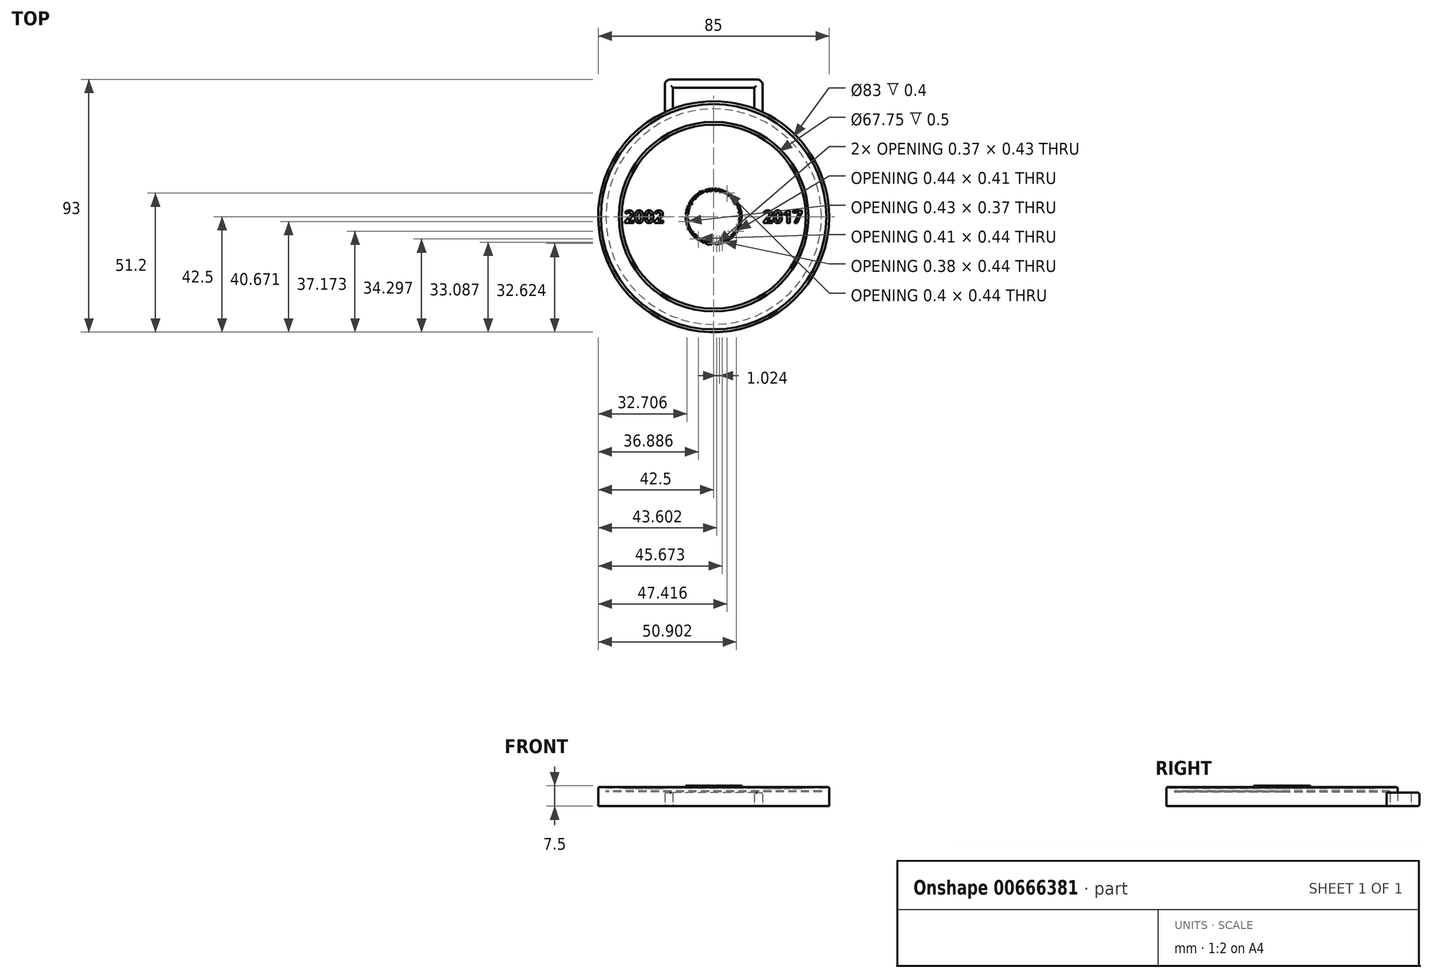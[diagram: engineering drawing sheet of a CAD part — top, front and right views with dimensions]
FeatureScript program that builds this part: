
annotation { "Feature Type Name" : "Feature", "Feature Type Description" : "" }
export const myFeature = defineFeature(function(context is Context, id is Id, definition is map)
    precondition{}
    {
        {
            var Q0;
            Q0=qCreatedBy(makeId("Top.planeOp"),FACE);
            var sketch = newSketch(context, id + "F0", { "sketchPlane" : qUnion([Q0])});
            skCircle(sketch, "E0", {"center": v(0, 0) * mm, "radius": 42.5 * mm});
            skSolve(sketch);
        }
        {
            var Q0;
            Q0 = qSketchRegion(id + "F0", true);
            extrude(context, id + "F1", {"entities" : qUnion([Q0]), "depth" : 7 * mm, "offsetDistance" : 25 * mm});
        }
        {
            var Q0;
            Q0=makeQuery(id+"F1.opExtrude","CAP_FACE",FACE,{"disambiguationData":[OSD([sQuery(id+"F0.wireOp",EDGE,"E0")])],"isStart":true});
            var sketch = newSketch(context, id + "F2", { "sketchPlane" : qUnion([Q0])});
            skLineSegment(sketch, "E1.bottom", {"start": v(-18, -50.5) * mm, "end": v(18, -50.5) * mm, "construction": true});
            skLineSegment(sketch, "E1.top", {"start": v(-18, -22.56) * mm, "end": v(18, -22.56) * mm, "construction": true});
            skLineSegment(sketch, "E1.left", {"start": v(-18, -50.5) * mm, "end": v(-18, -22.56) * mm, "construction": true});
            skLineSegment(sketch, "E1.right", {"start": v(18, -50.5) * mm, "end": v(18, -22.56) * mm, "construction": true});
            skLineSegment(sketch, "E2.bottom", {"start": v(-15, -47.5) * mm, "end": v(15, -47.5) * mm, "construction": true});
            skLineSegment(sketch, "E2.top", {"start": v(-15, -26.02) * mm, "end": v(15, -26.02) * mm, "construction": true});
            skLineSegment(sketch, "E2.left", {"start": v(-15, -47.5) * mm, "end": v(-15, -26.02) * mm, "construction": true});
            skLineSegment(sketch, "E2.right", {"start": v(15, -47.5) * mm, "end": v(15, -26.02) * mm, "construction": true});
            skLineSegment(sketch, "E3", {"start": v(-18, -22.56) * mm, "end": v(-18, -50.5) * mm});
            skLineSegment(sketch, "E4", {"start": v(18, -50.5) * mm, "end": v(-18, -50.5) * mm});
            skLineSegment(sketch, "E5", {"start": v(18, -50.5) * mm, "end": v(18, -22.56) * mm});
            skLineSegment(sketch, "E6", {"start": v(18, -22.56) * mm, "end": v(15, -26.02) * mm});
            skLineSegment(sketch, "E7", {"start": v(15, -47.5) * mm, "end": v(15, -26.02) * mm});
            skLineSegment(sketch, "E8", {"start": v(15, -47.5) * mm, "end": v(-15, -47.5) * mm});
            skLineSegment(sketch, "E9", {"start": v(-15, -47.5) * mm, "end": v(-15, -26.02) * mm});
            skLineSegment(sketch, "E10", {"start": v(-15, -26.02) * mm, "end": v(-18, -22.56) * mm});
            skSolve(sketch);
        }
        {
            var Q0;
            Q0 = qSketchRegion(id + "F2", true);
            extrude(context, id + "F3", {"entities" : qUnion([Q0]), "operationType" : NewBodyOperationType.ADD, "oppositeDirection" : true, "depth" : 5 * mm, "offsetDistance" : 25 * mm});
        }
        {
            var Q0;
            Q0=makeQuery(id+"F3.opExtrude","CAP_EDGE",EDGE,{"disambiguationData":[OSD([sQuery(id+"F2.wireOp",EDGE,"E4")])],"isStart":false});
            var Q1;
            Q1=makeQuery(id+"F3.opExtrude","CAP_EDGE",EDGE,{"disambiguationData":[OSD([sQuery(id+"F2.wireOp",EDGE,"E3")])],"isStart":false});
            var Q2;
            Q2=makeQuery(id+"F3.opExtrude","CAP_EDGE",EDGE,{"disambiguationData":[OSD([sQuery(id+"F2.wireOp",EDGE,"E8")])],"isStart":false});
            var Q3;
            Q3=makeQuery(id+"F3.opExtrude","CAP_EDGE",EDGE,{"disambiguationData":[OSD([sQuery(id+"F2.wireOp",EDGE,"E7")])],"isStart":false});
            var Q4;
            Q4=makeQuery(id+"F3.opExtrude","CAP_EDGE",EDGE,{"disambiguationData":[OSD([sQuery(id+"F2.wireOp",EDGE,"E9")])],"isStart":false});
            var Q5;
            Q5=makeQuery(id+"F3.opExtrude","CAP_EDGE",EDGE,{"disambiguationData":[OSD([sQuery(id+"F2.wireOp",EDGE,"E5")])],"isStart":false});
            var Q6;
            Q6=makeQuery(id+"F3.opExtrude","CAP_EDGE",EDGE,{"disambiguationData":[OSD([sQuery(id+"F2.wireOp",EDGE,"E8")])],"isStart":true});
            var Q7;
            Q7=makeQuery(id+"F3.opExtrude","CAP_EDGE",EDGE,{"disambiguationData":[OSD([sQuery(id+"F2.wireOp",EDGE,"E4")])],"isStart":true});
            var Q8;
            Q8=makeQuery(id+"F3.opExtrude","CAP_EDGE",EDGE,{"disambiguationData":[OSD([sQuery(id+"F2.wireOp",EDGE,"E5")])],"isStart":true});
            var Q9;
            Q9=makeQuery(id+"F3.opExtrude","CAP_EDGE",EDGE,{"disambiguationData":[OSD([sQuery(id+"F2.wireOp",EDGE,"E7")])],"isStart":true});
            var Q10;
            Q10=makeQuery(id+"F3.opExtrude","CAP_EDGE",EDGE,{"disambiguationData":[OSD([sQuery(id+"F2.wireOp",EDGE,"E9")])],"isStart":true});
            var Q11;
            Q11=makeQuery(id+"F3.opExtrude","CAP_EDGE",EDGE,{"disambiguationData":[OSD([sQuery(id+"F2.wireOp",EDGE,"E3")])],"isStart":true});
            fillet(context, id + "F4", {"entities" : qUnion([Q0, Q1, Q2, Q3, Q4, Q5, Q6, Q7, Q8, Q9, Q10, Q11]), "radius" : 0.6 * mm, "tangentPropagation" : true, "allowEdgeOverflow" : false});
        }
        {
            var Q0;
            Q0=makeQuery(id+"F3.opExtrude","SWEPT_EDGE",EDGE,{"disambiguationData":[OSD([sQuery(id+"F2.wireOp",EDGE,"E3"),sQuery(id+"F2.wireOp",EDGE,"E4")])]});
            var Q1;
            Q1=makeQuery(id+"F3.opExtrude","SWEPT_EDGE",EDGE,{"disambiguationData":[OSD([sQuery(id+"F2.wireOp",EDGE,"E4"),sQuery(id+"F2.wireOp",EDGE,"E5")])]});
            fillet(context, id + "F5", {"entities" : qUnion([Q0, Q1]), "radius" : 2 * mm, "tangentPropagation" : true, "allowEdgeOverflow" : false});
        }
        {
            var Q0;
            Q0=makeQuery(id+"F1.opExtrude","CAP_FACE",FACE,{"disambiguationData":[OSD([sQuery(id+"F0.wireOp",EDGE,"E0")])],"isStart":false});
            var sketch = newSketch(context, id + "F6", { "sketchPlane" : qUnion([Q0])});
            skFitSpline(sketch, "E11", {"points": [v(1.08, -9.67) * mm, v(1.02, -9.67) * mm, v(0.98, -9.7) * mm, v(0.95, -9.73) * mm]});
            skFitSpline(sketch, "E12", {"points": [v(0.95, -9.73) * mm, v(0.93, -9.77) * mm, v(0.92, -9.83) * mm, v(0.92, -9.9) * mm]});
            skFitSpline(sketch, "E13", {"points": [v(0.92, -9.9) * mm, v(0.93, -9.96) * mm, v(0.95, -10.01) * mm, v(0.98, -10.05) * mm]});
            skFitSpline(sketch, "E14", {"points": [v(0.98, -10.05) * mm, v(1.02, -10.08) * mm, v(1.07, -10.1) * mm, v(1.13, -10.09) * mm]});
            skFitSpline(sketch, "E15", {"points": [v(1.13, -10.09) * mm, v(1.18, -10.08) * mm, v(1.23, -10.06) * mm, v(1.25, -10.02) * mm]});
            skFitSpline(sketch, "E16", {"points": [v(1.25, -10.02) * mm, v(1.28, -9.98) * mm, v(1.29, -9.92) * mm, v(1.28, -9.85) * mm]});
            skFitSpline(sketch, "E17", {"points": [v(1.28, -9.85) * mm, v(1.27, -9.79) * mm, v(1.25, -9.74) * mm, v(1.21, -9.7) * mm]});
            skFitSpline(sketch, "E18", {"points": [v(1.21, -9.7) * mm, v(1.18, -9.67) * mm, v(1.13, -9.66) * mm, v(1.08, -9.67) * mm]});
            skFitSpline(sketch, "E19", {"points": [v(1.06, -9.5) * mm, v(1.2, -9.49) * mm, v(1.3, -9.5) * mm, v(1.4, -9.56) * mm]});
            skFitSpline(sketch, "E20", {"points": [v(1.4, -9.56) * mm, v(1.48, -9.61) * mm, v(1.53, -9.7) * mm, v(1.55, -9.81) * mm]});
            skFitSpline(sketch, "E21", {"points": [v(1.55, -9.81) * mm, v(1.57, -9.93) * mm, v(1.55, -10.03) * mm, v(1.47, -10.1) * mm]});
            skFitSpline(sketch, "E22", {"points": [v(1.47, -10.1) * mm, v(1.4, -10.18) * mm, v(1.3, -10.23) * mm, v(1.14, -10.25) * mm]});
            skFitSpline(sketch, "E23", {"points": [v(1.14, -10.25) * mm, v(1, -10.26) * mm, v(0.88, -10.24) * mm, v(0.79, -10.18) * mm]});
            skFitSpline(sketch, "E24", {"points": [v(0.79, -10.18) * mm, v(0.7, -10.12) * mm, v(0.65, -10.03) * mm, v(0.65, -9.92) * mm]});
            skFitSpline(sketch, "E25", {"points": [v(0.65, -9.92) * mm, v(0.64, -9.8) * mm, v(0.67, -9.7) * mm, v(0.75, -9.63) * mm]});
            skFitSpline(sketch, "E26", {"points": [v(0.75, -9.63) * mm, v(0.82, -9.56) * mm, v(0.92, -9.52) * mm, v(1.06, -9.5) * mm]});
            skFitSpline(sketch, "E27", {"points": [v(2.15, -9.05) * mm, v(2.23, -9.03) * mm, v(2.3, -9) * mm, v(2.39, -8.99) * mm]});
            skLineSegment(sketch, "E28", {"start": v(2.24, -9.42) * mm, "end": v(2.15, -9.05) * mm});
            skFitSpline(sketch, "E29", {"points": [v(2.65, -9.94) * mm, v(2.56, -9.97) * mm, v(2.47, -10) * mm, v(2.38, -10.01) * mm]});
            skLineSegment(sketch, "E30", {"start": v(2.39, -8.99) * mm, "end": v(2.65, -9.94) * mm});
            skFitSpline(sketch, "E31", {"points": [v(2.35, -9.91) * mm, v(2.33, -9.96) * mm, v(2.3, -10) * mm, v(2.25, -10.03) * mm]});
            skFitSpline(sketch, "E32", {"points": [v(2.25, -10.03) * mm, v(2.21, -10.06) * mm, v(2.16, -10.08) * mm, v(2.1, -10.1) * mm]});
            skFitSpline(sketch, "E33", {"points": [v(2.1, -10.1) * mm, v(2, -10.11) * mm, v(1.91, -10.1) * mm, v(1.83, -10.04) * mm]});
            skFitSpline(sketch, "E34", {"points": [v(1.83, -10.04) * mm, v(1.75, -9.98) * mm, v(1.7, -9.9) * mm, v(1.69, -9.8) * mm]});
            skFitSpline(sketch, "E35", {"points": [v(1.69, -9.8) * mm, v(1.67, -9.68) * mm, v(1.68, -9.59) * mm, v(1.73, -9.5) * mm]});
            skFitSpline(sketch, "E36", {"points": [v(1.73, -9.5) * mm, v(1.78, -9.43) * mm, v(1.86, -9.38) * mm, v(1.95, -9.36) * mm]});
            skFitSpline(sketch, "E37", {"points": [v(1.95, -9.36) * mm, v(2, -9.35) * mm, v(2.05, -9.35) * mm, v(2.1, -9.36) * mm]});
            skFitSpline(sketch, "E38", {"points": [v(2.1, -9.36) * mm, v(2.15, -9.37) * mm, v(2.2, -9.39) * mm, v(2.24, -9.42) * mm]});
            skLineSegment(sketch, "E39", {"start": v(2.38, -10.01) * mm, "end": v(2.35, -9.91) * mm});
            skFitSpline(sketch, "E40", {"points": [v(2.17, -9.9) * mm, v(2.23, -9.9) * mm, v(2.27, -9.87) * mm, v(2.29, -9.83) * mm]});
            skFitSpline(sketch, "E41", {"points": [v(2.29, -9.83) * mm, v(2.3, -9.79) * mm, v(2.31, -9.73) * mm, v(2.3, -9.67) * mm]});
            skFitSpline(sketch, "E42", {"points": [v(2.3, -9.67) * mm, v(2.28, -9.6) * mm, v(2.25, -9.55) * mm, v(2.22, -9.52) * mm]});
            skFitSpline(sketch, "E43", {"points": [v(2.22, -9.52) * mm, v(2.18, -9.5) * mm, v(2.13, -9.49) * mm, v(2.08, -9.5) * mm]});
            skFitSpline(sketch, "E44", {"points": [v(2.08, -9.5) * mm, v(2.03, -9.51) * mm, v(1.99, -9.54) * mm, v(1.97, -9.58) * mm]});
            skFitSpline(sketch, "E45", {"points": [v(1.97, -9.58) * mm, v(1.95, -9.62) * mm, v(1.94, -9.67) * mm, v(1.95, -9.74) * mm]});
            skFitSpline(sketch, "E46", {"points": [v(1.95, -9.74) * mm, v(1.97, -9.8) * mm, v(2, -9.86) * mm, v(2.03, -9.88) * mm]});
            skFitSpline(sketch, "E47", {"points": [v(2.03, -9.88) * mm, v(2.07, -9.91) * mm, v(2.11, -9.92) * mm, v(2.17, -9.9) * mm]});
            skFitSpline(sketch, "E48", {"points": [v(3.12, -8.76) * mm, v(3.2, -8.73) * mm, v(3.28, -8.7) * mm, v(3.36, -8.67) * mm]});
            skLineSegment(sketch, "E49", {"start": v(3.25, -9.12) * mm, "end": v(3.12, -8.76) * mm});
            skFitSpline(sketch, "E50", {"points": [v(3.72, -9.6) * mm, v(3.63, -9.63) * mm, v(3.54, -9.66) * mm, v(3.46, -9.7) * mm]});
            skLineSegment(sketch, "E51", {"start": v(3.36, -8.67) * mm, "end": v(3.72, -9.6) * mm});
            skFitSpline(sketch, "E52", {"points": [v(3.42, -9.6) * mm, v(3.4, -9.65) * mm, v(3.37, -9.69) * mm, v(3.34, -9.72) * mm]});
            skFitSpline(sketch, "E53", {"points": [v(3.34, -9.72) * mm, v(3.3, -9.76) * mm, v(3.25, -9.78) * mm, v(3.2, -9.8) * mm]});
            skFitSpline(sketch, "E54", {"points": [v(3.2, -9.8) * mm, v(3.1, -9.83) * mm, v(3, -9.83) * mm, v(2.92, -9.78) * mm]});
            skFitSpline(sketch, "E55", {"points": [v(2.92, -9.78) * mm, v(2.83, -9.73) * mm, v(2.77, -9.65) * mm, v(2.74, -9.55) * mm]});
            skFitSpline(sketch, "E56", {"points": [v(2.74, -9.55) * mm, v(2.71, -9.44) * mm, v(2.72, -9.35) * mm, v(2.76, -9.26) * mm]});
            skFitSpline(sketch, "E57", {"points": [v(2.76, -9.26) * mm, v(2.8, -9.18) * mm, v(2.87, -9.12) * mm, v(2.96, -9.09) * mm]});
            skFitSpline(sketch, "E58", {"points": [v(2.96, -9.09) * mm, v(3.01, -9.07) * mm, v(3.06, -9.06) * mm, v(3.1, -9.07) * mm]});
            skFitSpline(sketch, "E59", {"points": [v(3.1, -9.07) * mm, v(3.16, -9.07) * mm, v(3.2, -9.09) * mm, v(3.25, -9.12) * mm]});
            skLineSegment(sketch, "E60", {"start": v(3.46, -9.7) * mm, "end": v(3.42, -9.6) * mm});
            skFitSpline(sketch, "E61", {"points": [v(3.24, -9.61) * mm, v(3.3, -9.6) * mm, v(3.33, -9.56) * mm, v(3.35, -9.52) * mm]});
            skFitSpline(sketch, "E62", {"points": [v(3.35, -9.52) * mm, v(3.36, -9.47) * mm, v(3.36, -9.42) * mm, v(3.34, -9.35) * mm]});
            skFitSpline(sketch, "E63", {"points": [v(3.34, -9.35) * mm, v(3.31, -9.3) * mm, v(3.28, -9.25) * mm, v(3.24, -9.22) * mm]});
            skFitSpline(sketch, "E64", {"points": [v(3.24, -9.22) * mm, v(3.2, -9.2) * mm, v(3.16, -9.2) * mm, v(3.1, -9.21) * mm]});
            skFitSpline(sketch, "E65", {"points": [v(3.1, -9.21) * mm, v(3.05, -9.23) * mm, v(3.02, -9.26) * mm, v(3, -9.3) * mm]});
            skFitSpline(sketch, "E66", {"points": [v(3, -9.3) * mm, v(2.98, -9.35) * mm, v(2.99, -9.4) * mm, v(3, -9.47) * mm]});
            skFitSpline(sketch, "E67", {"points": [v(3, -9.47) * mm, v(3.03, -9.53) * mm, v(3.06, -9.58) * mm, v(3.1, -9.6) * mm]});
            skFitSpline(sketch, "E68", {"points": [v(3.1, -9.6) * mm, v(3.14, -9.63) * mm, v(3.18, -9.63) * mm, v(3.24, -9.61) * mm]});
            skFitSpline(sketch, "E69", {"points": [v(4.6, -8.87) * mm, v(4.42, -8.97) * mm, v(4.23, -9.06) * mm, v(4.04, -9.14) * mm]});
            skFitSpline(sketch, "E70", {"points": [v(4.04, -9.14) * mm, v(4.07, -9.19) * mm, v(4.1, -9.22) * mm, v(4.15, -9.22) * mm]});
            skFitSpline(sketch, "E71", {"points": [v(4.15, -9.22) * mm, v(4.2, -9.23) * mm, v(4.25, -9.22) * mm, v(4.32, -9.2) * mm]});
            skFitSpline(sketch, "E72", {"points": [v(4.32, -9.2) * mm, v(4.37, -9.17) * mm, v(4.42, -9.14) * mm, v(4.47, -9.1) * mm]});
            skFitSpline(sketch, "E73", {"points": [v(4.47, -9.1) * mm, v(4.51, -9.06) * mm, v(4.56, -9.01) * mm, v(4.6, -8.96) * mm]});
            skLineSegment(sketch, "E74", {"start": v(4.57, -8.81) * mm, "end": v(4.6, -8.87) * mm});
            skFitSpline(sketch, "E75", {"points": [v(4.68, -9.11) * mm, v(4.63, -9.16) * mm, v(4.58, -9.2) * mm, v(4.53, -9.24) * mm]});
            skFitSpline(sketch, "E76", {"points": [v(4.53, -9.24) * mm, v(4.47, -9.28) * mm, v(4.42, -9.31) * mm, v(4.36, -9.34) * mm]});
            skFitSpline(sketch, "E77", {"points": [v(4.36, -9.34) * mm, v(4.22, -9.4) * mm, v(4.1, -9.42) * mm, v(3.99, -9.4) * mm]});
            skFitSpline(sketch, "E78", {"points": [v(3.99, -9.4) * mm, v(3.88, -9.37) * mm, v(3.81, -9.3) * mm, v(3.77, -9.19) * mm]});
            skFitSpline(sketch, "E79", {"points": [v(3.77, -9.19) * mm, v(3.72, -9.08) * mm, v(3.72, -8.98) * mm, v(3.77, -8.89) * mm]});
            skFitSpline(sketch, "E80", {"points": [v(3.77, -8.89) * mm, v(3.82, -8.8) * mm, v(3.9, -8.72) * mm, v(4.03, -8.67) * mm]});
            skFitSpline(sketch, "E81", {"points": [v(4.03, -8.67) * mm, v(4.14, -8.61) * mm, v(4.25, -8.6) * mm, v(4.35, -8.63) * mm]});
            skFitSpline(sketch, "E82", {"points": [v(4.35, -8.63) * mm, v(4.44, -8.65) * mm, v(4.52, -8.71) * mm, v(4.57, -8.81) * mm]});
            skFitSpline(sketch, "E83", {"points": [v(4.57, -8.81) * mm, v(4.57, -8.81) * mm, v(4.57, -8.81) * mm, v(4.57, -8.81) * mm, v(4.57, -8.81) * mm]});
            skLineSegment(sketch, "E84", {"start": v(4.6, -8.96) * mm, "end": v(4.68, -9.11) * mm});
            skFitSpline(sketch, "E85", {"points": [v(4.3, -8.87) * mm, v(4.28, -8.83) * mm, v(4.25, -8.8) * mm, v(4.21, -8.8) * mm]});
            skFitSpline(sketch, "E86", {"points": [v(4.21, -8.8) * mm, v(4.17, -8.78) * mm, v(4.13, -8.78) * mm, v(4.1, -8.8) * mm]});
            skFitSpline(sketch, "E87", {"points": [v(4.1, -8.8) * mm, v(4.05, -8.82) * mm, v(4.01, -8.85) * mm, v(4, -8.89) * mm]});
            skFitSpline(sketch, "E88", {"points": [v(4, -8.89) * mm, v(3.98, -8.92) * mm, v(3.97, -8.96) * mm, v(3.99, -9.01) * mm]});
            skFitSpline(sketch, "E89", {"points": [v(3.99, -9.01) * mm, v(4.1, -8.96) * mm, v(4.2, -8.92) * mm, v(4.3, -8.87) * mm]});
            skFitSpline(sketch, "E90", {"points": [v(3.93, -8.63) * mm, v(3.84, -8.58) * mm, v(3.75, -8.53) * mm, v(3.67, -8.48) * mm]});
            skFitSpline(sketch, "E91", {"points": [v(3.67, -8.48) * mm, v(3.7, -8.47) * mm, v(3.74, -8.45) * mm, v(3.78, -8.43) * mm]});
            skFitSpline(sketch, "E92", {"points": [v(3.78, -8.43) * mm, v(3.84, -8.46) * mm, v(3.9, -8.48) * mm, v(3.97, -8.5) * mm]});
            skFitSpline(sketch, "E93", {"points": [v(3.97, -8.5) * mm, v(3.99, -8.45) * mm, v(4.01, -8.38) * mm, v(4.03, -8.32) * mm]});
            skFitSpline(sketch, "E94", {"points": [v(4.03, -8.32) * mm, v(4.07, -8.3) * mm, v(4.1, -8.28) * mm, v(4.14, -8.26) * mm]});
            skFitSpline(sketch, "E95", {"points": [v(4.14, -8.26) * mm, v(4.12, -8.36) * mm, v(4.1, -8.46) * mm, v(4.09, -8.56) * mm]});
            skFitSpline(sketch, "E96", {"points": [v(4.09, -8.56) * mm, v(4.03, -8.58) * mm, v(3.98, -8.6) * mm, v(3.93, -8.63) * mm]});
            skFitSpline(sketch, "E97", {"points": [v(4.45, -8.16) * mm, v(4.52, -8.12) * mm, v(4.6, -8.08) * mm, v(4.66, -8.04) * mm]});
            skFitSpline(sketch, "E98", {"points": [v(5.16, -8.9) * mm, v(5.08, -8.95) * mm, v(5, -9) * mm, v(4.92, -9.04) * mm]});
            skLineSegment(sketch, "E99", {"start": v(4.66, -8.04) * mm, "end": v(5.16, -8.9) * mm});
            skLineSegment(sketch, "E100", {"start": v(4.92, -9.04) * mm, "end": v(4.45, -8.16) * mm});
            skFitSpline(sketch, "E101", {"points": [v(5.93, -8.05) * mm, v(5.76, -8.18) * mm, v(5.59, -8.3) * mm, v(5.41, -8.4) * mm]});
            skFitSpline(sketch, "E102", {"points": [v(5.41, -8.4) * mm, v(5.45, -8.45) * mm, v(5.49, -8.47) * mm, v(5.54, -8.47) * mm]});
            skFitSpline(sketch, "E103", {"points": [v(5.54, -8.47) * mm, v(5.58, -8.47) * mm, v(5.64, -8.45) * mm, v(5.7, -8.41) * mm]});
            skFitSpline(sketch, "E104", {"points": [v(5.7, -8.41) * mm, v(5.74, -8.38) * mm, v(5.79, -8.34) * mm, v(5.83, -8.3) * mm]});
            skFitSpline(sketch, "E105", {"points": [v(5.83, -8.3) * mm, v(5.87, -8.25) * mm, v(5.9, -8.2) * mm, v(5.94, -8.14) * mm]});
            skLineSegment(sketch, "E106", {"start": v(5.89, -8) * mm, "end": v(5.93, -8.05) * mm});
            skFitSpline(sketch, "E107", {"points": [v(6.04, -8.28) * mm, v(6, -8.33) * mm, v(5.96, -8.38) * mm, v(5.91, -8.43) * mm]});
            skFitSpline(sketch, "E108", {"points": [v(5.91, -8.43) * mm, v(5.86, -8.48) * mm, v(5.81, -8.52) * mm, v(5.76, -8.55) * mm]});
            skFitSpline(sketch, "E109", {"points": [v(5.76, -8.55) * mm, v(5.63, -8.64) * mm, v(5.5, -8.68) * mm, v(5.4, -8.67) * mm]});
            skFitSpline(sketch, "E110", {"points": [v(5.4, -8.67) * mm, v(5.3, -8.65) * mm, v(5.21, -8.6) * mm, v(5.15, -8.5) * mm]});
            skFitSpline(sketch, "E111", {"points": [v(5.15, -8.5) * mm, v(5.09, -8.4) * mm, v(5.08, -8.3) * mm, v(5.1, -8.2) * mm]});
            skFitSpline(sketch, "E112", {"points": [v(5.1, -8.2) * mm, v(5.14, -8.1) * mm, v(5.22, -8.01) * mm, v(5.33, -7.94) * mm]});
            skFitSpline(sketch, "E113", {"points": [v(5.33, -7.94) * mm, v(5.43, -7.87) * mm, v(5.54, -7.84) * mm, v(5.64, -7.85) * mm]});
            skFitSpline(sketch, "E114", {"points": [v(5.64, -7.85) * mm, v(5.74, -7.86) * mm, v(5.82, -7.9) * mm, v(5.89, -8) * mm]});
            skLineSegment(sketch, "E115", {"start": v(5.94, -8.14) * mm, "end": v(6.04, -8.28) * mm});
            skFitSpline(sketch, "E116", {"points": [v(5.62, -8.1) * mm, v(5.6, -8.06) * mm, v(5.57, -8.04) * mm, v(5.53, -8.03) * mm]});
            skFitSpline(sketch, "E117", {"points": [v(5.53, -8.03) * mm, v(5.5, -8.03) * mm, v(5.45, -8.04) * mm, v(5.41, -8.06) * mm]});
            skFitSpline(sketch, "E118", {"points": [v(5.41, -8.06) * mm, v(5.37, -8.1) * mm, v(5.34, -8.12) * mm, v(5.33, -8.16) * mm]});
            skFitSpline(sketch, "E119", {"points": [v(5.33, -8.16) * mm, v(5.32, -8.2) * mm, v(5.32, -8.24) * mm, v(5.34, -8.29) * mm]});
            skFitSpline(sketch, "E120", {"points": [v(5.34, -8.29) * mm, v(5.44, -8.22) * mm, v(5.53, -8.16) * mm, v(5.62, -8.1) * mm]});
            skFitSpline(sketch, "E121", {"points": [v(6.93, -7.62) * mm, v(6.86, -7.68) * mm, v(6.8, -7.74) * mm, v(6.72, -7.8) * mm]});
            skLineSegment(sketch, "E122", {"start": v(6.64, -7.3) * mm, "end": v(6.93, -7.62) * mm});
            skFitSpline(sketch, "E123", {"points": [v(6.5, -7.55) * mm, v(6.47, -7.5) * mm, v(6.44, -7.47) * mm, v(6.42, -7.45) * mm]});
            skFitSpline(sketch, "E124", {"points": [v(6.42, -7.45) * mm, v(6.4, -7.44) * mm, v(6.39, -7.43) * mm, v(6.38, -7.42) * mm]});
            skFitSpline(sketch, "E125", {"points": [v(6.38, -7.42) * mm, v(6.36, -7.42) * mm, v(6.34, -7.42) * mm, v(6.32, -7.42) * mm]});
            skFitSpline(sketch, "E126", {"points": [v(6.32, -7.42) * mm, v(6.3, -7.43) * mm, v(6.29, -7.44) * mm, v(6.27, -7.45) * mm]});
            skFitSpline(sketch, "E127", {"points": [v(6.27, -7.45) * mm, v(6.23, -7.49) * mm, v(6.2, -7.53) * mm, v(6.2, -7.58) * mm]});
            skFitSpline(sketch, "E128", {"points": [v(6.2, -7.58) * mm, v(6.2, -7.62) * mm, v(6.22, -7.67) * mm, v(6.26, -7.72) * mm]});
            skLineSegment(sketch, "E129", {"start": v(6.72, -7.8) * mm, "end": v(6.68, -7.75) * mm});
            skLineSegment(sketch, "E130", {"start": v(6.68, -7.75) * mm, "end": v(6.5, -7.55) * mm});
            skFitSpline(sketch, "E131", {"points": [v(6.48, -8) * mm, v(6.41, -8.06) * mm, v(6.34, -8.11) * mm, v(6.27, -8.17) * mm]});
            skLineSegment(sketch, "E132", {"start": v(6.26, -7.72) * mm, "end": v(6.48, -8) * mm});
            skFitSpline(sketch, "E133", {"points": [v(5.84, -7.6) * mm, v(5.9, -7.55) * mm, v(5.97, -7.5) * mm, v(6.04, -7.44) * mm]});
            skLineSegment(sketch, "E134", {"start": v(6.27, -8.17) * mm, "end": v(5.84, -7.6) * mm});
            skFitSpline(sketch, "E135", {"points": [v(6.1, -7.52) * mm, v(6.1, -7.47) * mm, v(6.12, -7.42) * mm, v(6.14, -7.37) * mm]});
            skFitSpline(sketch, "E136", {"points": [v(6.14, -7.37) * mm, v(6.16, -7.33) * mm, v(6.2, -7.3) * mm, v(6.23, -7.26) * mm]});
            skFitSpline(sketch, "E137", {"points": [v(6.23, -7.26) * mm, v(6.3, -7.2) * mm, v(6.37, -7.17) * mm, v(6.44, -7.18) * mm]});
            skFitSpline(sketch, "E138", {"points": [v(6.44, -7.18) * mm, v(6.5, -7.18) * mm, v(6.58, -7.22) * mm, v(6.64, -7.3) * mm]});
            skFitSpline(sketch, "E139", {"points": [v(6.64, -7.3) * mm, v(6.64, -7.3) * mm, v(6.64, -7.3) * mm, v(6.64, -7.3) * mm, v(6.64, -7.3) * mm]});
            skLineSegment(sketch, "E140", {"start": v(6.04, -7.44) * mm, "end": v(6.1, -7.52) * mm});
            skFitSpline(sketch, "E141", {"points": [v(6.63, -6.92) * mm, v(6.7, -6.87) * mm, v(6.75, -6.8) * mm, v(6.81, -6.75) * mm]});
            skFitSpline(sketch, "E142", {"points": [v(7.32, -7.25) * mm, v(7.25, -7.32) * mm, v(7.19, -7.38) * mm, v(7.12, -7.44) * mm]});
            skLineSegment(sketch, "E143", {"start": v(6.81, -6.75) * mm, "end": v(7.32, -7.25) * mm});
            skFitSpline(sketch, "E144", {"points": [v(6.57, -6.52) * mm, v(6.61, -6.48) * mm, v(6.66, -6.43) * mm, v(6.7, -6.38) * mm]});
            skFitSpline(sketch, "E145", {"points": [v(6.7, -6.38) * mm, v(6.7, -6.5) * mm, v(6.7, -6.62) * mm, v(6.7, -6.74) * mm]});
            skFitSpline(sketch, "E146", {"points": [v(6.7, -6.74) * mm, v(6.66, -6.77) * mm, v(6.63, -6.8) * mm, v(6.6, -6.83) * mm]});
            skFitSpline(sketch, "E147", {"points": [v(6.6, -6.83) * mm, v(6.59, -6.73) * mm, v(6.58, -6.63) * mm, v(6.57, -6.52) * mm]});
            skLineSegment(sketch, "E148", {"start": v(7.12, -7.44) * mm, "end": v(6.63, -6.92) * mm});
            skFitSpline(sketch, "E149", {"points": [v(7.11, -6.01) * mm, v(7.16, -5.95) * mm, v(7.22, -5.88) * mm, v(7.27, -5.82) * mm]});
            skFitSpline(sketch, "E150", {"points": [v(7.69, -6.16) * mm, v(7.68, -6.02) * mm, v(7.68, -5.9) * mm, v(7.66, -5.76) * mm]});
            skFitSpline(sketch, "E151", {"points": [v(7.66, -5.76) * mm, v(7.72, -5.68) * mm, v(7.78, -5.6) * mm, v(7.84, -5.52) * mm]});
            skFitSpline(sketch, "E152", {"points": [v(7.84, -5.52) * mm, v(7.85, -5.7) * mm, v(7.86, -5.86) * mm, v(7.87, -6.04) * mm]});
            skFitSpline(sketch, "E153", {"points": [v(7.87, -6.04) * mm, v(8.06, -6) * mm, v(8.25, -5.96) * mm, v(8.44, -5.9) * mm]});
            skFitSpline(sketch, "E154", {"points": [v(8.44, -5.9) * mm, v(8.38, -6) * mm, v(8.31, -6.09) * mm, v(8.25, -6.18) * mm]});
            skFitSpline(sketch, "E155", {"points": [v(8.25, -6.18) * mm, v(8.1, -6.2) * mm, v(7.95, -6.23) * mm, v(7.8, -6.25) * mm]});
            skLineSegment(sketch, "E156", {"start": v(7.27, -5.82) * mm, "end": v(7.69, -6.16) * mm});
            skFitSpline(sketch, "E157", {"points": [v(8.04, -6.44) * mm, v(7.98, -6.51) * mm, v(7.93, -6.58) * mm, v(7.87, -6.65) * mm]});
            skLineSegment(sketch, "E158", {"start": v(7.8, -6.25) * mm, "end": v(8.04, -6.44) * mm});
            skFitSpline(sketch, "E159", {"points": [v(8.22, -5.21) * mm, v(8.2, -5.26) * mm, v(8.18, -5.3) * mm, v(8.2, -5.35) * mm]});
            skFitSpline(sketch, "E160", {"points": [v(8.2, -5.35) * mm, v(8.21, -5.4) * mm, v(8.25, -5.44) * mm, v(8.3, -5.48) * mm]});
            skFitSpline(sketch, "E161", {"points": [v(8.3, -5.48) * mm, v(8.36, -5.51) * mm, v(8.41, -5.53) * mm, v(8.46, -5.52) * mm]});
            skFitSpline(sketch, "E162", {"points": [v(8.46, -5.52) * mm, v(8.5, -5.52) * mm, v(8.55, -5.49) * mm, v(8.58, -5.44) * mm]});
            skFitSpline(sketch, "E163", {"points": [v(8.58, -5.44) * mm, v(8.61, -5.39) * mm, v(8.62, -5.34) * mm, v(8.6, -5.3) * mm]});
            skFitSpline(sketch, "E164", {"points": [v(8.6, -5.3) * mm, v(8.6, -5.25) * mm, v(8.55, -5.2) * mm, v(8.5, -5.17) * mm]});
            skFitSpline(sketch, "E165", {"points": [v(8.5, -5.17) * mm, v(8.44, -5.14) * mm, v(8.38, -5.12) * mm, v(8.34, -5.13) * mm]});
            skFitSpline(sketch, "E166", {"points": [v(8.34, -5.13) * mm, v(8.3, -5.14) * mm, v(8.25, -5.16) * mm, v(8.22, -5.21) * mm]});
            skLineSegment(sketch, "E167", {"start": v(7.87, -6.65) * mm, "end": v(7.11, -6.01) * mm});
            skFitSpline(sketch, "E168", {"points": [v(8.08, -5.12) * mm, v(8.16, -5) * mm, v(8.24, -4.93) * mm, v(8.34, -4.9) * mm]});
            skFitSpline(sketch, "E169", {"points": [v(8.34, -4.9) * mm, v(8.43, -4.87) * mm, v(8.53, -4.88) * mm, v(8.64, -4.93) * mm]});
            skFitSpline(sketch, "E170", {"points": [v(8.64, -4.93) * mm, v(8.74, -5) * mm, v(8.8, -5.07) * mm, v(8.81, -5.18) * mm]});
            skFitSpline(sketch, "E171", {"points": [v(8.81, -5.18) * mm, v(8.83, -5.28) * mm, v(8.8, -5.4) * mm, v(8.72, -5.52) * mm]});
            skFitSpline(sketch, "E172", {"points": [v(8.72, -5.52) * mm, v(8.64, -5.65) * mm, v(8.55, -5.73) * mm, v(8.44, -5.76) * mm]});
            skFitSpline(sketch, "E173", {"points": [v(8.44, -5.76) * mm, v(8.34, -5.8) * mm, v(8.24, -5.77) * mm, v(8.15, -5.7) * mm]});
            skFitSpline(sketch, "E174", {"points": [v(8.15, -5.7) * mm, v(8.05, -5.64) * mm, v(8, -5.55) * mm, v(7.99, -5.45) * mm]});
            skFitSpline(sketch, "E175", {"points": [v(7.99, -5.45) * mm, v(7.98, -5.35) * mm, v(8.01, -5.24) * mm, v(8.08, -5.12) * mm]});
            skFitSpline(sketch, "E176", {"points": [v(8.85, -3.98) * mm, v(8.83, -3.93) * mm, v(8.81, -3.88) * mm, v(8.8, -3.83) * mm]});
            skFitSpline(sketch, "E177", {"points": [v(8.8, -3.83) * mm, v(8.8, -3.78) * mm, v(8.81, -3.73) * mm, v(8.84, -3.68) * mm]});
            skFitSpline(sketch, "E178", {"points": [v(8.84, -3.68) * mm, v(8.87, -3.6) * mm, v(8.92, -3.54) * mm, v(8.99, -3.52) * mm]});
            skFitSpline(sketch, "E179", {"points": [v(8.99, -3.52) * mm, v(9.05, -3.5) * mm, v(9.13, -3.5) * mm, v(9.22, -3.53) * mm]});
            skFitSpline(sketch, "E180", {"points": [v(9.62, -3.69) * mm, v(9.59, -3.77) * mm, v(9.56, -3.86) * mm, v(9.52, -3.94) * mm]});
            skLineSegment(sketch, "E181", {"start": v(9.22, -3.53) * mm, "end": v(9.62, -3.69) * mm});
            skFitSpline(sketch, "E182", {"points": [v(9.18, -3.8) * mm, v(9.17, -3.8) * mm, v(9.17, -3.8) * mm, v(9.16, -3.8) * mm]});
            skFitSpline(sketch, "E183", {"points": [v(9.16, -3.8) * mm, v(9.16, -3.79) * mm, v(9.15, -3.79) * mm, v(9.14, -3.78) * mm]});
            skFitSpline(sketch, "E184", {"points": [v(9.14, -3.78) * mm, v(9.1, -3.76) * mm, v(9.05, -3.76) * mm, v(9.03, -3.76) * mm]});
            skFitSpline(sketch, "E185", {"points": [v(9.03, -3.76) * mm, v(9, -3.77) * mm, v(8.98, -3.8) * mm, v(8.96, -3.82) * mm]});
            skFitSpline(sketch, "E186", {"points": [v(8.96, -3.82) * mm, v(8.94, -3.87) * mm, v(8.94, -3.91) * mm, v(8.97, -3.95) * mm]});
            skFitSpline(sketch, "E187", {"points": [v(8.97, -3.95) * mm, v(8.99, -4) * mm, v(9.03, -4.02) * mm, v(9.1, -4.05) * mm]});
            skLineSegment(sketch, "E188", {"start": v(9.52, -3.94) * mm, "end": v(9.18, -3.8) * mm});
            skFitSpline(sketch, "E189", {"points": [v(9.41, -4.2) * mm, v(9.37, -4.28) * mm, v(9.33, -4.36) * mm, v(9.3, -4.45) * mm]});
            skLineSegment(sketch, "E190", {"start": v(9.1, -4.05) * mm, "end": v(9.41, -4.2) * mm});
            skFitSpline(sketch, "E191", {"points": [v(8.96, -4.29) * mm, v(8.89, -4.25) * mm, v(8.84, -4.24) * mm, v(8.81, -4.24) * mm]});
            skFitSpline(sketch, "E192", {"points": [v(8.81, -4.24) * mm, v(8.78, -4.24) * mm, v(8.76, -4.26) * mm, v(8.74, -4.3) * mm]});
            skFitSpline(sketch, "E193", {"points": [v(8.74, -4.3) * mm, v(8.72, -4.34) * mm, v(8.72, -4.39) * mm, v(8.74, -4.43) * mm]});
            skFitSpline(sketch, "E194", {"points": [v(8.74, -4.43) * mm, v(8.76, -4.47) * mm, v(8.8, -4.5) * mm, v(8.86, -4.53) * mm]});
            skLineSegment(sketch, "E195", {"start": v(9.3, -4.45) * mm, "end": v(8.96, -4.29) * mm});
            skFitSpline(sketch, "E196", {"points": [v(9.17, -4.7) * mm, v(9.13, -4.78) * mm, v(9.09, -4.86) * mm, v(9.04, -4.94) * mm]});
            skLineSegment(sketch, "E197", {"start": v(8.86, -4.53) * mm, "end": v(9.17, -4.7) * mm});
            skFitSpline(sketch, "E198", {"points": [v(8.42, -4.6) * mm, v(8.46, -4.52) * mm, v(8.5, -4.44) * mm, v(8.54, -4.37) * mm]});
            skLineSegment(sketch, "E199", {"start": v(9.04, -4.94) * mm, "end": v(8.42, -4.6) * mm});
            skFitSpline(sketch, "E200", {"points": [v(8.63, -4.42) * mm, v(8.6, -4.37) * mm, v(8.6, -4.32) * mm, v(8.6, -4.28) * mm]});
            skFitSpline(sketch, "E201", {"points": [v(8.6, -4.28) * mm, v(8.6, -4.23) * mm, v(8.6, -4.19) * mm, v(8.63, -4.14) * mm]});
            skFitSpline(sketch, "E202", {"points": [v(8.63, -4.14) * mm, v(8.65, -4.1) * mm, v(8.68, -4.06) * mm, v(8.72, -4.03) * mm]});
            skFitSpline(sketch, "E203", {"points": [v(8.72, -4.03) * mm, v(8.76, -4) * mm, v(8.8, -3.98) * mm, v(8.85, -3.98) * mm]});
            skFitSpline(sketch, "E204", {"points": [v(8.85, -3.98) * mm, v(8.85, -3.98) * mm, v(8.85, -3.98) * mm, v(8.85, -3.98) * mm, v(8.85, -3.98) * mm]});
            skLineSegment(sketch, "E205", {"start": v(8.54, -4.37) * mm, "end": v(8.63, -4.42) * mm});
            skFitSpline(sketch, "E206", {"points": [v(9.04, -3.21) * mm, v(9.07, -3.13) * mm, v(9.1, -3.05) * mm, v(9.12, -2.97) * mm]});
            skLineSegment(sketch, "E207", {"start": v(9.45, -3.36) * mm, "end": v(9.04, -3.21) * mm});
            skFitSpline(sketch, "E208", {"points": [v(9.19, -3) * mm, v(9.23, -3) * mm, v(9.27, -3.02) * mm, v(9.33, -3.04) * mm]});
            skFitSpline(sketch, "E209", {"points": [v(9.33, -3.04) * mm, v(9.38, -3.06) * mm, v(9.42, -3.07) * mm, v(9.44, -3.08) * mm]});
            skFitSpline(sketch, "E210", {"points": [v(9.44, -3.08) * mm, v(9.5, -3.1) * mm, v(9.53, -3.1) * mm, v(9.56, -3.1) * mm]});
            skFitSpline(sketch, "E211", {"points": [v(9.56, -3.1) * mm, v(9.58, -3.11) * mm, v(9.6, -3.11) * mm, v(9.62, -3.1) * mm]});
            skFitSpline(sketch, "E212", {"points": [v(9.62, -3.1) * mm, v(9.63, -3.1) * mm, v(9.65, -3.1) * mm, v(9.66, -3.08) * mm]});
            skFitSpline(sketch, "E213", {"points": [v(9.66, -3.08) * mm, v(9.68, -3.06) * mm, v(9.69, -3.05) * mm, v(9.7, -3.02) * mm]});
            skFitSpline(sketch, "E214", {"points": [v(9.7, -3.02) * mm, v(9.7, -2.97) * mm, v(9.7, -2.92) * mm, v(9.68, -2.88) * mm]});
            skFitSpline(sketch, "E215", {"points": [v(9.68, -2.88) * mm, v(9.65, -2.84) * mm, v(9.6, -2.81) * mm, v(9.55, -2.8) * mm]});
            skLineSegment(sketch, "E216", {"start": v(9.12, -2.97) * mm, "end": v(9.19, -3) * mm});
            skFitSpline(sketch, "E217", {"points": [v(9.2, -2.7) * mm, v(9.23, -2.6) * mm, v(9.26, -2.53) * mm, v(9.28, -2.44) * mm]});
            skLineSegment(sketch, "E218", {"start": v(9.55, -2.8) * mm, "end": v(9.2, -2.7) * mm});
            skFitSpline(sketch, "E219", {"points": [v(9.97, -2.63) * mm, v(9.94, -2.72) * mm, v(9.92, -2.8) * mm, v(9.9, -2.9) * mm]});
            skLineSegment(sketch, "E220", {"start": v(9.28, -2.44) * mm, "end": v(9.97, -2.63) * mm});
            skFitSpline(sketch, "E221", {"points": [v(9.8, -2.87) * mm, v(9.82, -2.92) * mm, v(9.84, -2.97) * mm, v(9.84, -3.02) * mm]});
            skFitSpline(sketch, "E222", {"points": [v(9.84, -3.02) * mm, v(9.85, -3.07) * mm, v(9.84, -3.12) * mm, v(9.83, -3.17) * mm]});
            skFitSpline(sketch, "E223", {"points": [v(9.83, -3.17) * mm, v(9.8, -3.27) * mm, v(9.75, -3.33) * mm, v(9.68, -3.36) * mm]});
            skFitSpline(sketch, "E224", {"points": [v(9.68, -3.36) * mm, v(9.62, -3.4) * mm, v(9.54, -3.4) * mm, v(9.45, -3.36) * mm]});
            skFitSpline(sketch, "E225", {"points": [v(9.45, -3.36) * mm, v(9.45, -3.36) * mm, v(9.45, -3.36) * mm, v(9.45, -3.36) * mm, v(9.45, -3.36) * mm]});
            skLineSegment(sketch, "E226", {"start": v(9.9, -2.9) * mm, "end": v(9.8, -2.87) * mm});
            skFitSpline(sketch, "E227", {"points": [v(10.2, -1.53) * mm, v(10.19, -1.62) * mm, v(10.17, -1.7) * mm, v(10.16, -1.8) * mm]});
            skLineSegment(sketch, "E228", {"start": v(9.77, -1.46) * mm, "end": v(10.2, -1.53) * mm});
            skFitSpline(sketch, "E229", {"points": [v(9.83, -1.74) * mm, v(9.77, -1.73) * mm, v(9.73, -1.72) * mm, v(9.7, -1.72) * mm]});
            skFitSpline(sketch, "E230", {"points": [v(9.7, -1.72) * mm, v(9.68, -1.72) * mm, v(9.66, -1.72) * mm, v(9.65, -1.73) * mm]});
            skFitSpline(sketch, "E231", {"points": [v(9.65, -1.73) * mm, v(9.63, -1.74) * mm, v(9.62, -1.75) * mm, v(9.6, -1.76) * mm]});
            skFitSpline(sketch, "E232", {"points": [v(9.6, -1.76) * mm, v(9.6, -1.78) * mm, v(9.59, -1.8) * mm, v(9.58, -1.82) * mm]});
            skFitSpline(sketch, "E233", {"points": [v(9.58, -1.82) * mm, v(9.57, -1.87) * mm, v(9.58, -1.92) * mm, v(9.61, -1.95) * mm]});
            skFitSpline(sketch, "E234", {"points": [v(9.61, -1.95) * mm, v(9.64, -2) * mm, v(9.69, -2.02) * mm, v(9.75, -2.03) * mm]});
            skLineSegment(sketch, "E235", {"start": v(10.16, -1.8) * mm, "end": v(10.09, -1.79) * mm});
            skLineSegment(sketch, "E236", {"start": v(10.09, -1.79) * mm, "end": v(9.83, -1.74) * mm});
            skFitSpline(sketch, "E237", {"points": [v(10.1, -2.1) * mm, v(10.08, -2.2) * mm, v(10.06, -2.29) * mm, v(10.03, -2.37) * mm]});
            skLineSegment(sketch, "E238", {"start": v(9.75, -2.03) * mm, "end": v(10.1, -2.1) * mm});
            skFitSpline(sketch, "E239", {"points": [v(9.34, -2.2) * mm, v(9.36, -2.12) * mm, v(9.38, -2.04) * mm, v(9.4, -1.96) * mm]});
            skLineSegment(sketch, "E240", {"start": v(10.03, -2.37) * mm, "end": v(9.34, -2.2) * mm});
            skFitSpline(sketch, "E241", {"points": [v(9.5, -1.98) * mm, v(9.47, -1.93) * mm, v(9.45, -1.88) * mm, v(9.43, -1.84) * mm]});
            skFitSpline(sketch, "E242", {"points": [v(9.43, -1.84) * mm, v(9.42, -1.8) * mm, v(9.42, -1.74) * mm, v(9.43, -1.7) * mm]});
            skFitSpline(sketch, "E243", {"points": [v(9.43, -1.7) * mm, v(9.45, -1.6) * mm, v(9.49, -1.54) * mm, v(9.54, -1.5) * mm]});
            skFitSpline(sketch, "E244", {"points": [v(9.54, -1.5) * mm, v(9.6, -1.46) * mm, v(9.68, -1.45) * mm, v(9.77, -1.46) * mm]});
            skLineSegment(sketch, "E245", {"start": v(9.4, -1.96) * mm, "end": v(9.5, -1.98) * mm});
            skFitSpline(sketch, "E246", {"points": [v(9.53, -1.18) * mm, v(9.54, -1.1) * mm, v(9.55, -1.01) * mm, v(9.56, -0.93) * mm]});
            skFitSpline(sketch, "E247", {"points": [v(10.27, -1) * mm, v(10.26, -1.1) * mm, v(10.25, -1.18) * mm, v(10.24, -1.27) * mm]});
            skLineSegment(sketch, "E248", {"start": v(9.56, -0.93) * mm, "end": v(10.27, -1) * mm});
            skFitSpline(sketch, "E249", {"points": [v(9.26, -1.15) * mm, v(9.27, -1.06) * mm, v(9.28, -0.98) * mm, v(9.28, -0.9) * mm]});
            skLineSegment(sketch, "E250", {"start": v(10.24, -1.27) * mm, "end": v(9.53, -1.18) * mm});
            skFitSpline(sketch, "E251", {"points": [v(9.47, -0.92) * mm, v(9.46, -1) * mm, v(9.45, -1.09) * mm, v(9.44, -1.17) * mm]});
            skLineSegment(sketch, "E252", {"start": v(9.28, -0.9) * mm, "end": v(9.47, -0.92) * mm});
            skFitSpline(sketch, "E253", {"points": [v(9.3, -0.66) * mm, v(9.31, -0.58) * mm, v(9.32, -0.5) * mm, v(9.32, -0.41) * mm]});
            skLineSegment(sketch, "E254", {"start": v(9.44, -1.17) * mm, "end": v(9.26, -1.15) * mm});
            skFitSpline(sketch, "E255", {"points": [v(9.86, -0.44) * mm, v(9.78, -0.34) * mm, v(9.7, -0.23) * mm, v(9.6, -0.13) * mm]});
            skFitSpline(sketch, "E256", {"points": [v(9.6, -0.13) * mm, v(9.61, -0.08) * mm, v(9.61, -0.02) * mm, v(9.61, 0.03) * mm]});
            skFitSpline(sketch, "E257", {"points": [v(9.61, 0.03) * mm, v(9.61, 0.08) * mm, v(9.61, 0.12) * mm, v(9.6, 0.16) * mm]});
            skFitSpline(sketch, "E258", {"points": [v(9.6, 0.16) * mm, v(9.65, 0.12) * mm, v(9.68, 0.08) * mm, v(9.72, 0.03) * mm]});
            skFitSpline(sketch, "E259", {"points": [v(9.72, 0.03) * mm, v(9.8, -0.05) * mm, v(9.86, -0.14) * mm, v(9.93, -0.24) * mm]});
            skFitSpline(sketch, "E260", {"points": [v(9.93, -0.24) * mm, v(10.02, -0.15) * mm, v(10.1, -0.06) * mm, v(10.18, 0.03) * mm]});
            skFitSpline(sketch, "E261", {"points": [v(10.18, 0.03) * mm, v(10.23, 0.1) * mm, v(10.28, 0.15) * mm, v(10.32, 0.2) * mm]});
            skFitSpline(sketch, "E262", {"points": [v(10.32, 0.2) * mm, v(10.32, 0.15) * mm, v(10.33, 0.1) * mm, v(10.33, 0.03) * mm]});
            skFitSpline(sketch, "E263", {"points": [v(10.33, 0.03) * mm, v(10.33, -0.02) * mm, v(10.32, -0.07) * mm, v(10.32, -0.13) * mm]});
            skFitSpline(sketch, "E264", {"points": [v(10.32, -0.13) * mm, v(10.22, -0.24) * mm, v(10.12, -0.34) * mm, v(10.02, -0.45) * mm]});
            skLineSegment(sketch, "E265", {"start": v(9.32, -0.41) * mm, "end": v(9.86, -0.44) * mm});
            skFitSpline(sketch, "E266", {"points": [v(10.31, -0.46) * mm, v(10.3, -0.55) * mm, v(10.3, -0.65) * mm, v(10.3, -0.74) * mm]});
            skLineSegment(sketch, "E267", {"start": v(10.02, -0.45) * mm, "end": v(10.31, -0.46) * mm});
            skFitSpline(sketch, "E268", {"points": [v(9.98, 0.67) * mm, v(9.99, 0.62) * mm, v(10, 0.58) * mm, v(10.01, 0.55) * mm]});
            skFitSpline(sketch, "E269", {"points": [v(10.01, 0.55) * mm, v(10.03, 0.52) * mm, v(10.06, 0.51) * mm, v(10.09, 0.51) * mm]});
            skFitSpline(sketch, "E270", {"points": [v(10.09, 0.51) * mm, v(10.12, 0.51) * mm, v(10.14, 0.53) * mm, v(10.15, 0.55) * mm]});
            skFitSpline(sketch, "E271", {"points": [v(10.15, 0.55) * mm, v(10.17, 0.57) * mm, v(10.18, 0.6) * mm, v(10.17, 0.65) * mm]});
            skFitSpline(sketch, "E272", {"points": [v(10.17, 0.65) * mm, v(10.17, 0.7) * mm, v(10.15, 0.74) * mm, v(10.12, 0.77) * mm]});
            skFitSpline(sketch, "E273", {"points": [v(10.12, 0.77) * mm, v(10.08, 0.8) * mm, v(10.04, 0.82) * mm, v(10, 0.81) * mm]});
            skLineSegment(sketch, "E274", {"start": v(10.3, -0.74) * mm, "end": v(9.3, -0.66) * mm});
            skFitSpline(sketch, "E275", {"points": [v(9.97, 0.81) * mm, v(9.98, 0.77) * mm, v(9.98, 0.72) * mm, v(9.98, 0.67) * mm]});
            skLineSegment(sketch, "E276", {"start": v(10, 0.81) * mm, "end": v(9.97, 0.81) * mm});
            skFitSpline(sketch, "E277", {"points": [v(10.27, 1.11) * mm, v(10.28, 1.02) * mm, v(10.28, 0.93) * mm, v(10.3, 0.84) * mm]});
            skLineSegment(sketch, "E278", {"start": v(9.86, 1.07) * mm, "end": v(10.27, 1.11) * mm});
            skFitSpline(sketch, "E279", {"points": [v(10.19, 0.83) * mm, v(10.23, 0.8) * mm, v(10.27, 0.76) * mm, v(10.3, 0.71) * mm]});
            skFitSpline(sketch, "E280", {"points": [v(10.3, 0.71) * mm, v(10.31, 0.67) * mm, v(10.33, 0.61) * mm, v(10.33, 0.55) * mm]});
            skFitSpline(sketch, "E281", {"points": [v(10.33, 0.55) * mm, v(10.33, 0.46) * mm, v(10.32, 0.38) * mm, v(10.27, 0.33) * mm]});
            skFitSpline(sketch, "E282", {"points": [v(10.27, 0.33) * mm, v(10.23, 0.27) * mm, v(10.18, 0.24) * mm, v(10.1, 0.24) * mm]});
            skFitSpline(sketch, "E283", {"points": [v(10.1, 0.24) * mm, v(10.02, 0.24) * mm, v(9.96, 0.27) * mm, v(9.92, 0.34) * mm]});
            skFitSpline(sketch, "E284", {"points": [v(9.92, 0.34) * mm, v(9.88, 0.4) * mm, v(9.86, 0.5) * mm, v(9.85, 0.65) * mm]});
            skFitSpline(sketch, "E285", {"points": [v(9.85, 0.65) * mm, v(9.84, 0.7) * mm, v(9.84, 0.75) * mm, v(9.84, 0.8) * mm]});
            skLineSegment(sketch, "E286", {"start": v(10.3, 0.84) * mm, "end": v(10.19, 0.83) * mm});
            skFitSpline(sketch, "E287", {"points": [v(9.82, 0.8) * mm, v(9.78, 0.8) * mm, v(9.76, 0.78) * mm, v(9.74, 0.74) * mm]});
            skFitSpline(sketch, "E288", {"points": [v(9.74, 0.74) * mm, v(9.73, 0.71) * mm, v(9.72, 0.66) * mm, v(9.73, 0.6) * mm]});
            skFitSpline(sketch, "E289", {"points": [v(9.73, 0.6) * mm, v(9.73, 0.54) * mm, v(9.74, 0.49) * mm, v(9.75, 0.44) * mm]});
            skFitSpline(sketch, "E290", {"points": [v(9.75, 0.44) * mm, v(9.76, 0.4) * mm, v(9.78, 0.35) * mm, v(9.8, 0.3) * mm]});
            skLineSegment(sketch, "E291", {"start": v(9.84, 0.8) * mm, "end": v(9.82, 0.8) * mm});
            skFitSpline(sketch, "E292", {"points": [v(9.63, 0.3) * mm, v(9.61, 0.36) * mm, v(9.6, 0.4) * mm, v(9.6, 0.46) * mm]});
            skFitSpline(sketch, "E293", {"points": [v(9.6, 0.46) * mm, v(9.58, 0.52) * mm, v(9.58, 0.57) * mm, v(9.57, 0.63) * mm]});
            skFitSpline(sketch, "E294", {"points": [v(9.57, 0.63) * mm, v(9.57, 0.77) * mm, v(9.58, 0.88) * mm, v(9.63, 0.95) * mm]});
            skFitSpline(sketch, "E295", {"points": [v(9.63, 0.95) * mm, v(9.67, 1.02) * mm, v(9.75, 1.06) * mm, v(9.86, 1.07) * mm]});
            skLineSegment(sketch, "E296", {"start": v(9.8, 0.3) * mm, "end": v(9.63, 0.3) * mm});
            skFitSpline(sketch, "E297", {"points": [v(9.62, 1.95) * mm, v(9.61, 1.91) * mm, v(9.6, 1.88) * mm, v(9.6, 1.84) * mm]});
            skFitSpline(sketch, "E298", {"points": [v(9.6, 1.84) * mm, v(9.6, 1.8) * mm, v(9.6, 1.76) * mm, v(9.6, 1.73) * mm]});
            skFitSpline(sketch, "E299", {"points": [v(9.6, 1.73) * mm, v(9.62, 1.66) * mm, v(9.64, 1.6) * mm, v(9.69, 1.57) * mm]});
            skFitSpline(sketch, "E300", {"points": [v(9.69, 1.57) * mm, v(9.73, 1.54) * mm, v(9.79, 1.52) * mm, v(9.85, 1.53) * mm]});
            skFitSpline(sketch, "E301", {"points": [v(9.85, 1.53) * mm, v(9.92, 1.54) * mm, v(9.97, 1.57) * mm, v(10, 1.62) * mm]});
            skFitSpline(sketch, "E302", {"points": [v(10, 1.62) * mm, v(10.03, 1.67) * mm, v(10.03, 1.73) * mm, v(10.02, 1.8) * mm]});
            skFitSpline(sketch, "E303", {"points": [v(10.02, 1.8) * mm, v(10.01, 1.84) * mm, v(10, 1.88) * mm, v(9.98, 1.92) * mm]});
            skFitSpline(sketch, "E304", {"points": [v(9.98, 1.92) * mm, v(9.97, 1.95) * mm, v(9.94, 1.98) * mm, v(9.92, 2.01) * mm]});
            skLineSegment(sketch, "E305", {"start": v(9.44, 1.92) * mm, "end": v(9.62, 1.95) * mm});
            skFitSpline(sketch, "E306", {"points": [v(10.1, 2.05) * mm, v(10.12, 2) * mm, v(10.14, 1.97) * mm, v(10.15, 1.93) * mm]});
            skFitSpline(sketch, "E307", {"points": [v(10.15, 1.93) * mm, v(10.17, 1.88) * mm, v(10.18, 1.84) * mm, v(10.19, 1.8) * mm]});
            skFitSpline(sketch, "E308", {"points": [v(10.19, 1.8) * mm, v(10.21, 1.64) * mm, v(10.2, 1.52) * mm, v(10.15, 1.42) * mm]});
            skFitSpline(sketch, "E309", {"points": [v(10.15, 1.42) * mm, v(10.1, 1.33) * mm, v(10, 1.27) * mm, v(9.9, 1.26) * mm]});
            skFitSpline(sketch, "E310", {"points": [v(9.9, 1.26) * mm, v(9.77, 1.24) * mm, v(9.68, 1.28) * mm, v(9.6, 1.35) * mm]});
            skFitSpline(sketch, "E311", {"points": [v(9.6, 1.35) * mm, v(9.52, 1.42) * mm, v(9.47, 1.52) * mm, v(9.45, 1.67) * mm]});
            skFitSpline(sketch, "E312", {"points": [v(9.45, 1.67) * mm, v(9.44, 1.7) * mm, v(9.44, 1.75) * mm, v(9.44, 1.79) * mm]});
            skFitSpline(sketch, "E313", {"points": [v(9.44, 1.79) * mm, v(9.44, 1.83) * mm, v(9.44, 1.87) * mm, v(9.44, 1.92) * mm]});
            skLineSegment(sketch, "E314", {"start": v(9.92, 2.01) * mm, "end": v(10.1, 2.05) * mm});
            skFitSpline(sketch, "E315", {"points": [v(9.4, 1.56) * mm, v(9.32, 1.49) * mm, v(9.25, 1.42) * mm, v(9.18, 1.35) * mm]});
            skFitSpline(sketch, "E316", {"points": [v(9.18, 1.35) * mm, v(9.18, 1.39) * mm, v(9.17, 1.43) * mm, v(9.16, 1.47) * mm]});
            skFitSpline(sketch, "E317", {"points": [v(9.16, 1.47) * mm, v(9.2, 1.52) * mm, v(9.25, 1.58) * mm, v(9.28, 1.63) * mm]});
            skFitSpline(sketch, "E318", {"points": [v(9.28, 1.63) * mm, v(9.23, 1.67) * mm, v(9.17, 1.7) * mm, v(9.12, 1.74) * mm]});
            skFitSpline(sketch, "E319", {"points": [v(9.12, 1.74) * mm, v(9.1, 1.78) * mm, v(9.1, 1.82) * mm, v(9.1, 1.86) * mm]});
            skFitSpline(sketch, "E320", {"points": [v(9.1, 1.86) * mm, v(9.18, 1.82) * mm, v(9.27, 1.78) * mm, v(9.36, 1.73) * mm]});
            skFitSpline(sketch, "E321", {"points": [v(9.36, 1.73) * mm, v(9.37, 1.67) * mm, v(9.38, 1.62) * mm, v(9.4, 1.56) * mm]});
            skFitSpline(sketch, "E322", {"points": [v(9.84, 3.12) * mm, v(9.87, 3.03) * mm, v(9.9, 2.94) * mm, v(9.92, 2.85) * mm]});
            skLineSegment(sketch, "E323", {"start": v(9.43, 2.99) * mm, "end": v(9.84, 3.12) * mm});
            skFitSpline(sketch, "E324", {"points": [v(9.6, 2.76) * mm, v(9.54, 2.75) * mm, v(9.5, 2.73) * mm, v(9.48, 2.72) * mm]});
            skFitSpline(sketch, "E325", {"points": [v(9.48, 2.72) * mm, v(9.46, 2.71) * mm, v(9.45, 2.7) * mm, v(9.44, 2.7) * mm]});
            skFitSpline(sketch, "E326", {"points": [v(9.44, 2.7) * mm, v(9.43, 2.68) * mm, v(9.42, 2.66) * mm, v(9.42, 2.64) * mm]});
            skFitSpline(sketch, "E327", {"points": [v(9.42, 2.64) * mm, v(9.41, 2.62) * mm, v(9.41, 2.6) * mm, v(9.42, 2.58) * mm]});
            skFitSpline(sketch, "E328", {"points": [v(9.42, 2.58) * mm, v(9.43, 2.53) * mm, v(9.46, 2.5) * mm, v(9.5, 2.47) * mm]});
            skFitSpline(sketch, "E329", {"points": [v(9.5, 2.47) * mm, v(9.55, 2.45) * mm, v(9.6, 2.45) * mm, v(9.67, 2.47) * mm]});
            skLineSegment(sketch, "E330", {"start": v(9.92, 2.85) * mm, "end": v(9.86, 2.84) * mm});
            skLineSegment(sketch, "E331", {"start": v(9.86, 2.84) * mm, "end": v(9.6, 2.76) * mm});
            skFitSpline(sketch, "E332", {"points": [v(10, 2.55) * mm, v(10.03, 2.46) * mm, v(10.05, 2.38) * mm, v(10.07, 2.29) * mm]});
            skLineSegment(sketch, "E333", {"start": v(9.67, 2.47) * mm, "end": v(10, 2.55) * mm});
            skFitSpline(sketch, "E334", {"points": [v(9.37, 2.13) * mm, v(9.35, 2.21) * mm, v(9.33, 2.3) * mm, v(9.31, 2.38) * mm]});
            skLineSegment(sketch, "E335", {"start": v(10.07, 2.29) * mm, "end": v(9.37, 2.13) * mm});
            skFitSpline(sketch, "E336", {"points": [v(9.42, 2.4) * mm, v(9.37, 2.43) * mm, v(9.33, 2.46) * mm, v(9.3, 2.5) * mm]});
            skFitSpline(sketch, "E337", {"points": [v(9.3, 2.5) * mm, v(9.26, 2.54) * mm, v(9.24, 2.58) * mm, v(9.23, 2.63) * mm]});
            skFitSpline(sketch, "E338", {"points": [v(9.23, 2.63) * mm, v(9.2, 2.72) * mm, v(9.2, 2.8) * mm, v(9.24, 2.85) * mm]});
            skFitSpline(sketch, "E339", {"points": [v(9.24, 2.85) * mm, v(9.27, 2.91) * mm, v(9.34, 2.96) * mm, v(9.43, 2.99) * mm]});
            skFitSpline(sketch, "E340", {"points": [v(9.43, 2.99) * mm, v(9.43, 2.99) * mm, v(9.43, 2.99) * mm, v(9.43, 2.99) * mm, v(9.43, 2.99) * mm]});
            skLineSegment(sketch, "E341", {"start": v(9.31, 2.38) * mm, "end": v(9.42, 2.4) * mm});
            skFitSpline(sketch, "E342", {"points": [v(9.09, 3.13) * mm, v(9.06, 3.21) * mm, v(9.03, 3.3) * mm, v(9, 3.37) * mm]});
            skFitSpline(sketch, "E343", {"points": [v(9.67, 3.62) * mm, v(9.7, 3.53) * mm, v(9.73, 3.45) * mm, v(9.76, 3.36) * mm]});
            skLineSegment(sketch, "E344", {"start": v(9, 3.37) * mm, "end": v(9.67, 3.62) * mm});
            skFitSpline(sketch, "E345", {"points": [v(8.7, 3.24) * mm, v(8.68, 3.3) * mm, v(8.65, 3.37) * mm, v(8.63, 3.43) * mm]});
            skFitSpline(sketch, "E346", {"points": [v(8.63, 3.43) * mm, v(8.73, 3.38) * mm, v(8.84, 3.32) * mm, v(8.94, 3.27) * mm]});
            skFitSpline(sketch, "E347", {"points": [v(8.94, 3.27) * mm, v(8.96, 3.23) * mm, v(8.97, 3.18) * mm, v(9, 3.14) * mm]});
            skFitSpline(sketch, "E348", {"points": [v(9, 3.14) * mm, v(8.9, 3.18) * mm, v(8.8, 3.21) * mm, v(8.7, 3.24) * mm]});
            skLineSegment(sketch, "E349", {"start": v(9.76, 3.36) * mm, "end": v(9.09, 3.13) * mm});
            skFitSpline(sketch, "E350", {"points": [v(8.84, 4.28) * mm, v(8.84, 4.24) * mm, v(8.84, 4.2) * mm, v(8.84, 4.17) * mm]});
            skFitSpline(sketch, "E351", {"points": [v(8.84, 4.17) * mm, v(8.85, 4.13) * mm, v(8.86, 4.1) * mm, v(8.88, 4.06) * mm]});
            skFitSpline(sketch, "E352", {"points": [v(8.88, 4.06) * mm, v(8.9, 4) * mm, v(8.95, 3.95) * mm, v(9, 3.93) * mm]});
            skFitSpline(sketch, "E353", {"points": [v(9, 3.93) * mm, v(9.05, 3.9) * mm, v(9.1, 3.9) * mm, v(9.16, 3.93) * mm]});
            skFitSpline(sketch, "E354", {"points": [v(9.16, 3.93) * mm, v(9.23, 3.96) * mm, v(9.27, 4) * mm, v(9.28, 4.05) * mm]});
            skFitSpline(sketch, "E355", {"points": [v(9.28, 4.05) * mm, v(9.3, 4.1) * mm, v(9.3, 4.17) * mm, v(9.26, 4.24) * mm]});
            skFitSpline(sketch, "E356", {"points": [v(9.26, 4.24) * mm, v(9.25, 4.27) * mm, v(9.22, 4.3) * mm, v(9.2, 4.34) * mm]});
            skFitSpline(sketch, "E357", {"points": [v(9.2, 4.34) * mm, v(9.17, 4.37) * mm, v(9.14, 4.4) * mm, v(9.11, 4.41) * mm]});
            skLineSegment(sketch, "E358", {"start": v(8.67, 4.2) * mm, "end": v(8.84, 4.28) * mm});
            skFitSpline(sketch, "E359", {"points": [v(9.28, 4.5) * mm, v(9.3, 4.46) * mm, v(9.34, 4.43) * mm, v(9.36, 4.39) * mm]});
            skFitSpline(sketch, "E360", {"points": [v(9.36, 4.39) * mm, v(9.39, 4.35) * mm, v(9.4, 4.31) * mm, v(9.43, 4.27) * mm]});
            skFitSpline(sketch, "E361", {"points": [v(9.43, 4.27) * mm, v(9.49, 4.13) * mm, v(9.5, 4) * mm, v(9.48, 3.9) * mm]});
            skFitSpline(sketch, "E362", {"points": [v(9.48, 3.9) * mm, v(9.45, 3.8) * mm, v(9.38, 3.72) * mm, v(9.27, 3.68) * mm]});
            skFitSpline(sketch, "E363", {"points": [v(9.27, 3.68) * mm, v(9.16, 3.63) * mm, v(9.06, 3.64) * mm, v(8.97, 3.7) * mm]});
            skFitSpline(sketch, "E364", {"points": [v(8.97, 3.7) * mm, v(8.87, 3.74) * mm, v(8.8, 3.83) * mm, v(8.74, 3.96) * mm]});
            skFitSpline(sketch, "E365", {"points": [v(8.74, 3.96) * mm, v(8.72, 4) * mm, v(8.71, 4.04) * mm, v(8.7, 4.08) * mm]});
            skFitSpline(sketch, "E366", {"points": [v(8.7, 4.08) * mm, v(8.69, 4.12) * mm, v(8.68, 4.16) * mm, v(8.67, 4.2) * mm]});
            skLineSegment(sketch, "E367", {"start": v(9.11, 4.41) * mm, "end": v(9.28, 4.5) * mm});
            skFitSpline(sketch, "E368", {"points": [v(8.77, 5.47) * mm, v(8.82, 5.4) * mm, v(8.87, 5.31) * mm, v(8.91, 5.23) * mm]});
            skLineSegment(sketch, "E369", {"start": v(8.4, 5.24) * mm, "end": v(8.77, 5.47) * mm});
            skFitSpline(sketch, "E370", {"points": [v(8.63, 5.07) * mm, v(8.57, 5.03) * mm, v(8.54, 5.01) * mm, v(8.52, 5) * mm]});
            skFitSpline(sketch, "E371", {"points": [v(8.52, 5) * mm, v(8.5, 4.98) * mm, v(8.49, 4.97) * mm, v(8.48, 4.96) * mm]});
            skFitSpline(sketch, "E372", {"points": [v(8.48, 4.96) * mm, v(8.47, 4.94) * mm, v(8.47, 4.92) * mm, v(8.47, 4.9) * mm]});
            skFitSpline(sketch, "E373", {"points": [v(8.47, 4.9) * mm, v(8.47, 4.88) * mm, v(8.48, 4.87) * mm, v(8.49, 4.85) * mm]});
            skFitSpline(sketch, "E374", {"points": [v(8.49, 4.85) * mm, v(8.52, 4.8) * mm, v(8.55, 4.77) * mm, v(8.6, 4.76) * mm]});
            skFitSpline(sketch, "E375", {"points": [v(8.6, 4.76) * mm, v(8.65, 4.75) * mm, v(8.7, 4.76) * mm, v(8.76, 4.8) * mm]});
            skLineSegment(sketch, "E376", {"start": v(8.91, 5.23) * mm, "end": v(8.85, 5.2) * mm});
            skLineSegment(sketch, "E377", {"start": v(8.85, 5.2) * mm, "end": v(8.63, 5.07) * mm});
            skFitSpline(sketch, "E378", {"points": [v(9.07, 4.96) * mm, v(9.1, 4.88) * mm, v(9.15, 4.8) * mm, v(9.2, 4.72) * mm]});
            skLineSegment(sketch, "E379", {"start": v(8.76, 4.8) * mm, "end": v(9.07, 4.96) * mm});
            skFitSpline(sketch, "E380", {"points": [v(8.3, 4.27) * mm, v(8.27, 4.34) * mm, v(8.23, 4.41) * mm, v(8.2, 4.49) * mm]});
            skLineSegment(sketch, "E381", {"start": v(9.2, 4.72) * mm, "end": v(8.3, 4.27) * mm});
            skFitSpline(sketch, "E382", {"points": [v(8.53, 4.67) * mm, v(8.47, 4.68) * mm, v(8.43, 4.7) * mm, v(8.39, 4.73) * mm]});
            skFitSpline(sketch, "E383", {"points": [v(8.39, 4.73) * mm, v(8.35, 4.76) * mm, v(8.32, 4.8) * mm, v(8.3, 4.84) * mm]});
            skFitSpline(sketch, "E384", {"points": [v(8.3, 4.84) * mm, v(8.25, 4.92) * mm, v(8.23, 5) * mm, v(8.25, 5.06) * mm]});
            skFitSpline(sketch, "E385", {"points": [v(8.25, 5.06) * mm, v(8.27, 5.13) * mm, v(8.32, 5.2) * mm, v(8.4, 5.24) * mm]});
            skLineSegment(sketch, "E386", {"start": v(8.2, 4.49) * mm, "end": v(8.53, 4.67) * mm});
            skFitSpline(sketch, "E387", {"points": [v(7.84, 6.24) * mm, v(7.87, 6.2) * mm, v(7.9, 6.17) * mm, v(7.94, 6.16) * mm]});
            skFitSpline(sketch, "E388", {"points": [v(7.94, 6.16) * mm, v(7.97, 6.15) * mm, v(8, 6.15) * mm, v(8.02, 6.17) * mm]});
            skFitSpline(sketch, "E389", {"points": [v(8.02, 6.17) * mm, v(8.04, 6.19) * mm, v(8.05, 6.2) * mm, v(8.05, 6.24) * mm]});
            skFitSpline(sketch, "E390", {"points": [v(8.05, 6.24) * mm, v(8.05, 6.27) * mm, v(8.04, 6.3) * mm, v(8.01, 6.33) * mm]});
            skFitSpline(sketch, "E391", {"points": [v(8.01, 6.33) * mm, v(7.98, 6.37) * mm, v(7.94, 6.4) * mm, v(7.9, 6.4) * mm]});
            skFitSpline(sketch, "E392", {"points": [v(7.9, 6.4) * mm, v(7.85, 6.4) * mm, v(7.81, 6.4) * mm, v(7.77, 6.37) * mm]});
            skFitSpline(sketch, "E393", {"points": [v(7.75, 6.35) * mm, v(7.78, 6.32) * mm, v(7.81, 6.28) * mm, v(7.84, 6.24) * mm]});
            skLineSegment(sketch, "E394", {"start": v(7.77, 6.37) * mm, "end": v(7.75, 6.35) * mm});
            skFitSpline(sketch, "E395", {"points": [v(7.83, 6.77) * mm, v(7.89, 6.7) * mm, v(7.95, 6.63) * mm, v(8, 6.55) * mm]});
            skLineSegment(sketch, "E396", {"start": v(7.52, 6.5) * mm, "end": v(7.83, 6.77) * mm});
            skFitSpline(sketch, "E397", {"points": [v(7.92, 6.49) * mm, v(7.98, 6.49) * mm, v(8.03, 6.47) * mm, v(8.07, 6.45) * mm]});
            skFitSpline(sketch, "E398", {"points": [v(8.07, 6.45) * mm, v(8.12, 6.43) * mm, v(8.16, 6.39) * mm, v(8.2, 6.34) * mm]});
            skFitSpline(sketch, "E399", {"points": [v(8.2, 6.34) * mm, v(8.25, 6.26) * mm, v(8.28, 6.2) * mm, v(8.28, 6.12) * mm]});
            skFitSpline(sketch, "E400", {"points": [v(8.28, 6.12) * mm, v(8.27, 6.05) * mm, v(8.24, 6) * mm, v(8.19, 5.96) * mm]});
            skFitSpline(sketch, "E401", {"points": [v(8.19, 5.96) * mm, v(8.12, 5.9) * mm, v(8.05, 5.9) * mm, v(7.98, 5.93) * mm]});
            skFitSpline(sketch, "E402", {"points": [v(7.98, 5.93) * mm, v(7.9, 5.96) * mm, v(7.83, 6.03) * mm, v(7.75, 6.15) * mm]});
            skFitSpline(sketch, "E403", {"points": [v(7.75, 6.15) * mm, v(7.71, 6.19) * mm, v(7.68, 6.23) * mm, v(7.65, 6.27) * mm]});
            skLineSegment(sketch, "E404", {"start": v(8, 6.55) * mm, "end": v(7.92, 6.49) * mm});
            skFitSpline(sketch, "E405", {"points": [v(7.63, 6.26) * mm, v(7.6, 6.23) * mm, v(7.6, 6.2) * mm, v(7.6, 6.17) * mm]});
            skFitSpline(sketch, "E406", {"points": [v(7.6, 6.17) * mm, v(7.61, 6.13) * mm, v(7.64, 6.09) * mm, v(7.68, 6.03) * mm]});
            skFitSpline(sketch, "E407", {"points": [v(7.68, 6.03) * mm, v(7.71, 5.99) * mm, v(7.75, 5.95) * mm, v(7.78, 5.92) * mm]});
            skFitSpline(sketch, "E408", {"points": [v(7.78, 5.92) * mm, v(7.82, 5.89) * mm, v(7.86, 5.86) * mm, v(7.9, 5.84) * mm]});
            skLineSegment(sketch, "E409", {"start": v(7.65, 6.27) * mm, "end": v(7.63, 6.26) * mm});
            skFitSpline(sketch, "E410", {"points": [v(7.76, 5.73) * mm, v(7.72, 5.77) * mm, v(7.68, 5.81) * mm, v(7.64, 5.85) * mm]});
            skFitSpline(sketch, "E411", {"points": [v(7.64, 5.85) * mm, v(7.6, 5.9) * mm, v(7.56, 5.93) * mm, v(7.53, 5.98) * mm]});
            skFitSpline(sketch, "E412", {"points": [v(7.53, 5.98) * mm, v(7.44, 6.09) * mm, v(7.4, 6.19) * mm, v(7.4, 6.27) * mm]});
            skFitSpline(sketch, "E413", {"points": [v(7.4, 6.27) * mm, v(7.39, 6.35) * mm, v(7.43, 6.43) * mm, v(7.52, 6.5) * mm]});
            skLineSegment(sketch, "E414", {"start": v(7.9, 5.84) * mm, "end": v(7.76, 5.73) * mm});
            skFitSpline(sketch, "E415", {"points": [v(6.78, 6.85) * mm, v(6.72, 6.9) * mm, v(6.66, 6.97) * mm, v(6.6, 7.03) * mm]});
            skFitSpline(sketch, "E416", {"points": [v(7.08, 7.55) * mm, v(7.15, 7.49) * mm, v(7.22, 7.42) * mm, v(7.28, 7.36) * mm]});
            skLineSegment(sketch, "E417", {"start": v(6.6, 7.03) * mm, "end": v(7.08, 7.55) * mm});
            skFitSpline(sketch, "E418", {"points": [v(6.58, 6.65) * mm, v(6.52, 6.71) * mm, v(6.46, 6.77) * mm, v(6.4, 6.82) * mm]});
            skLineSegment(sketch, "E419", {"start": v(7.28, 7.36) * mm, "end": v(6.78, 6.85) * mm});
            skFitSpline(sketch, "E420", {"points": [v(6.53, 6.96) * mm, v(6.6, 6.9) * mm, v(6.65, 6.84) * mm, v(6.71, 6.78) * mm]});
            skLineSegment(sketch, "E421", {"start": v(6.4, 6.82) * mm, "end": v(6.53, 6.96) * mm});
            skLineSegment(sketch, "E422", {"start": v(6.71, 6.78) * mm, "end": v(6.58, 6.65) * mm});
            skFitSpline(sketch, "E423", {"points": [v(6.22, 8.27) * mm, v(6.3, 8.22) * mm, v(6.36, 8.16) * mm, v(6.44, 8.1) * mm]});
            skLineSegment(sketch, "E424", {"start": v(5.96, 7.93) * mm, "end": v(6.22, 8.27) * mm});
            skFitSpline(sketch, "E425", {"points": [v(6.23, 7.84) * mm, v(6.2, 7.8) * mm, v(6.17, 7.76) * mm, v(6.15, 7.74) * mm]});
            skFitSpline(sketch, "E426", {"points": [v(6.15, 7.74) * mm, v(6.14, 7.72) * mm, v(6.14, 7.7) * mm, v(6.14, 7.7) * mm]});
            skFitSpline(sketch, "E427", {"points": [v(6.14, 7.7) * mm, v(6.13, 7.67) * mm, v(6.14, 7.66) * mm, v(6.15, 7.64) * mm]});
            skFitSpline(sketch, "E428", {"points": [v(6.15, 7.64) * mm, v(6.15, 7.62) * mm, v(6.17, 7.6) * mm, v(6.18, 7.6) * mm]});
            skFitSpline(sketch, "E429", {"points": [v(6.18, 7.6) * mm, v(6.23, 7.56) * mm, v(6.27, 7.54) * mm, v(6.32, 7.55) * mm]});
            skFitSpline(sketch, "E430", {"points": [v(6.32, 7.55) * mm, v(6.37, 7.56) * mm, v(6.41, 7.59) * mm, v(6.45, 7.64) * mm]});
            skLineSegment(sketch, "E431", {"start": v(6.44, 8.1) * mm, "end": v(6.4, 8.05) * mm});
            skLineSegment(sketch, "E432", {"start": v(6.4, 8.05) * mm, "end": v(6.23, 7.84) * mm});
            skFitSpline(sketch, "E433", {"points": [v(6.68, 7.9) * mm, v(6.75, 7.85) * mm, v(6.82, 7.79) * mm, v(6.89, 7.73) * mm]});
            skLineSegment(sketch, "E434", {"start": v(6.45, 7.64) * mm, "end": v(6.68, 7.9) * mm});
            skFitSpline(sketch, "E435", {"points": [v(6.41, 7.2) * mm, v(6.35, 7.25) * mm, v(6.28, 7.3) * mm, v(6.22, 7.36) * mm]});
            skLineSegment(sketch, "E436", {"start": v(6.89, 7.73) * mm, "end": v(6.41, 7.2) * mm});
            skFitSpline(sketch, "E437", {"points": [v(6.29, 7.44) * mm, v(6.23, 7.43) * mm, v(6.18, 7.44) * mm, v(6.13, 7.45) * mm]});
            skFitSpline(sketch, "E438", {"points": [v(6.13, 7.45) * mm, v(6.09, 7.46) * mm, v(6.04, 7.48) * mm, v(6, 7.52) * mm]});
            skFitSpline(sketch, "E439", {"points": [v(6, 7.52) * mm, v(5.93, 7.57) * mm, v(5.9, 7.64) * mm, v(5.88, 7.7) * mm]});
            skFitSpline(sketch, "E440", {"points": [v(5.88, 7.7) * mm, v(5.87, 7.78) * mm, v(5.9, 7.85) * mm, v(5.96, 7.93) * mm]});
            skFitSpline(sketch, "E441", {"points": [v(5.96, 7.93) * mm, v(5.96, 7.93) * mm, v(5.96, 7.93) * mm, v(5.96, 7.93) * mm, v(5.96, 7.93) * mm]});
            skLineSegment(sketch, "E442", {"start": v(6.22, 7.36) * mm, "end": v(6.29, 7.44) * mm});
            skFitSpline(sketch, "E443", {"points": [v(5.1, 8.03) * mm, v(5.13, 8) * mm, v(5.17, 7.98) * mm, v(5.2, 7.95) * mm]});
            skFitSpline(sketch, "E444", {"points": [v(5.2, 7.95) * mm, v(5.24, 7.93) * mm, v(5.26, 7.92) * mm, v(5.28, 7.93) * mm]});
            skFitSpline(sketch, "E445", {"points": [v(5.28, 7.93) * mm, v(5.3, 7.93) * mm, v(5.32, 7.94) * mm, v(5.33, 7.96) * mm]});
            skLineSegment(sketch, "E446", {"start": v(5.01, 7.9) * mm, "end": v(5.1, 8.03) * mm});
            skFitSpline(sketch, "E447", {"points": [v(5.36, 8) * mm, v(5.3, 8.05) * mm, v(5.24, 8.09) * mm, v(5.18, 8.13) * mm]});
            skLineSegment(sketch, "E448", {"start": v(5.33, 7.96) * mm, "end": v(5.36, 8) * mm});
            skFitSpline(sketch, "E449", {"points": [v(5.26, 8.26) * mm, v(5.33, 8.22) * mm, v(5.39, 8.18) * mm, v(5.45, 8.14) * mm]});
            skLineSegment(sketch, "E450", {"start": v(5.18, 8.13) * mm, "end": v(5.26, 8.26) * mm});
            skFitSpline(sketch, "E451", {"points": [v(5.76, 8.6) * mm, v(5.83, 8.55) * mm, v(5.9, 8.5) * mm, v(5.98, 8.44) * mm]});
            skLineSegment(sketch, "E452", {"start": v(5.45, 8.14) * mm, "end": v(5.76, 8.6) * mm});
            skFitSpline(sketch, "E453", {"points": [v(5.66, 8) * mm, v(5.7, 7.97) * mm, v(5.74, 7.95) * mm, v(5.77, 7.92) * mm]});
            skLineSegment(sketch, "E454", {"start": v(5.98, 8.44) * mm, "end": v(5.66, 8) * mm});
            skFitSpline(sketch, "E455", {"points": [v(5.67, 7.79) * mm, v(5.64, 7.81) * mm, v(5.6, 7.84) * mm, v(5.57, 7.86) * mm]});
            skLineSegment(sketch, "E456", {"start": v(5.77, 7.92) * mm, "end": v(5.67, 7.79) * mm});
            skFitSpline(sketch, "E457", {"points": [v(5.54, 7.82) * mm, v(5.5, 7.76) * mm, v(5.44, 7.72) * mm, v(5.38, 7.72) * mm]});
            skFitSpline(sketch, "E458", {"points": [v(5.38, 7.72) * mm, v(5.32, 7.72) * mm, v(5.25, 7.74) * mm, v(5.17, 7.8) * mm]});
            skFitSpline(sketch, "E459", {"points": [v(5.17, 7.8) * mm, v(5.12, 7.83) * mm, v(5.07, 7.87) * mm, v(5.01, 7.9) * mm]});
            skLineSegment(sketch, "E460", {"start": v(5.57, 7.86) * mm, "end": v(5.54, 7.82) * mm});
            skFitSpline(sketch, "E461", {"points": [v(4.81, 8.52) * mm, v(4.86, 8.49) * mm, v(4.9, 8.48) * mm, v(4.95, 8.5) * mm]});
            skFitSpline(sketch, "E462", {"points": [v(4.95, 8.5) * mm, v(5, 8.51) * mm, v(5.04, 8.55) * mm, v(5.07, 8.6) * mm]});
            skFitSpline(sketch, "E463", {"points": [v(5.07, 8.6) * mm, v(5.1, 8.67) * mm, v(5.12, 8.72) * mm, v(5.11, 8.77) * mm]});
            skFitSpline(sketch, "E464", {"points": [v(5.11, 8.77) * mm, v(5.1, 8.82) * mm, v(5.07, 8.85) * mm, v(5.02, 8.88) * mm]});
            skFitSpline(sketch, "E465", {"points": [v(5.02, 8.88) * mm, v(4.97, 8.91) * mm, v(4.92, 8.92) * mm, v(4.87, 8.9) * mm]});
            skFitSpline(sketch, "E466", {"points": [v(4.87, 8.9) * mm, v(4.83, 8.89) * mm, v(4.8, 8.85) * mm, v(4.76, 8.79) * mm]});
            skFitSpline(sketch, "E467", {"points": [v(4.76, 8.79) * mm, v(4.73, 8.73) * mm, v(4.71, 8.67) * mm, v(4.72, 8.63) * mm]});
            skFitSpline(sketch, "E468", {"points": [v(4.72, 8.63) * mm, v(4.73, 8.58) * mm, v(4.76, 8.54) * mm, v(4.81, 8.52) * mm]});
            skFitSpline(sketch, "E469", {"points": [v(4.73, 8.37) * mm, v(4.61, 8.44) * mm, v(4.53, 8.52) * mm, v(4.5, 8.61) * mm]});
            skFitSpline(sketch, "E470", {"points": [v(4.5, 8.61) * mm, v(4.45, 8.7) * mm, v(4.46, 8.8) * mm, v(4.51, 8.91) * mm]});
            skFitSpline(sketch, "E471", {"points": [v(4.51, 8.91) * mm, v(4.57, 9.02) * mm, v(4.64, 9.08) * mm, v(4.75, 9.1) * mm]});
            skFitSpline(sketch, "E472", {"points": [v(4.75, 9.1) * mm, v(4.85, 9.12) * mm, v(4.97, 9.1) * mm, v(5.1, 9.03) * mm]});
            skFitSpline(sketch, "E473", {"points": [v(5.1, 9.03) * mm, v(5.23, 8.95) * mm, v(5.31, 8.86) * mm, v(5.35, 8.77) * mm]});
            skFitSpline(sketch, "E474", {"points": [v(5.35, 8.77) * mm, v(5.38, 8.67) * mm, v(5.37, 8.57) * mm, v(5.3, 8.47) * mm]});
            skFitSpline(sketch, "E475", {"points": [v(5.3, 8.47) * mm, v(5.24, 8.37) * mm, v(5.16, 8.31) * mm, v(5.06, 8.3) * mm]});
            skFitSpline(sketch, "E476", {"points": [v(5.06, 8.3) * mm, v(4.96, 8.28) * mm, v(4.85, 8.3) * mm, v(4.73, 8.37) * mm]});
            skFitSpline(sketch, "E477", {"points": [v(3.72, 9.1) * mm, v(3.73, 9.08) * mm, v(3.75, 9.07) * mm, v(3.77, 9.05) * mm]});
            skFitSpline(sketch, "E478", {"points": [v(3.77, 9.05) * mm, v(3.79, 9.04) * mm, v(3.8, 9.03) * mm, v(3.83, 9.02) * mm]});
            skFitSpline(sketch, "E479", {"points": [v(3.83, 9.02) * mm, v(3.9, 9) * mm, v(3.95, 9) * mm, v(4, 9.01) * mm]});
            skFitSpline(sketch, "E480", {"points": [v(4, 9.01) * mm, v(4.04, 9.03) * mm, v(4.08, 9.07) * mm, v(4.11, 9.14) * mm]});
            skFitSpline(sketch, "E481", {"points": [v(4.25, 9.44) * mm, v(4.33, 9.4) * mm, v(4.41, 9.36) * mm, v(4.5, 9.32) * mm]});
            skLineSegment(sketch, "E482", {"start": v(4.11, 9.14) * mm, "end": v(4.25, 9.44) * mm});
            skFitSpline(sketch, "E483", {"points": [v(4.18, 8.68) * mm, v(4.1, 8.71) * mm, v(4.03, 8.75) * mm, v(3.95, 8.79) * mm]});
            skLineSegment(sketch, "E484", {"start": v(4.5, 9.32) * mm, "end": v(4.18, 8.68) * mm});
            skFitSpline(sketch, "E485", {"points": [v(4, 8.9) * mm, v(3.95, 8.86) * mm, v(3.9, 8.85) * mm, v(3.86, 8.85) * mm]});
            skFitSpline(sketch, "E486", {"points": [v(3.86, 8.85) * mm, v(3.8, 8.84) * mm, v(3.76, 8.85) * mm, v(3.7, 8.88) * mm]});
            skFitSpline(sketch, "E487", {"points": [v(3.7, 8.88) * mm, v(3.7, 8.88) * mm, v(3.69, 8.88) * mm, v(3.68, 8.89) * mm]});
            skFitSpline(sketch, "E488", {"points": [v(3.68, 8.89) * mm, v(3.67, 8.9) * mm, v(3.65, 8.9) * mm, v(3.64, 8.9) * mm]});
            skFitSpline(sketch, "E489", {"points": [v(3.64, 8.9) * mm, v(3.66, 8.97) * mm, v(3.69, 9.04) * mm, v(3.72, 9.1) * mm]});
            skLineSegment(sketch, "E490", {"start": v(3.95, 8.79) * mm, "end": v(4, 8.9) * mm});
            skFitSpline(sketch, "E491", {"points": [v(2.86, 9.33) * mm, v(2.81, 9.3) * mm, v(2.77, 9.27) * mm, v(2.72, 9.26) * mm]});
            skFitSpline(sketch, "E492", {"points": [v(2.72, 9.26) * mm, v(2.67, 9.25) * mm, v(2.62, 9.26) * mm, v(2.57, 9.27) * mm]});
            skFitSpline(sketch, "E493", {"points": [v(2.57, 9.27) * mm, v(2.48, 9.3) * mm, v(2.42, 9.34) * mm, v(2.38, 9.4) * mm]});
            skFitSpline(sketch, "E494", {"points": [v(2.38, 9.4) * mm, v(2.35, 9.46) * mm, v(2.34, 9.54) * mm, v(2.37, 9.63) * mm]});
            skFitSpline(sketch, "E495", {"points": [v(2.47, 10.05) * mm, v(2.56, 10.03) * mm, v(2.65, 10) * mm, v(2.74, 9.98) * mm]});
            skLineSegment(sketch, "E496", {"start": v(2.37, 9.63) * mm, "end": v(2.47, 10.05) * mm});
            skFitSpline(sketch, "E497", {"points": [v(2.64, 9.62) * mm, v(2.64, 9.62) * mm, v(2.64, 9.61) * mm, v(2.63, 9.6) * mm]});
            skFitSpline(sketch, "E498", {"points": [v(2.63, 9.6) * mm, v(2.63, 9.6) * mm, v(2.63, 9.6) * mm, v(2.63, 9.58) * mm]});
            skFitSpline(sketch, "E499", {"points": [v(2.63, 9.58) * mm, v(2.61, 9.53) * mm, v(2.61, 9.5) * mm, v(2.62, 9.47) * mm]});
            skFitSpline(sketch, "E500", {"points": [v(2.62, 9.47) * mm, v(2.63, 9.44) * mm, v(2.65, 9.43) * mm, v(2.7, 9.42) * mm]});
            skFitSpline(sketch, "E501", {"points": [v(2.7, 9.42) * mm, v(2.74, 9.4) * mm, v(2.78, 9.4) * mm, v(2.82, 9.43) * mm]});
            skFitSpline(sketch, "E502", {"points": [v(2.82, 9.43) * mm, v(2.85, 9.46) * mm, v(2.88, 9.5) * mm, v(2.9, 9.57) * mm]});
            skLineSegment(sketch, "E503", {"start": v(2.74, 9.98) * mm, "end": v(2.64, 9.62) * mm});
            skFitSpline(sketch, "E504", {"points": [v(3, 9.9) * mm, v(3.1, 9.88) * mm, v(3.18, 9.85) * mm, v(3.27, 9.82) * mm]});
            skLineSegment(sketch, "E505", {"start": v(2.9, 9.57) * mm, "end": v(3, 9.9) * mm});
            skFitSpline(sketch, "E506", {"points": [v(3.15, 9.47) * mm, v(3.12, 9.4) * mm, v(3.11, 9.34) * mm, v(3.12, 9.32) * mm]});
            skFitSpline(sketch, "E507", {"points": [v(3.12, 9.32) * mm, v(3.13, 9.29) * mm, v(3.15, 9.27) * mm, v(3.19, 9.26) * mm]});
            skFitSpline(sketch, "E508", {"points": [v(3.19, 9.26) * mm, v(3.24, 9.24) * mm, v(3.28, 9.24) * mm, v(3.32, 9.27) * mm]});
            skFitSpline(sketch, "E509", {"points": [v(3.32, 9.27) * mm, v(3.35, 9.3) * mm, v(3.39, 9.34) * mm, v(3.4, 9.4) * mm]});
            skLineSegment(sketch, "E510", {"start": v(3.27, 9.82) * mm, "end": v(3.15, 9.47) * mm});
            skFitSpline(sketch, "E511", {"points": [v(3.53, 9.73) * mm, v(3.61, 9.7) * mm, v(3.7, 9.67) * mm, v(3.79, 9.63) * mm]});
            skLineSegment(sketch, "E512", {"start": v(3.4, 9.4) * mm, "end": v(3.53, 9.73) * mm});
            skFitSpline(sketch, "E513", {"points": [v(3.52, 8.97) * mm, v(3.44, 9) * mm, v(3.36, 9.03) * mm, v(3.28, 9.06) * mm]});
            skLineSegment(sketch, "E514", {"start": v(3.79, 9.63) * mm, "end": v(3.52, 8.97) * mm});
            skFitSpline(sketch, "E515", {"points": [v(3.32, 9.16) * mm, v(3.28, 9.13) * mm, v(3.23, 9.11) * mm, v(3.19, 9.1) * mm]});
            skFitSpline(sketch, "E516", {"points": [v(3.19, 9.1) * mm, v(3.14, 9.1) * mm, v(3.1, 9.1) * mm, v(3.05, 9.12) * mm]});
            skFitSpline(sketch, "E517", {"points": [v(3.05, 9.12) * mm, v(3, 9.14) * mm, v(2.95, 9.17) * mm, v(2.92, 9.2) * mm]});
            skFitSpline(sketch, "E518", {"points": [v(2.92, 9.2) * mm, v(2.89, 9.24) * mm, v(2.87, 9.28) * mm, v(2.86, 9.33) * mm]});
            skFitSpline(sketch, "E519", {"points": [v(2.86, 9.33) * mm, v(2.86, 9.33) * mm, v(2.86, 9.33) * mm, v(2.86, 9.33) * mm]});
            skLineSegment(sketch, "E520", {"start": v(3.28, 9.06) * mm, "end": v(3.32, 9.16) * mm});
            skFitSpline(sketch, "E521", {"points": [v(1.79, 9.87) * mm, v(1.84, 9.86) * mm, v(1.88, 9.86) * mm, v(1.91, 9.87) * mm]});
            skFitSpline(sketch, "E522", {"points": [v(1.91, 9.87) * mm, v(1.94, 9.88) * mm, v(1.96, 9.9) * mm, v(1.97, 9.94) * mm]});
            skFitSpline(sketch, "E523", {"points": [v(1.97, 9.94) * mm, v(1.98, 9.96) * mm, v(1.97, 9.99) * mm, v(1.95, 10) * mm]});
            skFitSpline(sketch, "E524", {"points": [v(1.95, 10) * mm, v(1.93, 10.03) * mm, v(1.9, 10.04) * mm, v(1.86, 10.05) * mm]});
            skFitSpline(sketch, "E525", {"points": [v(1.86, 10.05) * mm, v(1.8, 10.06) * mm, v(1.76, 10.05) * mm, v(1.73, 10.03) * mm]});
            skFitSpline(sketch, "E526", {"points": [v(1.73, 10.03) * mm, v(1.69, 10) * mm, v(1.66, 9.97) * mm, v(1.65, 9.92) * mm]});
            skFitSpline(sketch, "E527", {"points": [v(1.65, 9.9) * mm, v(1.7, 9.9) * mm, v(1.74, 9.88) * mm, v(1.79, 9.87) * mm]});
            skLineSegment(sketch, "E528", {"start": v(1.65, 9.92) * mm, "end": v(1.65, 9.9) * mm});
            skFitSpline(sketch, "E529", {"points": [v(1.43, 10.26) * mm, v(1.52, 10.25) * mm, v(1.61, 10.23) * mm, v(1.7, 10.22) * mm]});
            skLineSegment(sketch, "E530", {"start": v(1.37, 9.86) * mm, "end": v(1.43, 10.26) * mm});
            skFitSpline(sketch, "E531", {"points": [v(1.69, 10.11) * mm, v(1.73, 10.15) * mm, v(1.78, 10.17) * mm, v(1.82, 10.18) * mm]});
            skFitSpline(sketch, "E532", {"points": [v(1.82, 10.18) * mm, v(1.87, 10.2) * mm, v(1.93, 10.2) * mm, v(2, 10.18) * mm]});
            skFitSpline(sketch, "E533", {"points": [v(2, 10.18) * mm, v(2.08, 10.16) * mm, v(2.15, 10.13) * mm, v(2.2, 10.07) * mm]});
            skFitSpline(sketch, "E534", {"points": [v(2.2, 10.07) * mm, v(2.24, 10.02) * mm, v(2.25, 9.96) * mm, v(2.24, 9.89) * mm]});
            skFitSpline(sketch, "E535", {"points": [v(2.24, 9.89) * mm, v(2.22, 9.8) * mm, v(2.17, 9.76) * mm, v(2.1, 9.73) * mm]});
            skFitSpline(sketch, "E536", {"points": [v(2.1, 9.73) * mm, v(2.02, 9.7) * mm, v(1.92, 9.71) * mm, v(1.78, 9.74) * mm]});
            skFitSpline(sketch, "E537", {"points": [v(1.78, 9.74) * mm, v(1.73, 9.75) * mm, v(1.68, 9.76) * mm, v(1.63, 9.76) * mm]});
            skLineSegment(sketch, "E538", {"start": v(1.7, 10.22) * mm, "end": v(1.69, 10.11) * mm});
            skFitSpline(sketch, "E539", {"points": [v(1.62, 9.75) * mm, v(1.62, 9.71) * mm, v(1.63, 9.68) * mm, v(1.66, 9.66) * mm]});
            skFitSpline(sketch, "E540", {"points": [v(1.66, 9.66) * mm, v(1.69, 9.64) * mm, v(1.74, 9.62) * mm, v(1.8, 9.6) * mm]});
            skFitSpline(sketch, "E541", {"points": [v(1.8, 9.6) * mm, v(1.86, 9.6) * mm, v(1.9, 9.6) * mm, v(1.96, 9.6) * mm]});
            skFitSpline(sketch, "E542", {"points": [v(1.96, 9.6) * mm, v(2, 9.6) * mm, v(2.05, 9.6) * mm, v(2.1, 9.6) * mm]});
            skLineSegment(sketch, "E543", {"start": v(1.63, 9.76) * mm, "end": v(1.62, 9.75) * mm});
            skFitSpline(sketch, "E544", {"points": [v(2.06, 9.44) * mm, v(2, 9.44) * mm, v(1.95, 9.44) * mm, v(1.9, 9.45) * mm]});
            skFitSpline(sketch, "E545", {"points": [v(1.9, 9.45) * mm, v(1.84, 9.45) * mm, v(1.78, 9.46) * mm, v(1.73, 9.47) * mm]});
            skFitSpline(sketch, "E546", {"points": [v(1.73, 9.47) * mm, v(1.59, 9.5) * mm, v(1.49, 9.54) * mm, v(1.43, 9.6) * mm]});
            skFitSpline(sketch, "E547", {"points": [v(1.43, 9.6) * mm, v(1.38, 9.66) * mm, v(1.36, 9.74) * mm, v(1.37, 9.86) * mm]});
            skFitSpline(sketch, "E548", {"points": [v(1.37, 9.86) * mm, v(1.37, 9.86) * mm, v(1.37, 9.86) * mm, v(1.37, 9.86) * mm, v(1.37, 9.86) * mm]});
            skLineSegment(sketch, "E549", {"start": v(2.1, 9.6) * mm, "end": v(2.06, 9.44) * mm});
            skFitSpline(sketch, "E550", {"points": [v(0.46, 9.84) * mm, v(0.5, 9.82) * mm, v(0.53, 9.8) * mm, v(0.56, 9.8) * mm]});
            skFitSpline(sketch, "E551", {"points": [v(0.56, 9.8) * mm, v(0.6, 9.78) * mm, v(0.63, 9.77) * mm, v(0.67, 9.77) * mm]});
            skFitSpline(sketch, "E552", {"points": [v(0.67, 9.77) * mm, v(0.74, 9.76) * mm, v(0.8, 9.78) * mm, v(0.85, 9.81) * mm]});
            skFitSpline(sketch, "E553", {"points": [v(0.85, 9.81) * mm, v(0.89, 9.84) * mm, v(0.92, 9.9) * mm, v(0.92, 9.96) * mm]});
            skFitSpline(sketch, "E554", {"points": [v(0.92, 9.96) * mm, v(0.93, 10.03) * mm, v(0.91, 10.08) * mm, v(0.87, 10.12) * mm]});
            skFitSpline(sketch, "E555", {"points": [v(0.87, 10.12) * mm, v(0.84, 10.16) * mm, v(0.78, 10.19) * mm, v(0.7, 10.2) * mm]});
            skFitSpline(sketch, "E556", {"points": [v(0.7, 10.2) * mm, v(0.66, 10.2) * mm, v(0.62, 10.2) * mm, v(0.58, 10.18) * mm]});
            skFitSpline(sketch, "E557", {"points": [v(0.58, 10.18) * mm, v(0.54, 10.18) * mm, v(0.5, 10.16) * mm, v(0.47, 10.14) * mm]});
            skLineSegment(sketch, "E558", {"start": v(0.45, 9.66) * mm, "end": v(0.46, 9.84) * mm});
            skFitSpline(sketch, "E559", {"points": [v(0.48, 10.33) * mm, v(0.53, 10.34) * mm, v(0.57, 10.35) * mm, v(0.62, 10.35) * mm]});
            skFitSpline(sketch, "E560", {"points": [v(0.62, 10.35) * mm, v(0.66, 10.35) * mm, v(0.7, 10.36) * mm, v(0.75, 10.35) * mm]});
            skFitSpline(sketch, "E561", {"points": [v(0.75, 10.35) * mm, v(0.9, 10.34) * mm, v(1.02, 10.3) * mm, v(1.1, 10.22) * mm]});
            skFitSpline(sketch, "E562", {"points": [v(1.1, 10.22) * mm, v(1.18, 10.14) * mm, v(1.21, 10.05) * mm, v(1.2, 9.93) * mm]});
            skFitSpline(sketch, "E563", {"points": [v(1.2, 9.93) * mm, v(1.18, 9.81) * mm, v(1.13, 9.73) * mm, v(1.04, 9.67) * mm]});
            skFitSpline(sketch, "E564", {"points": [v(1.04, 9.67) * mm, v(0.95, 9.61) * mm, v(0.84, 9.6) * mm, v(0.7, 9.6) * mm]});
            skFitSpline(sketch, "E565", {"points": [v(0.7, 9.6) * mm, v(0.65, 9.6) * mm, v(0.61, 9.61) * mm, v(0.57, 9.62) * mm]});
            skFitSpline(sketch, "E566", {"points": [v(0.57, 9.62) * mm, v(0.53, 9.63) * mm, v(0.5, 9.64) * mm, v(0.45, 9.66) * mm]});
            skFitSpline(sketch, "E567", {"points": [v(0.45, 9.66) * mm, v(0.45, 9.66) * mm, v(0.45, 9.66) * mm, v(0.45, 9.66) * mm, v(0.45, 9.66) * mm]});
            skLineSegment(sketch, "E568", {"start": v(0.47, 10.14) * mm, "end": v(0.48, 10.33) * mm});
            skFitSpline(sketch, "E569", {"points": [v(0.78, 9.52) * mm, v(0.83, 9.44) * mm, v(0.88, 9.35) * mm, v(0.93, 9.27) * mm]});
            skFitSpline(sketch, "E570", {"points": [v(0.93, 9.27) * mm, v(0.9, 9.27) * mm, v(0.85, 9.28) * mm, v(0.81, 9.28) * mm]});
            skFitSpline(sketch, "E571", {"points": [v(0.81, 9.28) * mm, v(0.77, 9.33) * mm, v(0.73, 9.38) * mm, v(0.69, 9.44) * mm]});
            skFitSpline(sketch, "E572", {"points": [v(0.69, 9.44) * mm, v(0.64, 9.4) * mm, v(0.59, 9.35) * mm, v(0.54, 9.3) * mm]});
            skFitSpline(sketch, "E573", {"points": [v(0.54, 9.3) * mm, v(0.5, 9.3) * mm, v(0.46, 9.3) * mm, v(0.42, 9.3) * mm]});
            skFitSpline(sketch, "E574", {"points": [v(0.42, 9.3) * mm, v(0.48, 9.38) * mm, v(0.54, 9.46) * mm, v(0.6, 9.54) * mm]});
            skFitSpline(sketch, "E575", {"points": [v(0.6, 9.54) * mm, v(0.67, 9.53) * mm, v(0.72, 9.53) * mm, v(0.78, 9.52) * mm]});
            skFitSpline(sketch, "E576", {"points": [v(-0.62, 10.34) * mm, v(-0.53, 10.35) * mm, v(-0.44, 10.35) * mm, v(-0.34, 10.36) * mm]});
            skLineSegment(sketch, "E577", {"start": v(-0.6, 9.9) * mm, "end": v(-0.62, 10.34) * mm});
            skFitSpline(sketch, "E578", {"points": [v(-0.33, 10.02) * mm, v(-0.33, 9.96) * mm, v(-0.33, 9.92) * mm, v(-0.32, 9.9) * mm]});
            skFitSpline(sketch, "E579", {"points": [v(-0.32, 9.9) * mm, v(-0.32, 9.87) * mm, v(-0.31, 9.86) * mm, v(-0.3, 9.84) * mm]});
            skFitSpline(sketch, "E580", {"points": [v(-0.3, 9.84) * mm, v(-0.3, 9.83) * mm, v(-0.28, 9.82) * mm, v(-0.26, 9.81) * mm]});
            skFitSpline(sketch, "E581", {"points": [v(-0.26, 9.81) * mm, v(-0.24, 9.8) * mm, v(-0.22, 9.8) * mm, v(-0.2, 9.8) * mm]});
            skFitSpline(sketch, "E582", {"points": [v(-0.2, 9.8) * mm, v(-0.15, 9.8) * mm, v(-0.1, 9.82) * mm, v(-0.08, 9.86) * mm]});
            skFitSpline(sketch, "E583", {"points": [v(-0.08, 9.86) * mm, v(-0.04, 9.9) * mm, v(-0.03, 9.95) * mm, v(-0.03, 10.01) * mm]});
            skLineSegment(sketch, "E584", {"start": v(-0.34, 10.36) * mm, "end": v(-0.34, 10.29) * mm});
            skLineSegment(sketch, "E585", {"start": v(-0.34, 10.29) * mm, "end": v(-0.33, 10.02) * mm});
            skFitSpline(sketch, "E586", {"points": [v(-0.03, 10.36) * mm, v(-0.02, 10.36) * mm, v(-0.01, 10.36) * mm, v(0, 10.36) * mm]});
            skFitSpline(sketch, "E587", {"points": [v(0, 10.36) * mm, v(0.08, 10.36) * mm, v(0.16, 10.36) * mm, v(0.25, 10.36) * mm]});
            skLineSegment(sketch, "E588", {"start": v(-0.03, 10.01) * mm, "end": v(-0.03, 10.36) * mm});
            skFitSpline(sketch, "E589", {"points": [v(0.23, 9.64) * mm, v(0.15, 9.65) * mm, v(0.07, 9.65) * mm, v(0, 9.65) * mm]});
            skFitSpline(sketch, "E590", {"points": [v(0, 9.65) * mm, v(-0.01, 9.65) * mm, v(-0.02, 9.65) * mm, v(-0.03, 9.65) * mm]});
            skLineSegment(sketch, "E591", {"start": v(0.25, 10.36) * mm, "end": v(0.23, 9.64) * mm});
            skFitSpline(sketch, "E592", {"points": [v(-0.03, 9.75) * mm, v(-0.07, 9.71) * mm, v(-0.1, 9.68) * mm, v(-0.15, 9.66) * mm]});
            skFitSpline(sketch, "E593", {"points": [v(-0.15, 9.66) * mm, v(-0.2, 9.64) * mm, v(-0.24, 9.63) * mm, v(-0.3, 9.63) * mm]});
            skFitSpline(sketch, "E594", {"points": [v(-0.3, 9.63) * mm, v(-0.39, 9.62) * mm, v(-0.46, 9.64) * mm, v(-0.5, 9.7) * mm]});
            skFitSpline(sketch, "E595", {"points": [v(-0.5, 9.7) * mm, v(-0.56, 9.74) * mm, v(-0.59, 9.81) * mm, v(-0.6, 9.9) * mm]});
            skFitSpline(sketch, "E596", {"points": [v(-0.6, 9.9) * mm, v(-0.6, 9.9) * mm, v(-0.6, 9.9) * mm, v(-0.6, 9.9) * mm, v(-0.6, 9.9) * mm]});
            skLineSegment(sketch, "E597", {"start": v(-0.03, 9.65) * mm, "end": v(-0.03, 9.75) * mm});
            skFitSpline(sketch, "E598", {"points": [v(-0.81, 9.61) * mm, v(-0.9, 9.6) * mm, v(-0.98, 9.6) * mm, v(-1.07, 9.59) * mm]});
            skFitSpline(sketch, "E599", {"points": [v(-1.15, 10.3) * mm, v(-1.06, 10.3) * mm, v(-0.97, 10.32) * mm, v(-0.88, 10.32) * mm]});
            skLineSegment(sketch, "E600", {"start": v(-1.07, 9.59) * mm, "end": v(-1.15, 10.3) * mm});
            skFitSpline(sketch, "E601", {"points": [v(-1.02, 9.26) * mm, v(-1.08, 9.25) * mm, v(-1.14, 9.24) * mm, v(-1.2, 9.24) * mm]});
            skFitSpline(sketch, "E602", {"points": [v(-1.2, 9.24) * mm, v(-1.14, 9.33) * mm, v(-1.06, 9.42) * mm, v(-0.98, 9.5) * mm]});
            skFitSpline(sketch, "E603", {"points": [v(-0.98, 9.5) * mm, v(-0.94, 9.5) * mm, v(-0.9, 9.51) * mm, v(-0.84, 9.52) * mm]});
            skFitSpline(sketch, "E604", {"points": [v(-0.84, 9.52) * mm, v(-0.9, 9.43) * mm, v(-0.96, 9.35) * mm, v(-1.02, 9.26) * mm]});
            skLineSegment(sketch, "E605", {"start": v(-0.88, 10.32) * mm, "end": v(-0.81, 9.61) * mm});
            skFitSpline(sketch, "E606", {"points": [v(-2, 9.65) * mm, v(-1.95, 9.63) * mm, v(-1.91, 9.63) * mm, v(-1.88, 9.62) * mm]});
            skFitSpline(sketch, "E607", {"points": [v(-1.88, 9.62) * mm, v(-1.84, 9.62) * mm, v(-1.8, 9.62) * mm, v(-1.77, 9.63) * mm]});
            skFitSpline(sketch, "E608", {"points": [v(-1.77, 9.63) * mm, v(-1.7, 9.64) * mm, v(-1.64, 9.67) * mm, v(-1.6, 9.71) * mm]});
            skFitSpline(sketch, "E609", {"points": [v(-1.6, 9.71) * mm, v(-1.57, 9.76) * mm, v(-1.56, 9.81) * mm, v(-1.57, 9.88) * mm]});
            skFitSpline(sketch, "E610", {"points": [v(-1.57, 9.88) * mm, v(-1.58, 9.94) * mm, v(-1.61, 10) * mm, v(-1.66, 10.02) * mm]});
            skFitSpline(sketch, "E611", {"points": [v(-1.66, 10.02) * mm, v(-1.7, 10.05) * mm, v(-1.77, 10.06) * mm, v(-1.84, 10.04) * mm]});
            skFitSpline(sketch, "E612", {"points": [v(-1.84, 10.04) * mm, v(-1.88, 10.04) * mm, v(-1.92, 10.02) * mm, v(-1.96, 10) * mm]});
            skFitSpline(sketch, "E613", {"points": [v(-1.96, 10) * mm, v(-2, 9.99) * mm, v(-2.02, 9.97) * mm, v(-2.05, 9.94) * mm]});
            skLineSegment(sketch, "E614", {"start": v(-1.95, 9.46) * mm, "end": v(-2, 9.65) * mm});
            skFitSpline(sketch, "E615", {"points": [v(-2.1, 10.12) * mm, v(-2.05, 10.14) * mm, v(-2.01, 10.16) * mm, v(-1.97, 10.18) * mm]});
            skFitSpline(sketch, "E616", {"points": [v(-1.97, 10.18) * mm, v(-1.93, 10.2) * mm, v(-1.88, 10.2) * mm, v(-1.84, 10.21) * mm]});
            skFitSpline(sketch, "E617", {"points": [v(-1.84, 10.21) * mm, v(-1.69, 10.24) * mm, v(-1.56, 10.23) * mm, v(-1.47, 10.17) * mm]});
            skFitSpline(sketch, "E618", {"points": [v(-1.47, 10.17) * mm, v(-1.37, 10.12) * mm, v(-1.32, 10.03) * mm, v(-1.3, 9.92) * mm]});
            skFitSpline(sketch, "E619", {"points": [v(-1.3, 9.92) * mm, v(-1.28, 9.8) * mm, v(-1.31, 9.7) * mm, v(-1.39, 9.63) * mm]});
            skFitSpline(sketch, "E620", {"points": [v(-1.39, 9.63) * mm, v(-1.46, 9.55) * mm, v(-1.56, 9.5) * mm, v(-1.7, 9.47) * mm]});
            skFitSpline(sketch, "E621", {"points": [v(-1.7, 9.47) * mm, v(-1.74, 9.47) * mm, v(-1.79, 9.46) * mm, v(-1.83, 9.46) * mm]});
            skFitSpline(sketch, "E622", {"points": [v(-1.83, 9.46) * mm, v(-1.87, 9.46) * mm, v(-1.9, 9.46) * mm, v(-1.95, 9.46) * mm]});
            skLineSegment(sketch, "E623", {"start": v(-2.05, 9.94) * mm, "end": v(-2.1, 10.12) * mm});
            skFitSpline(sketch, "E624", {"points": [v(-3.16, 9.86) * mm, v(-3.07, 9.89) * mm, v(-2.98, 9.91) * mm, v(-2.9, 9.94) * mm]});
            skLineSegment(sketch, "E625", {"start": v(-3.02, 9.44) * mm, "end": v(-3.16, 9.86) * mm});
            skFitSpline(sketch, "E626", {"points": [v(-2.8, 9.62) * mm, v(-2.78, 9.56) * mm, v(-2.77, 9.52) * mm, v(-2.76, 9.5) * mm]});
            skFitSpline(sketch, "E627", {"points": [v(-2.76, 9.5) * mm, v(-2.75, 9.48) * mm, v(-2.74, 9.46) * mm, v(-2.73, 9.45) * mm]});
            skFitSpline(sketch, "E628", {"points": [v(-2.73, 9.45) * mm, v(-2.72, 9.44) * mm, v(-2.7, 9.44) * mm, v(-2.68, 9.43) * mm]});
            skFitSpline(sketch, "E629", {"points": [v(-2.68, 9.43) * mm, v(-2.66, 9.43) * mm, v(-2.64, 9.43) * mm, v(-2.62, 9.44) * mm]});
            skFitSpline(sketch, "E630", {"points": [v(-2.62, 9.44) * mm, v(-2.57, 9.45) * mm, v(-2.53, 9.48) * mm, v(-2.51, 9.52) * mm]});
            skFitSpline(sketch, "E631", {"points": [v(-2.51, 9.52) * mm, v(-2.5, 9.57) * mm, v(-2.49, 9.62) * mm, v(-2.5, 9.68) * mm]});
            skLineSegment(sketch, "E632", {"start": v(-2.9, 9.94) * mm, "end": v(-2.88, 9.87) * mm});
            skLineSegment(sketch, "E633", {"start": v(-2.88, 9.87) * mm, "end": v(-2.8, 9.62) * mm});
            skFitSpline(sketch, "E634", {"points": [v(-2.6, 10.02) * mm, v(-2.5, 10.05) * mm, v(-2.42, 10.07) * mm, v(-2.33, 10.09) * mm]});
            skLineSegment(sketch, "E635", {"start": v(-2.5, 9.68) * mm, "end": v(-2.6, 10.02) * mm});
            skFitSpline(sketch, "E636", {"points": [v(-2.1, 9.12) * mm, v(-2.18, 9.1) * mm, v(-2.26, 9.09) * mm, v(-2.34, 9.06) * mm]});
            skLineSegment(sketch, "E637", {"start": v(-2.33, 10.09) * mm, "end": v(-2.1, 9.12) * mm});
            skFitSpline(sketch, "E638", {"points": [v(-2.44, 9.43) * mm, v(-2.47, 9.38) * mm, v(-2.5, 9.34) * mm, v(-2.53, 9.31) * mm]});
            skFitSpline(sketch, "E639", {"points": [v(-2.53, 9.31) * mm, v(-2.57, 9.28) * mm, v(-2.61, 9.26) * mm, v(-2.66, 9.25) * mm]});
            skFitSpline(sketch, "E640", {"points": [v(-2.66, 9.25) * mm, v(-2.75, 9.22) * mm, v(-2.83, 9.22) * mm, v(-2.89, 9.26) * mm]});
            skFitSpline(sketch, "E641", {"points": [v(-2.89, 9.26) * mm, v(-2.95, 9.3) * mm, v(-3, 9.35) * mm, v(-3.02, 9.44) * mm]});
            skFitSpline(sketch, "E642", {"points": [v(-3.02, 9.44) * mm, v(-3.02, 9.44) * mm, v(-3.02, 9.44) * mm, v(-3.02, 9.44) * mm, v(-3.02, 9.44) * mm]});
            skLineSegment(sketch, "E643", {"start": v(-2.34, 9.06) * mm, "end": v(-2.44, 9.43) * mm});
            skFitSpline(sketch, "E644", {"points": [v(-4.3, 8.84) * mm, v(-4.24, 8.85) * mm, v(-4.18, 8.86) * mm, v(-4.13, 8.87) * mm]});
            skFitSpline(sketch, "E645", {"points": [v(-4.13, 8.87) * mm, v(-4.08, 8.88) * mm, v(-4.03, 8.9) * mm, v(-4, 8.92) * mm]});
            skFitSpline(sketch, "E646", {"points": [v(-4, 8.92) * mm, v(-3.95, 8.94) * mm, v(-3.92, 8.96) * mm, v(-3.9, 8.98) * mm]});
            skFitSpline(sketch, "E647", {"points": [v(-3.9, 8.98) * mm, v(-3.88, 9) * mm, v(-3.88, 9.02) * mm, v(-3.88, 9.04) * mm]});
            skFitSpline(sketch, "E648", {"points": [v(-3.88, 9.04) * mm, v(-3.9, 9.05) * mm, v(-3.9, 9.06) * mm, v(-3.93, 9.07) * mm]});
            skFitSpline(sketch, "E649", {"points": [v(-3.93, 9.07) * mm, v(-3.95, 9.07) * mm, v(-3.98, 9.06) * mm, v(-4.03, 9.05) * mm]});
            skFitSpline(sketch, "E650", {"points": [v(-4.03, 9.05) * mm, v(-4.04, 9.04) * mm, v(-4.06, 9.04) * mm, v(-4.07, 9.03) * mm]});
            skFitSpline(sketch, "E651", {"points": [v(-4.07, 9.03) * mm, v(-4.2, 8.99) * mm, v(-4.3, 8.97) * mm, v(-4.35, 8.98) * mm]});
            skFitSpline(sketch, "E652", {"points": [v(-4.35, 8.98) * mm, v(-4.4, 9) * mm, v(-4.45, 9.03) * mm, v(-4.48, 9.1) * mm]});
            skFitSpline(sketch, "E653", {"points": [v(-4.48, 9.1) * mm, v(-4.52, 9.16) * mm, v(-4.51, 9.23) * mm, v(-4.47, 9.3) * mm]});
            skFitSpline(sketch, "E654", {"points": [v(-4.47, 9.3) * mm, v(-4.42, 9.36) * mm, v(-4.34, 9.42) * mm, v(-4.22, 9.47) * mm]});
            skFitSpline(sketch, "E655", {"points": [v(-4.22, 9.47) * mm, v(-4.17, 9.5) * mm, v(-4.11, 9.52) * mm, v(-4.05, 9.53) * mm]});
            skFitSpline(sketch, "E656", {"points": [v(-4.05, 9.53) * mm, v(-4, 9.55) * mm, v(-3.93, 9.56) * mm, v(-3.87, 9.57) * mm]});
            skLineSegment(sketch, "E657", {"start": v(-4.22, 8.69) * mm, "end": v(-4.3, 8.84) * mm});
            skFitSpline(sketch, "E658", {"points": [v(-3.8, 9.41) * mm, v(-3.86, 9.41) * mm, v(-3.92, 9.4) * mm, v(-3.97, 9.4) * mm]});
            skFitSpline(sketch, "E659", {"points": [v(-3.97, 9.4) * mm, v(-4.03, 9.38) * mm, v(-4.08, 9.37) * mm, v(-4.14, 9.34) * mm]});
            skFitSpline(sketch, "E660", {"points": [v(-4.14, 9.34) * mm, v(-4.19, 9.32) * mm, v(-4.22, 9.3) * mm, v(-4.24, 9.28) * mm]});
            skFitSpline(sketch, "E661", {"points": [v(-4.24, 9.28) * mm, v(-4.26, 9.25) * mm, v(-4.26, 9.23) * mm, v(-4.25, 9.2) * mm]});
            skFitSpline(sketch, "E662", {"points": [v(-4.25, 9.2) * mm, v(-4.24, 9.2) * mm, v(-4.23, 9.18) * mm, v(-4.2, 9.18) * mm]});
            skFitSpline(sketch, "E663", {"points": [v(-4.2, 9.18) * mm, v(-4.19, 9.18) * mm, v(-4.15, 9.19) * mm, v(-4.1, 9.2) * mm]});
            skFitSpline(sketch, "E664", {"points": [v(-4.1, 9.2) * mm, v(-4.09, 9.2) * mm, v(-4.07, 9.21) * mm, v(-4.06, 9.22) * mm]});
            skFitSpline(sketch, "E665", {"points": [v(-4.06, 9.22) * mm, v(-3.94, 9.25) * mm, v(-3.86, 9.26) * mm, v(-3.8, 9.25) * mm]});
            skFitSpline(sketch, "E666", {"points": [v(-3.8, 9.25) * mm, v(-3.74, 9.24) * mm, v(-3.7, 9.2) * mm, v(-3.67, 9.13) * mm]});
            skFitSpline(sketch, "E667", {"points": [v(-3.67, 9.13) * mm, v(-3.65, 9.06) * mm, v(-3.65, 9) * mm, v(-3.7, 8.94) * mm]});
            skFitSpline(sketch, "E668", {"points": [v(-3.7, 8.94) * mm, v(-3.73, 8.89) * mm, v(-3.8, 8.83) * mm, v(-3.92, 8.79) * mm]});
            skFitSpline(sketch, "E669", {"points": [v(-3.92, 8.79) * mm, v(-3.96, 8.77) * mm, v(-4, 8.75) * mm, v(-4.06, 8.73) * mm]});
            skFitSpline(sketch, "E670", {"points": [v(-4.06, 8.73) * mm, v(-4.1, 8.72) * mm, v(-4.16, 8.7) * mm, v(-4.22, 8.69) * mm]});
            skLineSegment(sketch, "E671", {"start": v(-3.87, 9.57) * mm, "end": v(-3.8, 9.41) * mm});
            skFitSpline(sketch, "E672", {"points": [v(-4.34, 8.6) * mm, v(-4.41, 8.57) * mm, v(-4.49, 8.53) * mm, v(-4.57, 8.49) * mm]});
            skFitSpline(sketch, "E673", {"points": [v(-4.57, 8.49) * mm, v(-4.7, 8.6) * mm, v(-4.85, 8.7) * mm, v(-5, 8.8) * mm]});
            skFitSpline(sketch, "E674", {"points": [v(-5, 8.8) * mm, v(-4.97, 8.63) * mm, v(-4.94, 8.46) * mm, v(-4.91, 8.3) * mm]});
            skFitSpline(sketch, "E675", {"points": [v(-4.91, 8.3) * mm, v(-4.99, 8.25) * mm, v(-5.06, 8.2) * mm, v(-5.13, 8.16) * mm]});
            skFitSpline(sketch, "E676", {"points": [v(-5.13, 8.16) * mm, v(-5.17, 8.44) * mm, v(-5.2, 8.72) * mm, v(-5.23, 9) * mm]});
            skFitSpline(sketch, "E677", {"points": [v(-5.23, 9) * mm, v(-5.24, 9.1) * mm, v(-5.23, 9.17) * mm, v(-5.2, 9.22) * mm]});
            skFitSpline(sketch, "E678", {"points": [v(-5.2, 9.22) * mm, v(-5.18, 9.27) * mm, v(-5.13, 9.31) * mm, v(-5.06, 9.35) * mm]});
            skFitSpline(sketch, "E679", {"points": [v(-5.06, 9.35) * mm, v(-5, 9.38) * mm, v(-4.96, 9.4) * mm, v(-4.91, 9.43) * mm]});
            skFitSpline(sketch, "E680", {"points": [v(-4.84, 9.3) * mm, v(-4.87, 9.28) * mm, v(-4.9, 9.27) * mm, v(-4.92, 9.26) * mm]});
            skFitSpline(sketch, "E681", {"points": [v(-4.92, 9.26) * mm, v(-4.96, 9.23) * mm, v(-4.99, 9.21) * mm, v(-5, 9.2) * mm]});
            skFitSpline(sketch, "E682", {"points": [v(-5, 9.2) * mm, v(-5.01, 9.17) * mm, v(-5.02, 9.14) * mm, v(-5.01, 9.1) * mm]});
            skFitSpline(sketch, "E683", {"points": [v(-5.01, 9.1) * mm, v(-5.01, 9.1) * mm, v(-5.01, 9.1) * mm, v(-5.01, 9.09) * mm]});
            skFitSpline(sketch, "E684", {"points": [v(-5.01, 9.09) * mm, v(-4.78, 8.93) * mm, v(-4.56, 8.77) * mm, v(-4.34, 8.6) * mm]});
            skLineSegment(sketch, "E685", {"start": v(-4.91, 9.43) * mm, "end": v(-4.84, 9.3) * mm});
            skFitSpline(sketch, "E686", {"points": [v(-5.89, 7.88) * mm, v(-5.83, 7.9) * mm, v(-5.78, 7.92) * mm, v(-5.73, 7.94) * mm]});
            skFitSpline(sketch, "E687", {"points": [v(-5.73, 7.94) * mm, v(-5.68, 7.96) * mm, v(-5.64, 7.98) * mm, v(-5.6, 8) * mm]});
            skFitSpline(sketch, "E688", {"points": [v(-5.6, 8) * mm, v(-5.56, 8.04) * mm, v(-5.53, 8.06) * mm, v(-5.52, 8.09) * mm]});
            skFitSpline(sketch, "E689", {"points": [v(-5.52, 8.09) * mm, v(-5.5, 8.1) * mm, v(-5.5, 8.13) * mm, v(-5.52, 8.15) * mm]});
            skFitSpline(sketch, "E690", {"points": [v(-5.52, 8.15) * mm, v(-5.53, 8.16) * mm, v(-5.54, 8.17) * mm, v(-5.56, 8.17) * mm]});
            skFitSpline(sketch, "E691", {"points": [v(-5.56, 8.17) * mm, v(-5.58, 8.16) * mm, v(-5.62, 8.15) * mm, v(-5.66, 8.13) * mm]});
            skFitSpline(sketch, "E692", {"points": [v(-5.66, 8.13) * mm, v(-5.67, 8.12) * mm, v(-5.69, 8.11) * mm, v(-5.7, 8.1) * mm]});
            skFitSpline(sketch, "E693", {"points": [v(-5.7, 8.1) * mm, v(-5.82, 8.04) * mm, v(-5.9, 8) * mm, v(-5.96, 8) * mm]});
            skFitSpline(sketch, "E694", {"points": [v(-5.96, 8) * mm, v(-6.02, 8) * mm, v(-6.07, 8.03) * mm, v(-6.12, 8.1) * mm]});
            skFitSpline(sketch, "E695", {"points": [v(-6.12, 8.1) * mm, v(-6.16, 8.15) * mm, v(-6.17, 8.22) * mm, v(-6.14, 8.29) * mm]});
            skFitSpline(sketch, "E696", {"points": [v(-6.14, 8.29) * mm, v(-6.1, 8.36) * mm, v(-6.04, 8.44) * mm, v(-5.93, 8.51) * mm]});
            skFitSpline(sketch, "E697", {"points": [v(-5.93, 8.51) * mm, v(-5.88, 8.54) * mm, v(-5.83, 8.57) * mm, v(-5.77, 8.6) * mm]});
            skFitSpline(sketch, "E698", {"points": [v(-5.77, 8.6) * mm, v(-5.72, 8.63) * mm, v(-5.66, 8.65) * mm, v(-5.6, 8.68) * mm]});
            skLineSegment(sketch, "E699", {"start": v(-5.78, 7.74) * mm, "end": v(-5.89, 7.88) * mm});
            skFitSpline(sketch, "E700", {"points": [v(-5.5, 8.53) * mm, v(-5.56, 8.52) * mm, v(-5.62, 8.5) * mm, v(-5.67, 8.48) * mm]});
            skFitSpline(sketch, "E701", {"points": [v(-5.67, 8.48) * mm, v(-5.72, 8.46) * mm, v(-5.78, 8.43) * mm, v(-5.82, 8.4) * mm]});
            skFitSpline(sketch, "E702", {"points": [v(-5.82, 8.4) * mm, v(-5.87, 8.37) * mm, v(-5.9, 8.34) * mm, v(-5.91, 8.31) * mm]});
            skFitSpline(sketch, "E703", {"points": [v(-5.91, 8.31) * mm, v(-5.93, 8.29) * mm, v(-5.93, 8.27) * mm, v(-5.91, 8.25) * mm]});
            skFitSpline(sketch, "E704", {"points": [v(-5.91, 8.25) * mm, v(-5.9, 8.23) * mm, v(-5.88, 8.22) * mm, v(-5.86, 8.23) * mm]});
            skFitSpline(sketch, "E705", {"points": [v(-5.86, 8.23) * mm, v(-5.84, 8.23) * mm, v(-5.8, 8.24) * mm, v(-5.76, 8.27) * mm]});
            skFitSpline(sketch, "E706", {"points": [v(-5.76, 8.27) * mm, v(-5.75, 8.28) * mm, v(-5.73, 8.28) * mm, v(-5.72, 8.3) * mm]});
            skFitSpline(sketch, "E707", {"points": [v(-5.72, 8.3) * mm, v(-5.61, 8.35) * mm, v(-5.53, 8.37) * mm, v(-5.47, 8.37) * mm]});
            skFitSpline(sketch, "E708", {"points": [v(-5.47, 8.37) * mm, v(-5.41, 8.37) * mm, v(-5.37, 8.34) * mm, v(-5.33, 8.28) * mm]});
            skFitSpline(sketch, "E709", {"points": [v(-5.33, 8.28) * mm, v(-5.29, 8.21) * mm, v(-5.28, 8.15) * mm, v(-5.31, 8.09) * mm]});
            skFitSpline(sketch, "E710", {"points": [v(-5.31, 8.09) * mm, v(-5.34, 8.03) * mm, v(-5.4, 7.96) * mm, v(-5.5, 7.9) * mm]});
            skFitSpline(sketch, "E711", {"points": [v(-5.5, 7.9) * mm, v(-5.54, 7.87) * mm, v(-5.58, 7.84) * mm, v(-5.63, 7.82) * mm]});
            skFitSpline(sketch, "E712", {"points": [v(-5.63, 7.82) * mm, v(-5.67, 7.8) * mm, v(-5.73, 7.77) * mm, v(-5.78, 7.74) * mm]});
            skLineSegment(sketch, "E713", {"start": v(-5.6, 8.68) * mm, "end": v(-5.5, 8.53) * mm});
            skFitSpline(sketch, "E714", {"points": [v(-6.18, 7.4) * mm, v(-6.25, 7.34) * mm, v(-6.32, 7.28) * mm, v(-6.38, 7.23) * mm]});
            skLineSegment(sketch, "E715", {"start": v(-6.05, 7.24) * mm, "end": v(-6.18, 7.4) * mm});
            skFitSpline(sketch, "E716", {"points": [v(-6.49, 7.35) * mm, v(-6.42, 7.4) * mm, v(-6.35, 7.47) * mm, v(-6.29, 7.52) * mm]});
            skLineSegment(sketch, "E717", {"start": v(-6.38, 7.23) * mm, "end": v(-6.49, 7.35) * mm});
            skFitSpline(sketch, "E718", {"points": [v(-6.48, 7.75) * mm, v(-6.5, 7.78) * mm, v(-6.52, 7.8) * mm, v(-6.54, 7.8) * mm]});
            skFitSpline(sketch, "E719", {"points": [v(-6.54, 7.8) * mm, v(-6.56, 7.8) * mm, v(-6.59, 7.77) * mm, v(-6.62, 7.74) * mm]});
            skFitSpline(sketch, "E720", {"points": [v(-6.62, 7.74) * mm, v(-6.66, 7.71) * mm, v(-6.7, 7.68) * mm, v(-6.73, 7.65) * mm]});
            skLineSegment(sketch, "E721", {"start": v(-6.29, 7.52) * mm, "end": v(-6.48, 7.75) * mm});
            skFitSpline(sketch, "E722", {"points": [v(-6.84, 7.78) * mm, v(-6.78, 7.83) * mm, v(-6.72, 7.88) * mm, v(-6.66, 7.93) * mm]});
            skFitSpline(sketch, "E723", {"points": [v(-6.66, 7.93) * mm, v(-6.57, 8) * mm, v(-6.5, 8.03) * mm, v(-6.44, 8.03) * mm]});
            skFitSpline(sketch, "E724", {"points": [v(-6.44, 8.03) * mm, v(-6.38, 8.03) * mm, v(-6.33, 8) * mm, v(-6.27, 7.92) * mm]});
            skLineSegment(sketch, "E725", {"start": v(-6.73, 7.65) * mm, "end": v(-6.84, 7.78) * mm});
            skFitSpline(sketch, "E726", {"points": [v(-6.08, 7.69) * mm, v(-6.05, 7.71) * mm, v(-6.02, 7.74) * mm, v(-5.98, 7.77) * mm]});
            skLineSegment(sketch, "E727", {"start": v(-6.27, 7.92) * mm, "end": v(-6.08, 7.69) * mm});
            skFitSpline(sketch, "E728", {"points": [v(-5.88, 7.64) * mm, v(-5.92, 7.6) * mm, v(-5.95, 7.58) * mm, v(-5.98, 7.56) * mm]});
            skLineSegment(sketch, "E729", {"start": v(-5.98, 7.77) * mm, "end": v(-5.88, 7.64) * mm});
            skFitSpline(sketch, "E730", {"points": [v(-5.86, 7.4) * mm, v(-5.92, 7.35) * mm, v(-5.99, 7.3) * mm, v(-6.05, 7.24) * mm]});
            skLineSegment(sketch, "E731", {"start": v(-5.98, 7.56) * mm, "end": v(-5.86, 7.4) * mm});
            skFitSpline(sketch, "E732", {"points": [v(-7.37, 6.84) * mm, v(-7.28, 6.94) * mm, v(-7.2, 7.04) * mm, v(-7.1, 7.13) * mm]});
            skFitSpline(sketch, "E733", {"points": [v(-7.1, 7.13) * mm, v(-7.04, 7.18) * mm, v(-6.99, 7.24) * mm, v(-6.93, 7.29) * mm]});
            skFitSpline(sketch, "E734", {"points": [v(-6.93, 7.29) * mm, v(-6.98, 7.32) * mm, v(-7.02, 7.34) * mm, v(-7.07, 7.33) * mm]});
            skFitSpline(sketch, "E735", {"points": [v(-7.07, 7.33) * mm, v(-7.11, 7.32) * mm, v(-7.16, 7.3) * mm, v(-7.21, 7.24) * mm]});
            skLineSegment(sketch, "E736", {"start": v(-7.32, 6.8) * mm, "end": v(-7.37, 6.84) * mm});
            skFitSpline(sketch, "E737", {"points": [v(-7.21, 7.24) * mm, v(-7.21, 7.24) * mm, v(-7.21, 7.24) * mm, v(-7.21, 7.24) * mm]});
            skFitSpline(sketch, "E738", {"points": [v(-7.21, 7.24) * mm, v(-7.25, 7.2) * mm, v(-7.29, 7.15) * mm, v(-7.32, 7.1) * mm]});
            skFitSpline(sketch, "E739", {"points": [v(-7.32, 7.1) * mm, v(-7.35, 7.05) * mm, v(-7.38, 6.99) * mm, v(-7.4, 6.92) * mm]});
            skFitSpline(sketch, "E740", {"points": [v(-7.53, 7.04) * mm, v(-7.5, 7.1) * mm, v(-7.47, 7.16) * mm, v(-7.43, 7.22) * mm]});
            skFitSpline(sketch, "E741", {"points": [v(-7.43, 7.22) * mm, v(-7.4, 7.26) * mm, v(-7.36, 7.3) * mm, v(-7.32, 7.35) * mm]});
            skFitSpline(sketch, "E742", {"points": [v(-7.32, 7.35) * mm, v(-7.31, 7.36) * mm, v(-7.3, 7.36) * mm, v(-7.3, 7.37) * mm]});
            skFitSpline(sketch, "E743", {"points": [v(-7.3, 7.37) * mm, v(-7.2, 7.48) * mm, v(-7.08, 7.54) * mm, v(-6.97, 7.55) * mm]});
            skFitSpline(sketch, "E744", {"points": [v(-6.97, 7.55) * mm, v(-6.87, 7.56) * mm, v(-6.77, 7.51) * mm, v(-6.7, 7.43) * mm]});
            skFitSpline(sketch, "E745", {"points": [v(-6.7, 7.43) * mm, v(-6.62, 7.34) * mm, v(-6.58, 7.24) * mm, v(-6.6, 7.14) * mm]});
            skFitSpline(sketch, "E746", {"points": [v(-6.6, 7.14) * mm, v(-6.61, 7.04) * mm, v(-6.67, 6.94) * mm, v(-6.76, 6.84) * mm]});
            skFitSpline(sketch, "E747", {"points": [v(-6.76, 6.84) * mm, v(-6.77, 6.84) * mm, v(-6.78, 6.83) * mm, v(-6.79, 6.82) * mm]});
            skLineSegment(sketch, "E748", {"start": v(-7.4, 6.92) * mm, "end": v(-7.53, 7.04) * mm});
            skFitSpline(sketch, "E749", {"points": [v(-6.79, 6.82) * mm, v(-6.87, 6.75) * mm, v(-6.96, 6.7) * mm, v(-7.05, 6.7) * mm]});
            skFitSpline(sketch, "E750", {"points": [v(-7.05, 6.7) * mm, v(-7.15, 6.69) * mm, v(-7.24, 6.72) * mm, v(-7.32, 6.8) * mm]});
            skFitSpline(sketch, "E751", {"points": [v(-7.08, 6.94) * mm, v(-7.05, 6.91) * mm, v(-7.02, 6.9) * mm, v(-6.98, 6.9) * mm]});
            skFitSpline(sketch, "E752", {"points": [v(-6.98, 6.9) * mm, v(-6.95, 6.9) * mm, v(-6.92, 6.91) * mm, v(-6.9, 6.93) * mm]});
            skFitSpline(sketch, "E753", {"points": [v(-6.9, 6.93) * mm, v(-6.89, 6.94) * mm, v(-6.88, 6.94) * mm, v(-6.87, 6.95) * mm]});
            skFitSpline(sketch, "E754", {"points": [v(-6.87, 6.95) * mm, v(-6.83, 6.99) * mm, v(-6.81, 7.03) * mm, v(-6.8, 7.07) * mm]});
            skFitSpline(sketch, "E755", {"points": [v(-6.8, 7.07) * mm, v(-6.8, 7.1) * mm, v(-6.81, 7.14) * mm, v(-6.84, 7.18) * mm]});
            skFitSpline(sketch, "E756", {"points": [v(-6.84, 7.18) * mm, v(-6.9, 7.13) * mm, v(-6.95, 7.08) * mm, v(-7, 7.03) * mm]});
            skFitSpline(sketch, "E757", {"points": [v(-7, 7.03) * mm, v(-7.03, 7) * mm, v(-7.05, 6.97) * mm, v(-7.08, 6.94) * mm]});
            skFitSpline(sketch, "E758", {"points": [v(-6.62, 6.55) * mm, v(-6.66, 6.5) * mm, v(-6.7, 6.45) * mm, v(-6.75, 6.4) * mm]});
            skFitSpline(sketch, "E759", {"points": [v(-6.75, 6.4) * mm, v(-6.75, 6.52) * mm, v(-6.75, 6.64) * mm, v(-6.75, 6.76) * mm]});
            skFitSpline(sketch, "E760", {"points": [v(-6.75, 6.76) * mm, v(-6.74, 6.76) * mm, v(-6.74, 6.76) * mm, v(-6.74, 6.77) * mm]});
            skFitSpline(sketch, "E761", {"points": [v(-6.74, 6.77) * mm, v(-6.7, 6.8) * mm, v(-6.68, 6.83) * mm, v(-6.65, 6.86) * mm]});
            skFitSpline(sketch, "E762", {"points": [v(-6.65, 6.86) * mm, v(-6.64, 6.8) * mm, v(-6.64, 6.73) * mm, v(-6.63, 6.66) * mm]});
            skFitSpline(sketch, "E763", {"points": [v(-6.63, 6.66) * mm, v(-6.63, 6.62) * mm, v(-6.62, 6.58) * mm, v(-6.62, 6.55) * mm]});
            skFitSpline(sketch, "E764", {"points": [v(-7.75, 5.91) * mm, v(-7.74, 5.86) * mm, v(-7.74, 5.8) * mm, v(-7.74, 5.76) * mm]});
            skFitSpline(sketch, "E765", {"points": [v(-7.74, 5.76) * mm, v(-7.75, 5.7) * mm, v(-7.77, 5.66) * mm, v(-7.8, 5.62) * mm]});
            skFitSpline(sketch, "E766", {"points": [v(-7.8, 5.62) * mm, v(-7.85, 5.55) * mm, v(-7.91, 5.5) * mm, v(-7.98, 5.5) * mm]});
            skFitSpline(sketch, "E767", {"points": [v(-7.98, 5.5) * mm, v(-8.05, 5.48) * mm, v(-8.13, 5.5) * mm, v(-8.2, 5.55) * mm]});
            skFitSpline(sketch, "E768", {"points": [v(-8.57, 5.8) * mm, v(-8.52, 5.87) * mm, v(-8.47, 5.95) * mm, v(-8.41, 6.02) * mm]});
            skLineSegment(sketch, "E769", {"start": v(-8.2, 5.55) * mm, "end": v(-8.57, 5.8) * mm});
            skFitSpline(sketch, "E770", {"points": [v(-8.1, 5.8) * mm, v(-8.1, 5.8) * mm, v(-8.1, 5.8) * mm, v(-8.1, 5.8) * mm]});
            skFitSpline(sketch, "E771", {"points": [v(-8.1, 5.8) * mm, v(-8.09, 5.8) * mm, v(-8.08, 5.79) * mm, v(-8.07, 5.78) * mm]});
            skFitSpline(sketch, "E772", {"points": [v(-8.07, 5.78) * mm, v(-8.03, 5.75) * mm, v(-8, 5.74) * mm, v(-7.97, 5.74) * mm]});
            skFitSpline(sketch, "E773", {"points": [v(-7.97, 5.74) * mm, v(-7.94, 5.74) * mm, v(-7.92, 5.75) * mm, v(-7.9, 5.79) * mm]});
            skFitSpline(sketch, "E774", {"points": [v(-7.9, 5.79) * mm, v(-7.87, 5.83) * mm, v(-7.86, 5.87) * mm, v(-7.87, 5.9) * mm]});
            skFitSpline(sketch, "E775", {"points": [v(-7.87, 5.9) * mm, v(-7.88, 5.95) * mm, v(-7.91, 6) * mm, v(-7.97, 6.04) * mm]});
            skLineSegment(sketch, "E776", {"start": v(-8.41, 6.02) * mm, "end": v(-8.1, 5.8) * mm});
            skFitSpline(sketch, "E777", {"points": [v(-8.25, 6.25) * mm, v(-8.2, 6.32) * mm, v(-8.14, 6.4) * mm, v(-8.08, 6.46) * mm]});
            skLineSegment(sketch, "E778", {"start": v(-7.97, 6.04) * mm, "end": v(-8.25, 6.25) * mm});
            skFitSpline(sketch, "E779", {"points": [v(-7.79, 6.23) * mm, v(-7.73, 6.18) * mm, v(-7.68, 6.16) * mm, v(-7.65, 6.16) * mm]});
            skFitSpline(sketch, "E780", {"points": [v(-7.65, 6.16) * mm, v(-7.63, 6.16) * mm, v(-7.6, 6.17) * mm, v(-7.58, 6.2) * mm]});
            skFitSpline(sketch, "E781", {"points": [v(-7.58, 6.2) * mm, v(-7.55, 6.24) * mm, v(-7.53, 6.28) * mm, v(-7.54, 6.32) * mm]});
            skFitSpline(sketch, "E782", {"points": [v(-7.54, 6.32) * mm, v(-7.56, 6.37) * mm, v(-7.59, 6.41) * mm, v(-7.64, 6.45) * mm]});
            skLineSegment(sketch, "E783", {"start": v(-8.08, 6.46) * mm, "end": v(-7.79, 6.23) * mm});
            skFitSpline(sketch, "E784", {"points": [v(-7.9, 6.68) * mm, v(-7.85, 6.75) * mm, v(-7.79, 6.82) * mm, v(-7.73, 6.89) * mm]});
            skLineSegment(sketch, "E785", {"start": v(-7.64, 6.45) * mm, "end": v(-7.9, 6.68) * mm});
            skFitSpline(sketch, "E786", {"points": [v(-7.2, 6.42) * mm, v(-7.25, 6.35) * mm, v(-7.3, 6.29) * mm, v(-7.36, 6.22) * mm]});
            skLineSegment(sketch, "E787", {"start": v(-7.73, 6.89) * mm, "end": v(-7.2, 6.42) * mm});
            skFitSpline(sketch, "E788", {"points": [v(-7.44, 6.29) * mm, v(-7.43, 6.24) * mm, v(-7.43, 6.2) * mm, v(-7.44, 6.15) * mm]});
            skFitSpline(sketch, "E789", {"points": [v(-7.44, 6.15) * mm, v(-7.45, 6.1) * mm, v(-7.47, 6.06) * mm, v(-7.5, 6.02) * mm]});
            skFitSpline(sketch, "E790", {"points": [v(-7.5, 6.02) * mm, v(-7.53, 5.98) * mm, v(-7.57, 5.95) * mm, v(-7.62, 5.93) * mm]});
            skFitSpline(sketch, "E791", {"points": [v(-7.62, 5.93) * mm, v(-7.66, 5.91) * mm, v(-7.7, 5.9) * mm, v(-7.75, 5.91) * mm]});
            skFitSpline(sketch, "E792", {"points": [v(-7.75, 5.91) * mm, v(-7.75, 5.91) * mm, v(-7.75, 5.91) * mm, v(-7.75, 5.91) * mm]});
            skLineSegment(sketch, "E793", {"start": v(-7.36, 6.22) * mm, "end": v(-7.44, 6.29) * mm});
            skFitSpline(sketch, "E794", {"points": [v(-8.1, 5.2) * mm, v(-8.15, 5.13) * mm, v(-8.2, 5.06) * mm, v(-8.24, 4.99) * mm]});
            skLineSegment(sketch, "E795", {"start": v(-8.47, 5.44) * mm, "end": v(-8.1, 5.2) * mm});
            skFitSpline(sketch, "E796", {"points": [v(-8.3, 5.02) * mm, v(-8.33, 5.04) * mm, v(-8.37, 5.07) * mm, v(-8.42, 5.1) * mm]});
            skFitSpline(sketch, "E797", {"points": [v(-8.42, 5.1) * mm, v(-8.47, 5.13) * mm, v(-8.5, 5.15) * mm, v(-8.52, 5.16) * mm]});
            skFitSpline(sketch, "E798", {"points": [v(-8.52, 5.16) * mm, v(-8.57, 5.19) * mm, v(-8.6, 5.2) * mm, v(-8.63, 5.22) * mm]});
            skFitSpline(sketch, "E799", {"points": [v(-8.63, 5.22) * mm, v(-8.65, 5.23) * mm, v(-8.67, 5.23) * mm, v(-8.69, 5.23) * mm]});
            skFitSpline(sketch, "E800", {"points": [v(-8.69, 5.23) * mm, v(-8.7, 5.23) * mm, v(-8.72, 5.22) * mm, v(-8.74, 5.2) * mm]});
            skFitSpline(sketch, "E801", {"points": [v(-8.74, 5.2) * mm, v(-8.75, 5.2) * mm, v(-8.77, 5.18) * mm, v(-8.78, 5.16) * mm]});
            skFitSpline(sketch, "E802", {"points": [v(-8.78, 5.16) * mm, v(-8.8, 5.11) * mm, v(-8.81, 5.07) * mm, v(-8.8, 5.02) * mm]});
            skFitSpline(sketch, "E803", {"points": [v(-8.8, 5.02) * mm, v(-8.78, 4.97) * mm, v(-8.75, 4.94) * mm, v(-8.69, 4.9) * mm]});
            skLineSegment(sketch, "E804", {"start": v(-8.24, 4.99) * mm, "end": v(-8.3, 5.02) * mm});
            skFitSpline(sketch, "E805", {"points": [v(-8.38, 4.73) * mm, v(-8.42, 4.66) * mm, v(-8.46, 4.58) * mm, v(-8.5, 4.5) * mm]});
            skLineSegment(sketch, "E806", {"start": v(-8.69, 4.9) * mm, "end": v(-8.38, 4.73) * mm});
            skFitSpline(sketch, "E807", {"points": [v(-9.14, 4.84) * mm, v(-9.1, 4.92) * mm, v(-9.05, 5) * mm, v(-9, 5.08) * mm]});
            skLineSegment(sketch, "E808", {"start": v(-8.5, 4.5) * mm, "end": v(-9.14, 4.84) * mm});
            skFitSpline(sketch, "E809", {"points": [v(-8.91, 5.03) * mm, v(-8.93, 5.09) * mm, v(-8.94, 5.14) * mm, v(-8.93, 5.19) * mm]});
            skFitSpline(sketch, "E810", {"points": [v(-8.93, 5.19) * mm, v(-8.92, 5.24) * mm, v(-8.9, 5.29) * mm, v(-8.88, 5.34) * mm]});
            skFitSpline(sketch, "E811", {"points": [v(-8.88, 5.34) * mm, v(-8.83, 5.42) * mm, v(-8.77, 5.47) * mm, v(-8.7, 5.49) * mm]});
            skFitSpline(sketch, "E812", {"points": [v(-8.7, 5.49) * mm, v(-8.63, 5.5) * mm, v(-8.55, 5.49) * mm, v(-8.47, 5.44) * mm]});
            skFitSpline(sketch, "E813", {"points": [v(-8.47, 5.44) * mm, v(-8.47, 5.44) * mm, v(-8.47, 5.44) * mm, v(-8.47, 5.44) * mm, v(-8.47, 5.44) * mm]});
            skLineSegment(sketch, "E814", {"start": v(-9, 5.08) * mm, "end": v(-8.91, 5.03) * mm});
            skFitSpline(sketch, "E815", {"points": [v(-8.04, 4.8) * mm, v(-8.07, 4.82) * mm, v(-8.09, 4.82) * mm, v(-8.1, 4.81) * mm]});
            skFitSpline(sketch, "E816", {"points": [v(-8.1, 4.81) * mm, v(-8.13, 4.8) * mm, v(-8.15, 4.8) * mm, v(-8.16, 4.77) * mm]});
            skFitSpline(sketch, "E817", {"points": [v(-8.16, 4.77) * mm, v(-8.18, 4.75) * mm, v(-8.18, 4.72) * mm, v(-8.17, 4.7) * mm]});
            skFitSpline(sketch, "E818", {"points": [v(-8.17, 4.7) * mm, v(-8.17, 4.68) * mm, v(-8.16, 4.66) * mm, v(-8.14, 4.65) * mm]});
            skFitSpline(sketch, "E819", {"points": [v(-8.14, 4.65) * mm, v(-8.12, 4.64) * mm, v(-8.1, 4.63) * mm, v(-8.07, 4.64) * mm]});
            skFitSpline(sketch, "E820", {"points": [v(-8.07, 4.64) * mm, v(-8.05, 4.65) * mm, v(-8.03, 4.66) * mm, v(-8.02, 4.69) * mm]});
            skFitSpline(sketch, "E821", {"points": [v(-8.02, 4.69) * mm, v(-8, 4.7) * mm, v(-8, 4.73) * mm, v(-8, 4.75) * mm]});
            skFitSpline(sketch, "E822", {"points": [v(-8, 4.75) * mm, v(-8.01, 4.78) * mm, v(-8.03, 4.8) * mm, v(-8.04, 4.8) * mm]});
            skFitSpline(sketch, "E823", {"points": [v(-8.04, 4.8) * mm, v(-8.04, 4.8) * mm, v(-8.04, 4.8) * mm, v(-8.04, 4.8) * mm, v(-8.04, 4.8) * mm]});
            skFitSpline(sketch, "E824", {"points": [v(-8, 4.9) * mm, v(-7.95, 4.87) * mm, v(-7.92, 4.83) * mm, v(-7.9, 4.78) * mm]});
            skFitSpline(sketch, "E825", {"points": [v(-7.9, 4.78) * mm, v(-7.9, 4.73) * mm, v(-7.9, 4.68) * mm, v(-7.93, 4.64) * mm]});
            skFitSpline(sketch, "E826", {"points": [v(-7.93, 4.64) * mm, v(-7.96, 4.59) * mm, v(-8, 4.56) * mm, v(-8.05, 4.54) * mm]});
            skFitSpline(sketch, "E827", {"points": [v(-8.05, 4.54) * mm, v(-8.1, 4.53) * mm, v(-8.14, 4.53) * mm, v(-8.19, 4.55) * mm]});
            skFitSpline(sketch, "E828", {"points": [v(-8.19, 4.55) * mm, v(-8.23, 4.58) * mm, v(-8.26, 4.62) * mm, v(-8.27, 4.67) * mm]});
            skFitSpline(sketch, "E829", {"points": [v(-8.27, 4.67) * mm, v(-8.28, 4.72) * mm, v(-8.28, 4.77) * mm, v(-8.25, 4.82) * mm]});
            skFitSpline(sketch, "E830", {"points": [v(-8.25, 4.82) * mm, v(-8.22, 4.87) * mm, v(-8.18, 4.9) * mm, v(-8.13, 4.91) * mm]});
            skFitSpline(sketch, "E831", {"points": [v(-8.13, 4.91) * mm, v(-8.08, 4.93) * mm, v(-8.03, 4.92) * mm, v(-8, 4.9) * mm]});
            skFitSpline(sketch, "E832", {"points": [v(-8.61, 3.72) * mm, v(-8.65, 3.64) * mm, v(-8.68, 3.56) * mm, v(-8.71, 3.47) * mm]});
            skFitSpline(sketch, "E833", {"points": [v(-9.05, 3.6) * mm, v(-9.1, 3.48) * mm, v(-9.15, 3.35) * mm, v(-9.2, 3.22) * mm]});
            skLineSegment(sketch, "E834", {"start": v(-8.71, 3.47) * mm, "end": v(-9.05, 3.6) * mm});
            skFitSpline(sketch, "E835", {"points": [v(-8.85, 3.1) * mm, v(-8.88, 3.02) * mm, v(-8.91, 2.93) * mm, v(-8.94, 2.85) * mm]});
            skLineSegment(sketch, "E836", {"start": v(-9.2, 3.22) * mm, "end": v(-8.85, 3.1) * mm});
            skFitSpline(sketch, "E837", {"points": [v(-9.84, 3.13) * mm, v(-9.82, 3.23) * mm, v(-9.78, 3.32) * mm, v(-9.75, 3.41) * mm]});
            skLineSegment(sketch, "E838", {"start": v(-8.94, 2.85) * mm, "end": v(-9.84, 3.13) * mm});
            skFitSpline(sketch, "E839", {"points": [v(-9.37, 3.28) * mm, v(-9.32, 3.41) * mm, v(-9.28, 3.54) * mm, v(-9.22, 3.67) * mm]});
            skLineSegment(sketch, "E840", {"start": v(-9.75, 3.41) * mm, "end": v(-9.37, 3.28) * mm});
            skFitSpline(sketch, "E841", {"points": [v(-9.6, 3.82) * mm, v(-9.56, 3.91) * mm, v(-9.53, 4) * mm, v(-9.49, 4.1) * mm]});
            skLineSegment(sketch, "E842", {"start": v(-9.22, 3.67) * mm, "end": v(-9.6, 3.82) * mm});
            skFitSpline(sketch, "E843", {"points": [v(-9, 2.64) * mm, v(-9.08, 2.36) * mm, v(-9.15, 2.08) * mm, v(-9.2, 1.8) * mm]});
            skLineSegment(sketch, "E844", {"start": v(-9.49, 4.1) * mm, "end": v(-8.61, 3.72) * mm});
            skFitSpline(sketch, "E845", {"points": [v(-9.35, 1.82) * mm, v(-9.52, 2.05) * mm, v(-9.68, 2.28) * mm, v(-9.83, 2.53) * mm]});
            skFitSpline(sketch, "E846", {"points": [v(-9.83, 2.53) * mm, v(-9.88, 2.33) * mm, v(-9.92, 2.13) * mm, v(-9.96, 1.92) * mm]});
            skLineSegment(sketch, "E847", {"start": v(-9.2, 1.8) * mm, "end": v(-9.35, 1.82) * mm});
            skFitSpline(sketch, "E848", {"points": [v(-10.14, 1.96) * mm, v(-10.08, 2.29) * mm, v(-10, 2.6) * mm, v(-9.9, 2.93) * mm]});
            skLineSegment(sketch, "E849", {"start": v(-9.96, 1.92) * mm, "end": v(-10.14, 1.96) * mm});
            skFitSpline(sketch, "E850", {"points": [v(-9.77, 2.89) * mm, v(-9.63, 2.63) * mm, v(-9.48, 2.4) * mm, v(-9.32, 2.16) * mm]});
            skFitSpline(sketch, "E851", {"points": [v(-9.32, 2.16) * mm, v(-9.28, 2.34) * mm, v(-9.23, 2.52) * mm, v(-9.18, 2.7) * mm]});
            skLineSegment(sketch, "E852", {"start": v(-9.9, 2.93) * mm, "end": v(-9.77, 2.89) * mm});
            skLineSegment(sketch, "E853", {"start": v(-9.18, 2.7) * mm, "end": v(-9, 2.64) * mm});
            skFitSpline(sketch, "E854", {"points": [v(-9.57, 0.9) * mm, v(-9.54, 0.95) * mm, v(-9.52, 1) * mm, v(-9.5, 1.06) * mm]});
            skFitSpline(sketch, "E855", {"points": [v(-9.5, 1.06) * mm, v(-9.48, 1.11) * mm, v(-9.47, 1.16) * mm, v(-9.46, 1.21) * mm]});
            skFitSpline(sketch, "E856", {"points": [v(-9.46, 1.21) * mm, v(-9.46, 1.28) * mm, v(-9.46, 1.32) * mm, v(-9.47, 1.36) * mm]});
            skFitSpline(sketch, "E857", {"points": [v(-9.47, 1.36) * mm, v(-9.48, 1.4) * mm, v(-9.5, 1.4) * mm, v(-9.54, 1.41) * mm]});
            skFitSpline(sketch, "E858", {"points": [v(-9.54, 1.41) * mm, v(-9.56, 1.42) * mm, v(-9.58, 1.41) * mm, v(-9.6, 1.4) * mm]});
            skFitSpline(sketch, "E859", {"points": [v(-9.6, 1.4) * mm, v(-9.62, 1.37) * mm, v(-9.63, 1.34) * mm, v(-9.65, 1.28) * mm]});
            skFitSpline(sketch, "E860", {"points": [v(-9.65, 1.28) * mm, v(-9.66, 1.24) * mm, v(-9.68, 1.2) * mm, v(-9.69, 1.17) * mm]});
            skFitSpline(sketch, "E861", {"points": [v(-9.69, 1.17) * mm, v(-9.72, 1.05) * mm, v(-9.76, 0.97) * mm, v(-9.81, 0.92) * mm]});
            skFitSpline(sketch, "E862", {"points": [v(-9.81, 0.92) * mm, v(-9.86, 0.87) * mm, v(-9.92, 0.85) * mm, v(-10, 0.86) * mm]});
            skFitSpline(sketch, "E863", {"points": [v(-10, 0.86) * mm, v(-10.1, 0.87) * mm, v(-10.18, 0.91) * mm, v(-10.23, 1) * mm]});
            skFitSpline(sketch, "E864", {"points": [v(-10.23, 1) * mm, v(-10.27, 1.07) * mm, v(-10.28, 1.19) * mm, v(-10.26, 1.34) * mm]});
            skFitSpline(sketch, "E865", {"points": [v(-10.26, 1.34) * mm, v(-10.25, 1.41) * mm, v(-10.24, 1.48) * mm, v(-10.22, 1.55) * mm]});
            skFitSpline(sketch, "E866", {"points": [v(-10.22, 1.55) * mm, v(-10.2, 1.62) * mm, v(-10.16, 1.7) * mm, v(-10.13, 1.76) * mm]});
            skLineSegment(sketch, "E867", {"start": v(-9.37, 0.87) * mm, "end": v(-9.57, 0.9) * mm});
            skFitSpline(sketch, "E868", {"points": [v(-9.93, 1.73) * mm, v(-9.97, 1.66) * mm, v(-10, 1.6) * mm, v(-10.03, 1.53) * mm]});
            skFitSpline(sketch, "E869", {"points": [v(-10.03, 1.53) * mm, v(-10.06, 1.47) * mm, v(-10.08, 1.4) * mm, v(-10.08, 1.34) * mm]});
            skFitSpline(sketch, "E870", {"points": [v(-10.08, 1.34) * mm, v(-10.1, 1.28) * mm, v(-10.09, 1.23) * mm, v(-10.08, 1.2) * mm]});
            skFitSpline(sketch, "E871", {"points": [v(-10.08, 1.2) * mm, v(-10.06, 1.16) * mm, v(-10.04, 1.14) * mm, v(-10, 1.14) * mm]});
            skFitSpline(sketch, "E872", {"points": [v(-10, 1.14) * mm, v(-9.98, 1.13) * mm, v(-9.95, 1.14) * mm, v(-9.93, 1.16) * mm]});
            skFitSpline(sketch, "E873", {"points": [v(-9.93, 1.16) * mm, v(-9.91, 1.18) * mm, v(-9.9, 1.23) * mm, v(-9.87, 1.3) * mm]});
            skFitSpline(sketch, "E874", {"points": [v(-9.87, 1.3) * mm, v(-9.86, 1.33) * mm, v(-9.85, 1.36) * mm, v(-9.84, 1.4) * mm]});
            skFitSpline(sketch, "E875", {"points": [v(-9.84, 1.4) * mm, v(-9.8, 1.5) * mm, v(-9.76, 1.58) * mm, v(-9.7, 1.62) * mm]});
            skFitSpline(sketch, "E876", {"points": [v(-9.7, 1.62) * mm, v(-9.65, 1.66) * mm, v(-9.59, 1.68) * mm, v(-9.51, 1.66) * mm]});
            skFitSpline(sketch, "E877", {"points": [v(-9.51, 1.66) * mm, v(-9.42, 1.65) * mm, v(-9.35, 1.6) * mm, v(-9.32, 1.53) * mm]});
            skFitSpline(sketch, "E878", {"points": [v(-9.32, 1.53) * mm, v(-9.28, 1.45) * mm, v(-9.27, 1.35) * mm, v(-9.28, 1.23) * mm]});
            skFitSpline(sketch, "E879", {"points": [v(-9.28, 1.23) * mm, v(-9.29, 1.17) * mm, v(-9.3, 1.12) * mm, v(-9.32, 1.06) * mm]});
            skFitSpline(sketch, "E880", {"points": [v(-9.32, 1.06) * mm, v(-9.33, 1) * mm, v(-9.35, 0.94) * mm, v(-9.37, 0.87) * mm]});
            skLineSegment(sketch, "E881", {"start": v(-10.13, 1.76) * mm, "end": v(-9.93, 1.73) * mm});
            skFitSpline(sketch, "E882", {"points": [v(-9.38, 0.07) * mm, v(-9.38, 0.06) * mm, v(-9.38, 0.05) * mm, v(-9.38, 0.03) * mm]});
            skFitSpline(sketch, "E883", {"points": [v(-9.38, 0.03) * mm, v(-9.38, -0.04) * mm, v(-9.38, -0.12) * mm, v(-9.38, -0.2) * mm]});
            skFitSpline(sketch, "E884", {"points": [v(-10.14, -0.21) * mm, v(-10.14, -0.38) * mm, v(-10.13, -0.55) * mm, v(-10.12, -0.72) * mm]});
            skLineSegment(sketch, "E885", {"start": v(-9.38, -0.2) * mm, "end": v(-10.14, -0.21) * mm});
            skFitSpline(sketch, "E886", {"points": [v(-10.3, -0.74) * mm, v(-10.32, -0.48) * mm, v(-10.33, -0.22) * mm, v(-10.33, 0.03) * mm]});
            skFitSpline(sketch, "E887", {"points": [v(-10.33, 0.03) * mm, v(-10.33, 0.05) * mm, v(-10.33, 0.06) * mm, v(-10.33, 0.08) * mm]});
            skLineSegment(sketch, "E888", {"start": v(-10.12, -0.72) * mm, "end": v(-10.3, -0.74) * mm});
            skFitSpline(sketch, "E889", {"points": [v(-9.57, -0.84) * mm, v(-9.57, -0.93) * mm, v(-9.56, -1.01) * mm, v(-9.55, -1.1) * mm]});
            skLineSegment(sketch, "E890", {"start": v(-10.33, 0.08) * mm, "end": v(-9.38, 0.07) * mm});
            skFitSpline(sketch, "E891", {"points": [v(-10.26, -1.18) * mm, v(-10.27, -1.1) * mm, v(-10.28, -1) * mm, v(-10.29, -0.9) * mm]});
            skLineSegment(sketch, "E892", {"start": v(-9.55, -1.1) * mm, "end": v(-10.26, -1.18) * mm});
            skFitSpline(sketch, "E893", {"points": [v(-9.3, -0.82) * mm, v(-9.3, -0.9) * mm, v(-9.28, -0.98) * mm, v(-9.27, -1.06) * mm]});
            skLineSegment(sketch, "E894", {"start": v(-10.29, -0.9) * mm, "end": v(-9.57, -0.84) * mm});
            skFitSpline(sketch, "E895", {"points": [v(-9.46, -1.09) * mm, v(-9.47, -1) * mm, v(-9.48, -0.92) * mm, v(-9.48, -0.83) * mm]});
            skLineSegment(sketch, "E896", {"start": v(-9.27, -1.06) * mm, "end": v(-9.46, -1.09) * mm});
            skFitSpline(sketch, "E897", {"points": [v(-10, -1.87) * mm, v(-9.99, -1.93) * mm, v(-9.96, -1.96) * mm, v(-9.92, -1.99) * mm]});
            skFitSpline(sketch, "E898", {"points": [v(-9.92, -1.99) * mm, v(-9.88, -2) * mm, v(-9.83, -2.01) * mm, v(-9.76, -2) * mm]});
            skFitSpline(sketch, "E899", {"points": [v(-9.76, -2) * mm, v(-9.7, -1.99) * mm, v(-9.65, -1.96) * mm, v(-9.62, -1.92) * mm]});
            skFitSpline(sketch, "E900", {"points": [v(-9.62, -1.92) * mm, v(-9.59, -1.89) * mm, v(-9.58, -1.84) * mm, v(-9.59, -1.79) * mm]});
            skFitSpline(sketch, "E901", {"points": [v(-9.59, -1.79) * mm, v(-9.6, -1.73) * mm, v(-9.62, -1.7) * mm, v(-9.67, -1.67) * mm]});
            skFitSpline(sketch, "E902", {"points": [v(-9.67, -1.67) * mm, v(-9.7, -1.65) * mm, v(-9.76, -1.64) * mm, v(-9.83, -1.66) * mm]});
            skFitSpline(sketch, "E903", {"points": [v(-9.83, -1.66) * mm, v(-9.9, -1.67) * mm, v(-9.94, -1.7) * mm, v(-9.97, -1.73) * mm]});
            skFitSpline(sketch, "E904", {"points": [v(-9.97, -1.73) * mm, v(-10, -1.76) * mm, v(-10.01, -1.81) * mm, v(-10, -1.87) * mm]});
            skLineSegment(sketch, "E905", {"start": v(-9.48, -0.83) * mm, "end": v(-9.3, -0.82) * mm});
            skFitSpline(sketch, "E906", {"points": [v(-9.58, -1.61) * mm, v(-9.53, -1.64) * mm, v(-9.5, -1.67) * mm, v(-9.47, -1.71) * mm]});
            skFitSpline(sketch, "E907", {"points": [v(-9.47, -1.71) * mm, v(-9.44, -1.75) * mm, v(-9.42, -1.8) * mm, v(-9.4, -1.85) * mm]});
            skFitSpline(sketch, "E908", {"points": [v(-9.4, -1.85) * mm, v(-9.39, -1.95) * mm, v(-9.4, -2.03) * mm, v(-9.46, -2.11) * mm]});
            skFitSpline(sketch, "E909", {"points": [v(-9.46, -2.11) * mm, v(-9.51, -2.19) * mm, v(-9.6, -2.24) * mm, v(-9.7, -2.27) * mm]});
            skFitSpline(sketch, "E910", {"points": [v(-9.7, -2.27) * mm, v(-9.8, -2.3) * mm, v(-9.9, -2.28) * mm, v(-9.99, -2.23) * mm]});
            skFitSpline(sketch, "E911", {"points": [v(-9.99, -2.23) * mm, v(-10.07, -2.18) * mm, v(-10.12, -2.1) * mm, v(-10.14, -2) * mm]});
            skFitSpline(sketch, "E912", {"points": [v(-10.14, -2) * mm, v(-10.15, -1.94) * mm, v(-10.15, -1.89) * mm, v(-10.14, -1.84) * mm]});
            skFitSpline(sketch, "E913", {"points": [v(-10.14, -1.84) * mm, v(-10.13, -1.79) * mm, v(-10.1, -1.74) * mm, v(-10.08, -1.7) * mm]});
            skFitSpline(sketch, "E914", {"points": [v(-10.18, -1.72) * mm, v(-10.2, -1.63) * mm, v(-10.2, -1.54) * mm, v(-10.22, -1.45) * mm]});
            skLineSegment(sketch, "E915", {"start": v(-10.08, -1.7) * mm, "end": v(-10.18, -1.72) * mm});
            skFitSpline(sketch, "E916", {"points": [v(-9.24, -1.3) * mm, v(-9.23, -1.38) * mm, v(-9.21, -1.46) * mm, v(-9.2, -1.55) * mm]});
            skLineSegment(sketch, "E917", {"start": v(-10.22, -1.45) * mm, "end": v(-9.24, -1.3) * mm});
            skLineSegment(sketch, "E918", {"start": v(-9.2, -1.55) * mm, "end": v(-9.58, -1.61) * mm});
            skFitSpline(sketch, "E919", {"points": [v(-9.47, -3.27) * mm, v(-9.54, -3.07) * mm, v(-9.6, -2.88) * mm, v(-9.66, -2.68) * mm]});
            skFitSpline(sketch, "E920", {"points": [v(-9.66, -2.68) * mm, v(-9.7, -2.7) * mm, v(-9.74, -2.73) * mm, v(-9.75, -2.77) * mm]});
            skFitSpline(sketch, "E921", {"points": [v(-9.75, -2.77) * mm, v(-9.77, -2.82) * mm, v(-9.77, -2.88) * mm, v(-9.75, -2.94) * mm]});
            skFitSpline(sketch, "E922", {"points": [v(-9.75, -2.94) * mm, v(-9.73, -3) * mm, v(-9.7, -3.05) * mm, v(-9.67, -3.1) * mm]});
            skFitSpline(sketch, "E923", {"points": [v(-9.67, -3.1) * mm, v(-9.64, -3.16) * mm, v(-9.6, -3.2) * mm, v(-9.55, -3.26) * mm]});
            skLineSegment(sketch, "E924", {"start": v(-9.4, -3.25) * mm, "end": v(-9.47, -3.27) * mm});
            skFitSpline(sketch, "E925", {"points": [v(-9.72, -3.31) * mm, v(-9.76, -3.26) * mm, v(-9.8, -3.2) * mm, v(-9.82, -3.15) * mm]});
            skFitSpline(sketch, "E926", {"points": [v(-9.82, -3.15) * mm, v(-9.85, -3.09) * mm, v(-9.88, -3.03) * mm, v(-9.9, -2.96) * mm]});
            skFitSpline(sketch, "E927", {"points": [v(-9.9, -2.96) * mm, v(-9.94, -2.82) * mm, v(-9.94, -2.69) * mm, v(-9.9, -2.59) * mm]});
            skFitSpline(sketch, "E928", {"points": [v(-9.9, -2.59) * mm, v(-9.86, -2.5) * mm, v(-9.78, -2.43) * mm, v(-9.67, -2.4) * mm]});
            skFitSpline(sketch, "E929", {"points": [v(-9.67, -2.4) * mm, v(-9.55, -2.37) * mm, v(-9.46, -2.39) * mm, v(-9.37, -2.44) * mm]});
            skFitSpline(sketch, "E930", {"points": [v(-9.37, -2.44) * mm, v(-9.29, -2.5) * mm, v(-9.22, -2.6) * mm, v(-9.18, -2.73) * mm]});
            skFitSpline(sketch, "E931", {"points": [v(-9.18, -2.73) * mm, v(-9.15, -2.85) * mm, v(-9.15, -2.96) * mm, v(-9.19, -3.05) * mm]});
            skFitSpline(sketch, "E932", {"points": [v(-9.19, -3.05) * mm, v(-9.23, -3.14) * mm, v(-9.3, -3.21) * mm, v(-9.4, -3.25) * mm]});
            skFitSpline(sketch, "E933", {"points": [v(-9.4, -3.25) * mm, v(-9.4, -3.25) * mm, v(-9.4, -3.25) * mm, v(-9.4, -3.25) * mm, v(-9.4, -3.25) * mm]});
            skLineSegment(sketch, "E934", {"start": v(-9.55, -3.26) * mm, "end": v(-9.72, -3.31) * mm});
            skFitSpline(sketch, "E935", {"points": [v(-9.42, -2.97) * mm, v(-9.38, -2.95) * mm, v(-9.35, -2.93) * mm, v(-9.34, -2.9) * mm]});
            skFitSpline(sketch, "E936", {"points": [v(-9.34, -2.9) * mm, v(-9.32, -2.86) * mm, v(-9.32, -2.82) * mm, v(-9.33, -2.77) * mm]});
            skFitSpline(sketch, "E937", {"points": [v(-9.33, -2.77) * mm, v(-9.34, -2.73) * mm, v(-9.37, -2.7) * mm, v(-9.4, -2.67) * mm]});
            skFitSpline(sketch, "E938", {"points": [v(-9.4, -2.67) * mm, v(-9.43, -2.64) * mm, v(-9.47, -2.63) * mm, v(-9.52, -2.64) * mm]});
            skFitSpline(sketch, "E939", {"points": [v(-9.52, -2.64) * mm, v(-9.49, -2.75) * mm, v(-9.46, -2.86) * mm, v(-9.42, -2.97) * mm]});
            skFitSpline(sketch, "E940", {"points": [v(-8.96, -3.94) * mm, v(-8.96, -3.92) * mm, v(-8.96, -3.9) * mm, v(-8.97, -3.87) * mm]});
            skFitSpline(sketch, "E941", {"points": [v(-8.97, -3.87) * mm, v(-8.97, -3.85) * mm, v(-8.98, -3.83) * mm, v(-8.99, -3.8) * mm]});
            skFitSpline(sketch, "E942", {"points": [v(-8.99, -3.8) * mm, v(-9.02, -3.74) * mm, v(-9.05, -3.7) * mm, v(-9.1, -3.68) * mm]});
            skFitSpline(sketch, "E943", {"points": [v(-9.1, -3.68) * mm, v(-9.15, -3.67) * mm, v(-9.2, -3.67) * mm, v(-9.27, -3.7) * mm]});
            skFitSpline(sketch, "E944", {"points": [v(-9.58, -3.82) * mm, v(-9.61, -3.73) * mm, v(-9.64, -3.65) * mm, v(-9.68, -3.56) * mm]});
            skLineSegment(sketch, "E945", {"start": v(-9.27, -3.7) * mm, "end": v(-9.58, -3.82) * mm});
            skFitSpline(sketch, "E946", {"points": [v(-9, -3.31) * mm, v(-8.98, -3.4) * mm, v(-8.95, -3.47) * mm, v(-8.91, -3.55) * mm]});
            skLineSegment(sketch, "E947", {"start": v(-9.68, -3.56) * mm, "end": v(-9, -3.31) * mm});
            skFitSpline(sketch, "E948", {"points": [v(-9.02, -3.6) * mm, v(-8.97, -3.6) * mm, v(-8.92, -3.63) * mm, v(-8.89, -3.66) * mm]});
            skFitSpline(sketch, "E949", {"points": [v(-8.89, -3.66) * mm, v(-8.85, -3.7) * mm, v(-8.82, -3.74) * mm, v(-8.8, -3.8) * mm]});
            skFitSpline(sketch, "E950", {"points": [v(-8.8, -3.8) * mm, v(-8.8, -3.8) * mm, v(-8.79, -3.8) * mm, v(-8.79, -3.82) * mm]});
            skFitSpline(sketch, "E951", {"points": [v(-8.79, -3.82) * mm, v(-8.78, -3.83) * mm, v(-8.78, -3.84) * mm, v(-8.77, -3.86) * mm]});
            skFitSpline(sketch, "E952", {"points": [v(-8.77, -3.86) * mm, v(-8.83, -3.89) * mm, v(-8.9, -3.91) * mm, v(-8.96, -3.94) * mm]});
            skLineSegment(sketch, "E953", {"start": v(-8.91, -3.55) * mm, "end": v(-9.02, -3.6) * mm});
            skFitSpline(sketch, "E954", {"points": [v(-8.73, -4.9) * mm, v(-8.84, -4.72) * mm, v(-8.93, -4.53) * mm, v(-9.02, -4.35) * mm]});
            skFitSpline(sketch, "E955", {"points": [v(-9.02, -4.35) * mm, v(-9.07, -4.37) * mm, v(-9.1, -4.41) * mm, v(-9.1, -4.46) * mm]});
            skFitSpline(sketch, "E956", {"points": [v(-9.1, -4.46) * mm, v(-9.1, -4.5) * mm, v(-9.1, -4.56) * mm, v(-9.06, -4.62) * mm]});
            skFitSpline(sketch, "E957", {"points": [v(-9.06, -4.62) * mm, v(-9.04, -4.68) * mm, v(-9, -4.72) * mm, v(-8.96, -4.77) * mm]});
            skFitSpline(sketch, "E958", {"points": [v(-8.96, -4.77) * mm, v(-8.92, -4.82) * mm, v(-8.87, -4.86) * mm, v(-8.82, -4.9) * mm]});
            skLineSegment(sketch, "E959", {"start": v(-8.68, -4.87) * mm, "end": v(-8.73, -4.9) * mm});
            skFitSpline(sketch, "E960", {"points": [v(-8.97, -4.99) * mm, v(-9.02, -4.94) * mm, v(-9.07, -4.89) * mm, v(-9.1, -4.84) * mm]});
            skFitSpline(sketch, "E961", {"points": [v(-9.1, -4.84) * mm, v(-9.15, -4.78) * mm, v(-9.18, -4.73) * mm, v(-9.2, -4.67) * mm]});
            skFitSpline(sketch, "E962", {"points": [v(-9.2, -4.67) * mm, v(-9.28, -4.53) * mm, v(-9.3, -4.4) * mm, v(-9.28, -4.3) * mm]});
            skFitSpline(sketch, "E963", {"points": [v(-9.28, -4.3) * mm, v(-9.26, -4.2) * mm, v(-9.19, -4.12) * mm, v(-9.08, -4.07) * mm]});
            skFitSpline(sketch, "E964", {"points": [v(-9.08, -4.07) * mm, v(-8.97, -4.03) * mm, v(-8.87, -4.02) * mm, v(-8.78, -4.07) * mm]});
            skFitSpline(sketch, "E965", {"points": [v(-8.78, -4.07) * mm, v(-8.69, -4.11) * mm, v(-8.6, -4.2) * mm, v(-8.55, -4.32) * mm]});
            skFitSpline(sketch, "E966", {"points": [v(-8.55, -4.32) * mm, v(-8.5, -4.43) * mm, v(-8.47, -4.53) * mm, v(-8.5, -4.63) * mm]});
            skFitSpline(sketch, "E967", {"points": [v(-8.5, -4.63) * mm, v(-8.52, -4.73) * mm, v(-8.58, -4.81) * mm, v(-8.68, -4.87) * mm]});
            skFitSpline(sketch, "E968", {"points": [v(-8.68, -4.87) * mm, v(-8.68, -4.87) * mm, v(-8.68, -4.87) * mm, v(-8.68, -4.87) * mm, v(-8.68, -4.87) * mm]});
            skLineSegment(sketch, "E969", {"start": v(-8.82, -4.9) * mm, "end": v(-8.97, -4.99) * mm});
            skFitSpline(sketch, "E970", {"points": [v(-8.74, -4.6) * mm, v(-8.7, -4.57) * mm, v(-8.68, -4.54) * mm, v(-8.67, -4.5) * mm]});
            skFitSpline(sketch, "E971", {"points": [v(-8.67, -4.5) * mm, v(-8.66, -4.47) * mm, v(-8.66, -4.43) * mm, v(-8.68, -4.39) * mm]});
            skFitSpline(sketch, "E972", {"points": [v(-8.68, -4.39) * mm, v(-8.7, -4.34) * mm, v(-8.74, -4.3) * mm, v(-8.77, -4.3) * mm]});
            skFitSpline(sketch, "E973", {"points": [v(-8.77, -4.3) * mm, v(-8.8, -4.28) * mm, v(-8.85, -4.27) * mm, v(-8.9, -4.29) * mm]});
            skFitSpline(sketch, "E974", {"points": [v(-8.9, -4.29) * mm, v(-8.84, -4.39) * mm, v(-8.8, -4.5) * mm, v(-8.74, -4.6) * mm]});
            skFitSpline(sketch, "E975", {"points": [v(-8.1, -5.52) * mm, v(-8.1, -5.48) * mm, v(-8.1, -5.44) * mm, v(-8.12, -5.4) * mm]});
            skFitSpline(sketch, "E976", {"points": [v(-8.12, -5.4) * mm, v(-8.13, -5.37) * mm, v(-8.15, -5.34) * mm, v(-8.17, -5.3) * mm]});
            skFitSpline(sketch, "E977", {"points": [v(-8.17, -5.3) * mm, v(-8.2, -5.25) * mm, v(-8.25, -5.2) * mm, v(-8.3, -5.2) * mm]});
            skFitSpline(sketch, "E978", {"points": [v(-8.3, -5.2) * mm, v(-8.36, -5.18) * mm, v(-8.41, -5.19) * mm, v(-8.47, -5.22) * mm]});
            skFitSpline(sketch, "E979", {"points": [v(-8.47, -5.22) * mm, v(-8.53, -5.26) * mm, v(-8.56, -5.3) * mm, v(-8.57, -5.36) * mm]});
            skFitSpline(sketch, "E980", {"points": [v(-8.57, -5.36) * mm, v(-8.58, -5.41) * mm, v(-8.56, -5.47) * mm, v(-8.52, -5.54) * mm]});
            skFitSpline(sketch, "E981", {"points": [v(-8.52, -5.54) * mm, v(-8.5, -5.57) * mm, v(-8.47, -5.6) * mm, v(-8.44, -5.63) * mm]});
            skFitSpline(sketch, "E982", {"points": [v(-8.44, -5.63) * mm, v(-8.41, -5.66) * mm, v(-8.38, -5.68) * mm, v(-8.34, -5.7) * mm]});
            skLineSegment(sketch, "E983", {"start": v(-7.94, -5.42) * mm, "end": v(-8.1, -5.52) * mm});
            skFitSpline(sketch, "E984", {"points": [v(-8.5, -5.8) * mm, v(-8.53, -5.77) * mm, v(-8.57, -5.74) * mm, v(-8.6, -5.7) * mm]});
            skFitSpline(sketch, "E985", {"points": [v(-8.6, -5.7) * mm, v(-8.63, -5.67) * mm, v(-8.65, -5.63) * mm, v(-8.68, -5.6) * mm]});
            skFitSpline(sketch, "E986", {"points": [v(-8.68, -5.6) * mm, v(-8.76, -5.47) * mm, v(-8.8, -5.35) * mm, v(-8.78, -5.24) * mm]});
            skFitSpline(sketch, "E987", {"points": [v(-8.78, -5.24) * mm, v(-8.77, -5.13) * mm, v(-8.71, -5.05) * mm, v(-8.61, -4.99) * mm]});
            skFitSpline(sketch, "E988", {"points": [v(-8.61, -4.99) * mm, v(-8.5, -4.93) * mm, v(-8.4, -4.92) * mm, v(-8.31, -4.95) * mm]});
            skFitSpline(sketch, "E989", {"points": [v(-8.31, -4.95) * mm, v(-8.21, -5) * mm, v(-8.13, -5.07) * mm, v(-8.05, -5.2) * mm]});
            skFitSpline(sketch, "E990", {"points": [v(-8.05, -5.2) * mm, v(-8.02, -5.23) * mm, v(-8, -5.26) * mm, v(-7.99, -5.3) * mm]});
            skFitSpline(sketch, "E991", {"points": [v(-7.99, -5.3) * mm, v(-7.97, -5.34) * mm, v(-7.96, -5.38) * mm, v(-7.94, -5.42) * mm]});
            skLineSegment(sketch, "E992", {"start": v(-8.34, -5.7) * mm, "end": v(-8.5, -5.8) * mm});
            skFitSpline(sketch, "E993", {"points": [v(-7.57, -5.43) * mm, v(-7.52, -5.5) * mm, v(-7.48, -5.56) * mm, v(-7.43, -5.62) * mm]});
            skFitSpline(sketch, "E994", {"points": [v(-7.86, -5.95) * mm, v(-7.73, -5.98) * mm, v(-7.6, -6) * mm, v(-7.47, -6.02) * mm]});
            skFitSpline(sketch, "E995", {"points": [v(-7.47, -6.02) * mm, v(-7.4, -6.1) * mm, v(-7.34, -6.18) * mm, v(-7.28, -6.25) * mm]});
            skFitSpline(sketch, "E996", {"points": [v(-7.28, -6.25) * mm, v(-7.44, -6.22) * mm, v(-7.61, -6.2) * mm, v(-7.78, -6.15) * mm]});
            skFitSpline(sketch, "E997", {"points": [v(-7.78, -6.15) * mm, v(-7.8, -6.35) * mm, v(-7.8, -6.54) * mm, v(-7.8, -6.74) * mm]});
            skFitSpline(sketch, "E998", {"points": [v(-7.8, -6.74) * mm, v(-7.87, -6.66) * mm, v(-7.94, -6.57) * mm, v(-8, -6.49) * mm]});
            skFitSpline(sketch, "E999", {"points": [v(-8, -6.49) * mm, v(-8, -6.34) * mm, v(-8, -6.2) * mm, v(-7.98, -6.04) * mm]});
            skLineSegment(sketch, "E1000", {"start": v(-7.43, -5.62) * mm, "end": v(-7.86, -5.95) * mm});
            skFitSpline(sketch, "E1001", {"points": [v(-8.22, -6.22) * mm, v(-8.27, -6.15) * mm, v(-8.33, -6.08) * mm, v(-8.38, -6) * mm]});
            skLineSegment(sketch, "E1002", {"start": v(-7.98, -6.04) * mm, "end": v(-8.22, -6.22) * mm});
            skLineSegment(sketch, "E1003", {"start": v(-8.38, -6) * mm, "end": v(-7.57, -5.43) * mm});
            skFitSpline(sketch, "E1004", {"points": [v(-6.96, -7.2) * mm, v(-7.08, -7.08) * mm, v(-7.2, -6.96) * mm, v(-7.31, -6.84) * mm]});
            skFitSpline(sketch, "E1005", {"points": [v(-7.31, -6.84) * mm, v(-7.34, -6.81) * mm, v(-7.37, -6.78) * mm, v(-7.4, -6.75) * mm]});
            skFitSpline(sketch, "E1006", {"points": [v(-7.4, -6.75) * mm, v(-7.43, -6.8) * mm, v(-7.44, -6.84) * mm, v(-7.44, -6.88) * mm]});
            skFitSpline(sketch, "E1007", {"points": [v(-7.44, -6.88) * mm, v(-7.43, -6.9) * mm, v(-7.43, -6.92) * mm, v(-7.42, -6.94) * mm]});
            skFitSpline(sketch, "E1008", {"points": [v(-7.42, -6.94) * mm, v(-7.42, -6.94) * mm, v(-7.42, -6.94) * mm, v(-7.42, -6.94) * mm]});
            skFitSpline(sketch, "E1009", {"points": [v(-7.42, -6.94) * mm, v(-7.4, -6.97) * mm, v(-7.38, -7) * mm, v(-7.35, -7.03) * mm]});
            skFitSpline(sketch, "E1010", {"points": [v(-7.35, -7.03) * mm, v(-7.31, -7.07) * mm, v(-7.27, -7.1) * mm, v(-7.22, -7.14) * mm]});
            skFitSpline(sketch, "E1011", {"points": [v(-7.22, -7.14) * mm, v(-7.16, -7.17) * mm, v(-7.1, -7.2) * mm, v(-7.04, -7.22) * mm]});
            skLineSegment(sketch, "E1012", {"start": v(-6.91, -7.15) * mm, "end": v(-6.96, -7.2) * mm});
            skFitSpline(sketch, "E1013", {"points": [v(-7.16, -7.35) * mm, v(-7.22, -7.32) * mm, v(-7.28, -7.28) * mm, v(-7.33, -7.25) * mm]});
            skFitSpline(sketch, "E1014", {"points": [v(-7.33, -7.25) * mm, v(-7.39, -7.2) * mm, v(-7.43, -7.16) * mm, v(-7.48, -7.12) * mm]});
            skFitSpline(sketch, "E1015", {"points": [v(-7.48, -7.12) * mm, v(-7.5, -7.1) * mm, v(-7.52, -7.07) * mm, v(-7.54, -7.05) * mm]});
            skLineSegment(sketch, "E1016", {"start": v(-7.04, -7.22) * mm, "end": v(-7.16, -7.35) * mm});
            skFitSpline(sketch, "E1017", {"points": [v(-7.54, -7.05) * mm, v(-7.6, -6.96) * mm, v(-7.65, -6.87) * mm, v(-7.65, -6.78) * mm]});
            skFitSpline(sketch, "E1018", {"points": [v(-7.65, -6.78) * mm, v(-7.66, -6.68) * mm, v(-7.62, -6.58) * mm, v(-7.53, -6.5) * mm]});
            skFitSpline(sketch, "E1019", {"points": [v(-7.53, -6.5) * mm, v(-7.44, -6.43) * mm, v(-7.34, -6.4) * mm, v(-7.24, -6.42) * mm]});
            skFitSpline(sketch, "E1020", {"points": [v(-7.24, -6.42) * mm, v(-7.16, -6.43) * mm, v(-7.07, -6.47) * mm, v(-7, -6.54) * mm]});
            skFitSpline(sketch, "E1021", {"points": [v(-7, -6.54) * mm, v(-6.98, -6.56) * mm, v(-6.96, -6.57) * mm, v(-6.95, -6.59) * mm]});
            skFitSpline(sketch, "E1022", {"points": [v(-6.95, -6.59) * mm, v(-6.86, -6.68) * mm, v(-6.81, -6.77) * mm, v(-6.8, -6.87) * mm]});
            skFitSpline(sketch, "E1023", {"points": [v(-6.8, -6.87) * mm, v(-6.8, -6.98) * mm, v(-6.83, -7.07) * mm, v(-6.91, -7.15) * mm]});
            skFitSpline(sketch, "E1024", {"points": [v(-7.05, -6.9) * mm, v(-7.02, -6.87) * mm, v(-7, -6.84) * mm, v(-7, -6.8) * mm]});
            skFitSpline(sketch, "E1025", {"points": [v(-7, -6.8) * mm, v(-7.01, -6.76) * mm, v(-7.03, -6.73) * mm, v(-7.06, -6.7) * mm]});
            skFitSpline(sketch, "E1026", {"points": [v(-7.06, -6.7) * mm, v(-7.07, -6.68) * mm, v(-7.1, -6.66) * mm, v(-7.1, -6.65) * mm]});
            skFitSpline(sketch, "E1027", {"points": [v(-7.1, -6.65) * mm, v(-7.13, -6.64) * mm, v(-7.15, -6.63) * mm, v(-7.17, -6.63) * mm]});
            skFitSpline(sketch, "E1028", {"points": [v(-7.17, -6.63) * mm, v(-7.2, -6.62) * mm, v(-7.25, -6.63) * mm, v(-7.29, -6.66) * mm]});
            skFitSpline(sketch, "E1029", {"points": [v(-7.29, -6.66) * mm, v(-7.26, -6.69) * mm, v(-7.23, -6.72) * mm, v(-7.2, -6.74) * mm]});
            skFitSpline(sketch, "E1030", {"points": [v(-7.2, -6.74) * mm, v(-7.16, -6.8) * mm, v(-7.1, -6.85) * mm, v(-7.05, -6.9) * mm]});
            skFitSpline(sketch, "E1031", {"points": [v(-6.65, -6.45) * mm, v(-6.6, -6.5) * mm, v(-6.56, -6.54) * mm, v(-6.5, -6.59) * mm]});
            skFitSpline(sketch, "E1032", {"points": [v(-6.5, -6.59) * mm, v(-6.63, -6.58) * mm, v(-6.74, -6.58) * mm, v(-6.86, -6.57) * mm]});
            skFitSpline(sketch, "E1033", {"points": [v(-6.86, -6.57) * mm, v(-6.89, -6.55) * mm, v(-6.91, -6.52) * mm, v(-6.94, -6.5) * mm]});
            skFitSpline(sketch, "E1034", {"points": [v(-6.94, -6.5) * mm, v(-6.94, -6.48) * mm, v(-6.95, -6.48) * mm, v(-6.96, -6.47) * mm]});
            skFitSpline(sketch, "E1035", {"points": [v(-6.96, -6.47) * mm, v(-6.94, -6.47) * mm, v(-6.93, -6.47) * mm, v(-6.92, -6.47) * mm]});
            skFitSpline(sketch, "E1036", {"points": [v(-6.92, -6.47) * mm, v(-6.83, -6.46) * mm, v(-6.74, -6.46) * mm, v(-6.65, -6.45) * mm]});
            skFitSpline(sketch, "E1037", {"points": [v(-6.35, -8.1) * mm, v(-6.42, -8.05) * mm, v(-6.5, -8) * mm, v(-6.57, -7.94) * mm]});
            skLineSegment(sketch, "E1038", {"start": v(-6.08, -7.76) * mm, "end": v(-6.35, -8.1) * mm});
            skFitSpline(sketch, "E1039", {"points": [v(-6.36, -7.68) * mm, v(-6.32, -7.63) * mm, v(-6.3, -7.6) * mm, v(-6.28, -7.58) * mm]});
            skFitSpline(sketch, "E1040", {"points": [v(-6.28, -7.58) * mm, v(-6.27, -7.56) * mm, v(-6.26, -7.54) * mm, v(-6.26, -7.53) * mm]});
            skFitSpline(sketch, "E1041", {"points": [v(-6.26, -7.53) * mm, v(-6.26, -7.5) * mm, v(-6.26, -7.5) * mm, v(-6.27, -7.47) * mm]});
            skFitSpline(sketch, "E1042", {"points": [v(-6.27, -7.47) * mm, v(-6.28, -7.46) * mm, v(-6.29, -7.44) * mm, v(-6.3, -7.43) * mm]});
            skFitSpline(sketch, "E1043", {"points": [v(-6.3, -7.43) * mm, v(-6.35, -7.4) * mm, v(-6.4, -7.38) * mm, v(-6.44, -7.38) * mm]});
            skFitSpline(sketch, "E1044", {"points": [v(-6.44, -7.38) * mm, v(-6.49, -7.4) * mm, v(-6.53, -7.42) * mm, v(-6.57, -7.47) * mm]});
            skLineSegment(sketch, "E1045", {"start": v(-6.57, -7.94) * mm, "end": v(-6.52, -7.88) * mm});
            skLineSegment(sketch, "E1046", {"start": v(-6.52, -7.88) * mm, "end": v(-6.36, -7.68) * mm});
            skFitSpline(sketch, "E1047", {"points": [v(-6.8, -7.73) * mm, v(-6.87, -7.67) * mm, v(-6.94, -7.61) * mm, v(-7.01, -7.55) * mm]});
            skLineSegment(sketch, "E1048", {"start": v(-6.57, -7.47) * mm, "end": v(-6.8, -7.73) * mm});
            skFitSpline(sketch, "E1049", {"points": [v(-6.34, -6.82) * mm, v(-6.28, -6.88) * mm, v(-6.22, -6.93) * mm, v(-6.15, -6.99) * mm]});
            skLineSegment(sketch, "E1050", {"start": v(-7.01, -7.55) * mm, "end": v(-6.34, -6.82) * mm});
            skFitSpline(sketch, "E1051", {"points": [v(-6.4, -7.27) * mm, v(-6.35, -7.27) * mm, v(-6.3, -7.27) * mm, v(-6.25, -7.29) * mm]});
            skFitSpline(sketch, "E1052", {"points": [v(-6.25, -7.29) * mm, v(-6.2, -7.3) * mm, v(-6.16, -7.32) * mm, v(-6.12, -7.35) * mm]});
            skFitSpline(sketch, "E1053", {"points": [v(-6.12, -7.35) * mm, v(-6.05, -7.41) * mm, v(-6.01, -7.48) * mm, v(-6, -7.55) * mm]});
            skFitSpline(sketch, "E1054", {"points": [v(-6, -7.55) * mm, v(-6, -7.61) * mm, v(-6.03, -7.69) * mm, v(-6.08, -7.76) * mm]});
            skFitSpline(sketch, "E1055", {"points": [v(-6.08, -7.76) * mm, v(-6.08, -7.76) * mm, v(-6.08, -7.76) * mm, v(-6.08, -7.76) * mm, v(-6.08, -7.76) * mm]});
            skLineSegment(sketch, "E1056", {"start": v(-6.15, -6.99) * mm, "end": v(-6.4, -7.27) * mm});
            skFitSpline(sketch, "E1057", {"points": [v(-5.5, -8.03) * mm, v(-5.54, -8) * mm, v(-5.59, -7.99) * mm, v(-5.63, -8) * mm]});
            skFitSpline(sketch, "E1058", {"points": [v(-5.63, -8) * mm, v(-5.68, -8.01) * mm, v(-5.72, -8.04) * mm, v(-5.76, -8.1) * mm]});
            skFitSpline(sketch, "E1059", {"points": [v(-5.76, -8.1) * mm, v(-5.8, -8.16) * mm, v(-5.82, -8.2) * mm, v(-5.81, -8.26) * mm]});
            skFitSpline(sketch, "E1060", {"points": [v(-5.81, -8.26) * mm, v(-5.8, -8.3) * mm, v(-5.78, -8.34) * mm, v(-5.73, -8.38) * mm]});
            skFitSpline(sketch, "E1061", {"points": [v(-5.73, -8.38) * mm, v(-5.68, -8.41) * mm, v(-5.63, -8.42) * mm, v(-5.59, -8.4) * mm]});
            skFitSpline(sketch, "E1062", {"points": [v(-5.59, -8.4) * mm, v(-5.54, -8.4) * mm, v(-5.5, -8.36) * mm, v(-5.46, -8.3) * mm]});
            skFitSpline(sketch, "E1063", {"points": [v(-5.46, -8.3) * mm, v(-5.43, -8.24) * mm, v(-5.41, -8.2) * mm, v(-5.42, -8.15) * mm]});
            skFitSpline(sketch, "E1064", {"points": [v(-5.42, -8.15) * mm, v(-5.42, -8.1) * mm, v(-5.45, -8.06) * mm, v(-5.5, -8.03) * mm]});
            skFitSpline(sketch, "E1065", {"points": [v(-5.4, -7.9) * mm, v(-5.29, -7.97) * mm, v(-5.22, -8.05) * mm, v(-5.19, -8.15) * mm]});
            skFitSpline(sketch, "E1066", {"points": [v(-5.19, -8.15) * mm, v(-5.16, -8.25) * mm, v(-5.17, -8.35) * mm, v(-5.23, -8.45) * mm]});
            skFitSpline(sketch, "E1067", {"points": [v(-5.23, -8.45) * mm, v(-5.3, -8.55) * mm, v(-5.37, -8.6) * mm, v(-5.48, -8.62) * mm]});
            skFitSpline(sketch, "E1068", {"points": [v(-5.48, -8.62) * mm, v(-5.58, -8.63) * mm, v(-5.7, -8.6) * mm, v(-5.82, -8.51) * mm]});
            skFitSpline(sketch, "E1069", {"points": [v(-5.82, -8.51) * mm, v(-5.95, -8.43) * mm, v(-6.02, -8.34) * mm, v(-6.05, -8.23) * mm]});
            skFitSpline(sketch, "E1070", {"points": [v(-6.05, -8.23) * mm, v(-6.08, -8.13) * mm, v(-6.05, -8.03) * mm, v(-5.98, -7.94) * mm]});
            skFitSpline(sketch, "E1071", {"points": [v(-5.98, -7.94) * mm, v(-5.91, -7.84) * mm, v(-5.83, -7.8) * mm, v(-5.73, -7.79) * mm]});
            skFitSpline(sketch, "E1072", {"points": [v(-5.73, -7.79) * mm, v(-5.62, -7.78) * mm, v(-5.52, -7.82) * mm, v(-5.4, -7.9) * mm]});
            skFitSpline(sketch, "E1073", {"points": [v(-4.3, -8.24) * mm, v(-4.24, -8.28) * mm, v(-4.16, -8.32) * mm, v(-4.09, -8.35) * mm]});
            skFitSpline(sketch, "E1074", {"points": [v(-4.32, -8.84) * mm, v(-4.2, -8.8) * mm, v(-4.07, -8.77) * mm, v(-3.94, -8.73) * mm]});
            skFitSpline(sketch, "E1075", {"points": [v(-3.94, -8.73) * mm, v(-3.85, -8.77) * mm, v(-3.76, -8.8) * mm, v(-3.67, -8.84) * mm]});
            skFitSpline(sketch, "E1076", {"points": [v(-3.67, -8.84) * mm, v(-3.83, -8.9) * mm, v(-4, -8.94) * mm, v(-4.17, -8.99) * mm]});
            skFitSpline(sketch, "E1077", {"points": [v(-4.17, -8.99) * mm, v(-4.09, -9.16) * mm, v(-4, -9.34) * mm, v(-3.91, -9.52) * mm]});
            skFitSpline(sketch, "E1078", {"points": [v(-3.91, -9.52) * mm, v(-4.02, -9.47) * mm, v(-4.12, -9.43) * mm, v(-4.22, -9.39) * mm]});
            skFitSpline(sketch, "E1079", {"points": [v(-4.22, -9.39) * mm, v(-4.28, -9.25) * mm, v(-4.34, -9.11) * mm, v(-4.4, -8.98) * mm]});
            skLineSegment(sketch, "E1080", {"start": v(-4.09, -8.35) * mm, "end": v(-4.32, -8.84) * mm});
            skFitSpline(sketch, "E1081", {"points": [v(-4.52, -9.24) * mm, v(-4.6, -9.2) * mm, v(-4.69, -9.16) * mm, v(-4.77, -9.12) * mm]});
            skLineSegment(sketch, "E1082", {"start": v(-4.4, -8.98) * mm, "end": v(-4.52, -9.24) * mm});
            skFitSpline(sketch, "E1083", {"points": [v(-3.06, -9.28) * mm, v(-3.07, -9.26) * mm, v(-3.1, -9.25) * mm, v(-3.11, -9.24) * mm]});
            skFitSpline(sketch, "E1084", {"points": [v(-3.11, -9.24) * mm, v(-3.13, -9.23) * mm, v(-3.15, -9.22) * mm, v(-3.18, -9.21) * mm]});
            skFitSpline(sketch, "E1085", {"points": [v(-3.18, -9.21) * mm, v(-3.24, -9.19) * mm, v(-3.3, -9.19) * mm, v(-3.34, -9.21) * mm]});
            skFitSpline(sketch, "E1086", {"points": [v(-3.34, -9.21) * mm, v(-3.39, -9.24) * mm, v(-3.42, -9.28) * mm, v(-3.45, -9.35) * mm]});
            skLineSegment(sketch, "E1087", {"start": v(-4.77, -9.12) * mm, "end": v(-4.3, -8.24) * mm});
            skFitSpline(sketch, "E1088", {"points": [v(-3.56, -9.65) * mm, v(-3.65, -9.62) * mm, v(-3.73, -9.59) * mm, v(-3.82, -9.56) * mm]});
            skLineSegment(sketch, "E1089", {"start": v(-3.45, -9.35) * mm, "end": v(-3.56, -9.65) * mm});
            skFitSpline(sketch, "E1090", {"points": [v(-3.55, -8.9) * mm, v(-3.47, -8.92) * mm, v(-3.4, -8.95) * mm, v(-3.31, -8.98) * mm]});
            skLineSegment(sketch, "E1091", {"start": v(-3.82, -9.56) * mm, "end": v(-3.55, -8.9) * mm});
            skFitSpline(sketch, "E1092", {"points": [v(-3.35, -9.1) * mm, v(-3.3, -9.06) * mm, v(-3.26, -9.04) * mm, v(-3.21, -9.04) * mm]});
            skFitSpline(sketch, "E1093", {"points": [v(-3.21, -9.04) * mm, v(-3.17, -9.03) * mm, v(-3.11, -9.04) * mm, v(-3.06, -9.06) * mm]});
            skFitSpline(sketch, "E1094", {"points": [v(-3.06, -9.06) * mm, v(-3.05, -9.06) * mm, v(-3.04, -9.06) * mm, v(-3.03, -9.07) * mm]});
            skFitSpline(sketch, "E1095", {"points": [v(-3.03, -9.07) * mm, v(-3.02, -9.07) * mm, v(-3, -9.08) * mm, v(-3, -9.08) * mm]});
            skFitSpline(sketch, "E1096", {"points": [v(-3, -9.08) * mm, v(-3.01, -9.15) * mm, v(-3.03, -9.22) * mm, v(-3.06, -9.28) * mm]});
            skLineSegment(sketch, "E1097", {"start": v(-3.31, -8.98) * mm, "end": v(-3.35, -9.1) * mm});
            skFitSpline(sketch, "E1098", {"points": [v(-2.63, -9.62) * mm, v(-2.69, -9.6) * mm, v(-2.73, -9.6) * mm, v(-2.76, -9.6) * mm]});
            skFitSpline(sketch, "E1099", {"points": [v(-2.76, -9.6) * mm, v(-2.8, -9.61) * mm, v(-2.81, -9.63) * mm, v(-2.82, -9.66) * mm]});
            skFitSpline(sketch, "E1100", {"points": [v(-2.82, -9.66) * mm, v(-2.83, -9.69) * mm, v(-2.82, -9.71) * mm, v(-2.8, -9.74) * mm]});
            skFitSpline(sketch, "E1101", {"points": [v(-2.8, -9.74) * mm, v(-2.79, -9.76) * mm, v(-2.76, -9.78) * mm, v(-2.72, -9.79) * mm]});
            skFitSpline(sketch, "E1102", {"points": [v(-2.72, -9.79) * mm, v(-2.67, -9.8) * mm, v(-2.63, -9.8) * mm, v(-2.59, -9.78) * mm]});
            skFitSpline(sketch, "E1103", {"points": [v(-2.59, -9.78) * mm, v(-2.54, -9.76) * mm, v(-2.52, -9.72) * mm, v(-2.5, -9.68) * mm]});
            skFitSpline(sketch, "E1104", {"points": [v(-2.5, -9.65) * mm, v(-2.54, -9.64) * mm, v(-2.59, -9.63) * mm, v(-2.63, -9.62) * mm]});
            skLineSegment(sketch, "E1105", {"start": v(-2.5, -9.68) * mm, "end": v(-2.5, -9.65) * mm});
            skFitSpline(sketch, "E1106", {"points": [v(-2.31, -10.03) * mm, v(-2.4, -10) * mm, v(-2.5, -9.99) * mm, v(-2.58, -9.96) * mm]});
            skLineSegment(sketch, "E1107", {"start": v(-2.22, -9.63) * mm, "end": v(-2.31, -10.03) * mm});
            skFitSpline(sketch, "E1108", {"points": [v(-2.55, -9.86) * mm, v(-2.6, -9.9) * mm, v(-2.65, -9.91) * mm, v(-2.7, -9.92) * mm]});
            skFitSpline(sketch, "E1109", {"points": [v(-2.7, -9.92) * mm, v(-2.75, -9.93) * mm, v(-2.8, -9.92) * mm, v(-2.87, -9.9) * mm]});
            skFitSpline(sketch, "E1110", {"points": [v(-2.87, -9.9) * mm, v(-2.95, -9.88) * mm, v(-3.02, -9.84) * mm, v(-3.06, -9.78) * mm]});
            skFitSpline(sketch, "E1111", {"points": [v(-3.06, -9.78) * mm, v(-3.1, -9.72) * mm, v(-3.1, -9.66) * mm, v(-3.08, -9.6) * mm]});
            skFitSpline(sketch, "E1112", {"points": [v(-3.08, -9.6) * mm, v(-3.06, -9.51) * mm, v(-3, -9.47) * mm, v(-2.93, -9.45) * mm]});
            skFitSpline(sketch, "E1113", {"points": [v(-2.93, -9.45) * mm, v(-2.86, -9.43) * mm, v(-2.75, -9.44) * mm, v(-2.61, -9.48) * mm]});
            skFitSpline(sketch, "E1114", {"points": [v(-2.61, -9.48) * mm, v(-2.56, -9.5) * mm, v(-2.51, -9.5) * mm, v(-2.47, -9.52) * mm]});
            skLineSegment(sketch, "E1115", {"start": v(-2.58, -9.96) * mm, "end": v(-2.55, -9.86) * mm});
            skFitSpline(sketch, "E1116", {"points": [v(-2.46, -9.5) * mm, v(-2.45, -9.47) * mm, v(-2.46, -9.44) * mm, v(-2.49, -9.41) * mm]});
            skFitSpline(sketch, "E1117", {"points": [v(-2.49, -9.41) * mm, v(-2.51, -9.39) * mm, v(-2.56, -9.37) * mm, v(-2.63, -9.35) * mm]});
            skFitSpline(sketch, "E1118", {"points": [v(-2.63, -9.35) * mm, v(-2.68, -9.33) * mm, v(-2.73, -9.32) * mm, v(-2.78, -9.32) * mm]});
            skFitSpline(sketch, "E1119", {"points": [v(-2.78, -9.32) * mm, v(-2.83, -9.32) * mm, v(-2.88, -9.32) * mm, v(-2.92, -9.32) * mm]});
            skLineSegment(sketch, "E1120", {"start": v(-2.47, -9.52) * mm, "end": v(-2.46, -9.5) * mm});
            skFitSpline(sketch, "E1121", {"points": [v(-2.87, -9.16) * mm, v(-2.81, -9.16) * mm, v(-2.76, -9.17) * mm, v(-2.7, -9.18) * mm]});
            skFitSpline(sketch, "E1122", {"points": [v(-2.7, -9.18) * mm, v(-2.65, -9.19) * mm, v(-2.6, -9.2) * mm, v(-2.54, -9.22) * mm]});
            skFitSpline(sketch, "E1123", {"points": [v(-2.54, -9.22) * mm, v(-2.4, -9.25) * mm, v(-2.3, -9.3) * mm, v(-2.26, -9.37) * mm]});
            skFitSpline(sketch, "E1124", {"points": [v(-2.26, -9.37) * mm, v(-2.2, -9.43) * mm, v(-2.2, -9.52) * mm, v(-2.22, -9.63) * mm]});
            skLineSegment(sketch, "E1125", {"start": v(-2.92, -9.32) * mm, "end": v(-2.87, -9.16) * mm});
            skFitSpline(sketch, "E1126", {"points": [v(-1.92, -9.39) * mm, v(-1.83, -9.4) * mm, v(-1.75, -9.42) * mm, v(-1.67, -9.43) * mm]});
            skFitSpline(sketch, "E1127", {"points": [v(-1.79, -10.12) * mm, v(-1.8, -10.22) * mm, v(-1.85, -10.28) * mm, v(-1.91, -10.32) * mm]});
            skFitSpline(sketch, "E1128", {"points": [v(-1.91, -10.32) * mm, v(-1.98, -10.36) * mm, v(-2.06, -10.37) * mm, v(-2.17, -10.35) * mm]});
            skFitSpline(sketch, "E1129", {"points": [v(-2.17, -10.35) * mm, v(-2.21, -10.34) * mm, v(-2.26, -10.33) * mm, v(-2.3, -10.32) * mm]});
            skLineSegment(sketch, "E1130", {"start": v(-1.67, -9.43) * mm, "end": v(-1.79, -10.12) * mm});
            skFitSpline(sketch, "E1131", {"points": [v(-2.27, -10.17) * mm, v(-2.25, -10.18) * mm, v(-2.24, -10.18) * mm, v(-2.22, -10.18) * mm]});
            skFitSpline(sketch, "E1132", {"points": [v(-2.22, -10.18) * mm, v(-2.17, -10.2) * mm, v(-2.13, -10.2) * mm, v(-2.11, -10.18) * mm]});
            skFitSpline(sketch, "E1133", {"points": [v(-2.11, -10.18) * mm, v(-2.09, -10.16) * mm, v(-2.07, -10.13) * mm, v(-2.06, -10.07) * mm]});
            skFitSpline(sketch, "E1134", {"points": [v(-2.06, -10.07) * mm, v(-2.01, -9.84) * mm, v(-1.96, -9.61) * mm, v(-1.92, -9.39) * mm]});
            skLineSegment(sketch, "E1135", {"start": v(-2.3, -10.32) * mm, "end": v(-2.27, -10.17) * mm});
            skFitSpline(sketch, "E1136", {"points": [v(-1.86, -9.11) * mm, v(-1.78, -9.13) * mm, v(-1.7, -9.15) * mm, v(-1.62, -9.16) * mm]});
            skFitSpline(sketch, "E1137", {"points": [v(-1.65, -9.34) * mm, v(-1.73, -9.33) * mm, v(-1.82, -9.31) * mm, v(-1.9, -9.3) * mm]});
            skLineSegment(sketch, "E1138", {"start": v(-1.62, -9.16) * mm, "end": v(-1.65, -9.34) * mm});
            skLineSegment(sketch, "E1139", {"start": v(-1.9, -9.3) * mm, "end": v(-1.86, -9.11) * mm});
            skFitSpline(sketch, "E1140", {"points": [v(-0.66, -9.98) * mm, v(-0.86, -9.96) * mm, v(-1.07, -9.94) * mm, v(-1.28, -9.92) * mm]});
            skFitSpline(sketch, "E1141", {"points": [v(-1.28, -9.92) * mm, v(-1.28, -9.97) * mm, v(-1.26, -10.01) * mm, v(-1.23, -10.05) * mm]});
            skFitSpline(sketch, "E1142", {"points": [v(-1.23, -10.05) * mm, v(-1.19, -10.08) * mm, v(-1.14, -10.1) * mm, v(-1.07, -10.1) * mm]});
            skFitSpline(sketch, "E1143", {"points": [v(-1.07, -10.1) * mm, v(-1, -10.11) * mm, v(-0.95, -10.1) * mm, v(-0.89, -10.1) * mm]});
            skFitSpline(sketch, "E1144", {"points": [v(-0.89, -10.1) * mm, v(-0.83, -10.1) * mm, v(-0.77, -10.07) * mm, v(-0.7, -10.05) * mm]});
            skLineSegment(sketch, "E1145", {"start": v(-0.65, -9.91) * mm, "end": v(-0.66, -9.98) * mm});
            skFitSpline(sketch, "E1146", {"points": [v(-0.71, -10.23) * mm, v(-0.78, -10.24) * mm, v(-0.85, -10.25) * mm, v(-0.91, -10.26) * mm]});
            skFitSpline(sketch, "E1147", {"points": [v(-0.91, -10.26) * mm, v(-0.98, -10.26) * mm, v(-1.04, -10.26) * mm, v(-1.1, -10.25) * mm]});
            skFitSpline(sketch, "E1148", {"points": [v(-1.1, -10.25) * mm, v(-1.26, -10.24) * mm, v(-1.38, -10.19) * mm, v(-1.45, -10.11) * mm]});
            skFitSpline(sketch, "E1149", {"points": [v(-1.45, -10.11) * mm, v(-1.53, -10.03) * mm, v(-1.56, -9.93) * mm, v(-1.54, -9.82) * mm]});
            skFitSpline(sketch, "E1150", {"points": [v(-1.54, -9.82) * mm, v(-1.52, -9.7) * mm, v(-1.46, -9.62) * mm, v(-1.38, -9.56) * mm]});
            skFitSpline(sketch, "E1151", {"points": [v(-1.38, -9.56) * mm, v(-1.29, -9.5) * mm, v(-1.18, -9.5) * mm, v(-1.04, -9.5) * mm]});
            skFitSpline(sketch, "E1152", {"points": [v(-1.04, -9.5) * mm, v(-0.92, -9.52) * mm, v(-0.82, -9.56) * mm, v(-0.75, -9.63) * mm]});
            skFitSpline(sketch, "E1153", {"points": [v(-0.75, -9.63) * mm, v(-0.68, -9.7) * mm, v(-0.65, -9.8) * mm, v(-0.65, -9.91) * mm]});
            skFitSpline(sketch, "E1154", {"points": [v(-0.65, -9.91) * mm, v(-0.65, -9.91) * mm, v(-0.65, -9.91) * mm, v(-0.65, -9.91) * mm]});
            skLineSegment(sketch, "E1155", {"start": v(-0.7, -10.05) * mm, "end": v(-0.71, -10.23) * mm});
            skFitSpline(sketch, "E1156", {"points": [v(-0.92, -9.82) * mm, v(-0.91, -9.77) * mm, v(-0.92, -9.74) * mm, v(-0.95, -9.7) * mm]});
            skFitSpline(sketch, "E1157", {"points": [v(-0.95, -9.7) * mm, v(-0.98, -9.68) * mm, v(-1.01, -9.66) * mm, v(-1.06, -9.66) * mm]});
            skFitSpline(sketch, "E1158", {"points": [v(-1.06, -9.66) * mm, v(-1.1, -9.65) * mm, v(-1.15, -9.66) * mm, v(-1.18, -9.68) * mm]});
            skFitSpline(sketch, "E1159", {"points": [v(-1.18, -9.68) * mm, v(-1.22, -9.7) * mm, v(-1.24, -9.73) * mm, v(-1.26, -9.78) * mm]});
            skFitSpline(sketch, "E1160", {"points": [v(-1.26, -9.78) * mm, v(-1.14, -9.8) * mm, v(-1.03, -9.8) * mm, v(-0.92, -9.82) * mm]});
            skSolve(sketch);
        }
        {
            var Q0;
            Q0 = qSketchRegion(id + "F6", true);
            extrude(context, id + "F7", {"entities" : qUnion([Q0]), "depth" : 0.5 * mm, "offsetDistance" : 25 * mm});
        }
        {
            var Q0;
            Q0=makeQuery(id+"F1.opExtrude","CAP_FACE",FACE,{"disambiguationData":[OSD([sQuery(id+"F0.wireOp",EDGE,"E0")])],"isStart":false});
            var sketch = newSketch(context, id + "F8", { "sketchPlane" : qUnion([Q0])});
            skFitSpline(sketch, "E1161.1", {"points": [v(-8.88, 5.33) * mm, v(-8.82, 5.42) * mm, v(-8.76, 5.47) * mm, v(-8.7, 5.49) * mm]});
            skFitSpline(sketch, "E1161.2", {"points": [v(-8.7, 5.49) * mm, v(-8.62, 5.5) * mm, v(-8.55, 5.49) * mm, v(-8.47, 5.43) * mm, v(-8.46, 5.43) * mm, v(-8.46, 5.43) * mm, v(-8.46, 5.43) * mm]});
            skLineSegment(sketch, "E1161.3", {"start": v(-8.47, 5.43) * mm, "end": v(-8.1, 5.2) * mm});
            skFitSpline(sketch, "E1161.4", {"points": [v(-8.1, 5.2) * mm, v(-8.14, 5.13) * mm, v(-8.19, 5.06) * mm, v(-8.23, 4.98) * mm]});
            skFitSpline(sketch, "E1161.5", {"points": [v(-8.42, 5.1) * mm, v(-8.47, 5.12) * mm, v(-8.5, 5.14) * mm, v(-8.52, 5.15) * mm]});
            skFitSpline(sketch, "E1161.6", {"points": [v(-8.3, 5.02) * mm, v(-8.33, 5.04) * mm, v(-8.37, 5.06) * mm, v(-8.42, 5.1) * mm]});
            skLineSegment(sketch, "E1161.7", {"start": v(-8.23, 4.98) * mm, "end": v(-8.3, 5.02) * mm});
            skFitSpline(sketch, "E1161.8", {"points": [v(-8.52, 5.15) * mm, v(-8.57, 5.18) * mm, v(-8.6, 5.2) * mm, v(-8.63, 5.21) * mm]});
            skLineSegment(sketch, "E1161.9", {"start": v(-8.69, 4.9) * mm, "end": v(-8.38, 4.73) * mm});
            skFitSpline(sketch, "E1161.10", {"points": [v(-8.38, 4.73) * mm, v(-8.42, 4.66) * mm, v(-8.46, 4.58) * mm, v(-8.5, 4.5) * mm]});
            skLineSegment(sketch, "E1161.11", {"start": v(-8.5, 4.5) * mm, "end": v(-9.13, 4.84) * mm});
            skFitSpline(sketch, "E1161.12", {"points": [v(-9.13, 4.84) * mm, v(-9.09, 4.92) * mm, v(-9.05, 5) * mm, v(-9, 5.08) * mm]});
            skLineSegment(sketch, "E1161.13", {"start": v(-9, 5.08) * mm, "end": v(-8.91, 5.03) * mm});
            skFitSpline(sketch, "E1161.14", {"points": [v(-8.91, 5.03) * mm, v(-8.93, 5.08) * mm, v(-8.93, 5.14) * mm, v(-8.93, 5.19) * mm]});
            skFitSpline(sketch, "E1161.15", {"points": [v(-8.93, 5.19) * mm, v(-8.92, 5.24) * mm, v(-8.9, 5.29) * mm, v(-8.88, 5.33) * mm]});
            skFitSpline(sketch, "E1161.16", {"points": [v(-8.78, 5.16) * mm, v(-8.8, 5.11) * mm, v(-8.81, 5.06) * mm, v(-8.8, 5.02) * mm]});
            skFitSpline(sketch, "E1161.17", {"points": [v(-8.8, 5.02) * mm, v(-8.78, 4.97) * mm, v(-8.74, 4.93) * mm, v(-8.69, 4.9) * mm]});
            skFitSpline(sketch, "E1161.18", {"points": [v(-8.73, 5.2) * mm, v(-8.75, 5.2) * mm, v(-8.76, 5.18) * mm, v(-8.78, 5.16) * mm]});
            skFitSpline(sketch, "E1161.19", {"points": [v(-8.68, 5.23) * mm, v(-8.7, 5.22) * mm, v(-8.72, 5.22) * mm, v(-8.73, 5.2) * mm]});
            skFitSpline(sketch, "E1161.20", {"points": [v(-8.63, 5.21) * mm, v(-8.65, 5.22) * mm, v(-8.67, 5.23) * mm, v(-8.68, 5.23) * mm]});
            skSolve(sketch);
        }
        {
            var Q0;
            Q0 = qSketchRegion(id + "F8", true);
            extrude(context, id + "F9", {"entities" : qUnion([Q0]), "depth" : 0.5 * mm, "offsetDistance" : 25 * mm});
        }
        {
            var Q0;
            Q0=makeQuery(id+"F1.opExtrude","CAP_FACE",FACE,{"disambiguationData":[OSD([sQuery(id+"F0.wireOp",EDGE,"E0")])],"isStart":false});
            var sketch = newSketch(context, id + "F10", { "sketchPlane" : qUnion([Q0])});
            skCircle(sketch, "E1162", {"center": v(0, 0) * mm, "radius": 10.3 * mm});
            skSolve(sketch);
        }
        {
            var Q0;
            Q0 = qSketchRegion(id + "F10", true);
            extrude(context, id + "F11", {"entities" : qUnion([Q0]), "depth" : 0.1 * mm, "offsetDistance" : 25 * mm});
        }
        {
            var Q0;
            Q0=makeQuery(id+"F11.opExtrude","SWEPT_BODY",BODY,{"disambiguationData":[OSD([sQuery(id+"F10.wireOp",EDGE,"E1162")])]});
            var Q1;
            Q1=qCreatedBy(makeId("Origin.pointOp"),VERTEX);
            transform(context, id + "F12", {"entities" : qUnion([Q0]), "transformType" : TransformType.SCALE_UNIFORMLY, "scale" : 3.85, "scalePoint" : qUnion([Q1]), "makeCopy" : false});
        }
        {
            var Q0;
            Q0=makeQuery(id+"F11.opExtrude","SWEPT_BODY",BODY,{"disambiguationData":[OSD([sQuery(id+"F10.wireOp",EDGE,"E1162")])]});
            transform(context, id + "F13", {"entities" : qUnion([Q0]), "transformType" : TransformType.TRANSLATION_3D, "dx" : 0 * mm, "dy" : 0 * mm, "dz" : -21.7 * mm, "makeCopy" : false});
        }
        {
            var Q0;
            Q0=makeQuery(id+"F1.opExtrude","CAP_FACE",FACE,{"disambiguationData":[OSD([sQuery(id+"F0.wireOp",EDGE,"E0")])],"isStart":false});
            var sketch = newSketch(context, id + "F14", { "sketchPlane" : qUnion([Q0])});
            skCircle(sketch, "E1163.0", {"center": v(0, 0) * mm, "radius": 42.5 * mm, "construction": true});
            skCircle(sketch, "E1164", {"center": v(0, 0) * mm, "radius": 41.5 * mm});
            skCircle(sketch, "E1165", {"center": v(0, 0) * mm, "radius": 34.88 * mm});
            skSolve(sketch);
        }
        {
            var Q0;
            Q0 = qSketchRegion(id + "F14", true);
            extrude(context, id + "F15", {"entities" : qUnion([Q0]), "operationType" : NewBodyOperationType.REMOVE, "oppositeDirection" : true, "depth" : 0.4 * mm, "offsetDistance" : 25 * mm});
        }
        {
            var Q0;
            Q0=makeQuery(id+"F15.boolean.opBoolean","SPLIT",FACE,{"disambiguationData":[TD([makeQuery(id+"F15.opExtrude","SWEPT_FACE",FACE,{"disambiguationData":[OSD([sQuery(id+"F14.wireOp",EDGE,"E1165")])]})])],"derivedFrom":makeQuery(id+"F1.opExtrude","CAP_FACE",FACE,{"disambiguationData":[OSD([sQuery(id+"F0.wireOp",EDGE,"E0")])],"isStart":false})});
            var sketch = newSketch(context, id + "F16", { "sketchPlane" : qUnion([Q0])});
            skCircle(sketch, "E1166.0", {"center": v(0, 0) * mm, "radius": 34.88 * mm, "construction": true});
            skCircle(sketch, "E1167", {"center": v(0, 0) * mm, "radius": 33.88 * mm});
            skSolve(sketch);
        }
        {
            var Q0;
            Q0 = qSketchRegion(id + "F16", true);
            extrude(context, id + "F17", {"entities" : qUnion([Q0]), "operationType" : NewBodyOperationType.REMOVE, "oppositeDirection" : true, "depth" : 0.5 * mm, "offsetDistance" : 25 * mm});
        }
        {
            var Q0;
            Q0=makeQuery(id+"F17.boolean.opBoolean","COPY",EDGE,{"derivedFrom":makeQuery(id+"F17.opExtrude","CAP_EDGE",EDGE,{"disambiguationData":[OSD([sQuery(id+"F16.wireOp",EDGE,"E1167")])],"isStart":true})});
            var Q1;
            Q1=makeQuery(id+"F15.boolean.opBoolean","COPY",EDGE,{"derivedFrom":makeQuery(id+"F15.opExtrude","CAP_EDGE",EDGE,{"disambiguationData":[OSD([sQuery(id+"F14.wireOp",EDGE,"E1165")])],"isStart":true})});
            var Q2;
            Q2=makeQuery(id+"F15.boolean.opBoolean","COPY",EDGE,{"derivedFrom":makeQuery(id+"F15.opExtrude","CAP_EDGE",EDGE,{"disambiguationData":[OSD([sQuery(id+"F14.wireOp",EDGE,"E1164")])],"isStart":true})});
            fillet(context, id + "F18", {"entities" : qUnion([Q0, Q1, Q2]), "radius" : 0.1 * mm, "tangentPropagation" : true, "allowEdgeOverflow" : false});
        }
        {
            var Q0;
            Q0=makeQuery(id+"F1.opExtrude","CAP_EDGE",EDGE,{"disambiguationData":[OSD([sQuery(id+"F0.wireOp",EDGE,"E0")])],"isStart":false});
            fillet(context, id + "F19", {"entities" : qUnion([Q0]), "radius" : 0.4 * mm, "tangentPropagation" : true, "allowEdgeOverflow" : false});
        }
        {
            var Q0;
            Q0=makeQuery(id+"F17.boolean.opBoolean","COPY",FACE,{"derivedFrom":makeQuery(id+"F17.opExtrude","CAP_FACE",FACE,{"disambiguationData":[OSD([sQuery(id+"F16.wireOp",EDGE,"E1167")])],"isStart":false})});
            var sketch = newSketch(context, id + "F20", { "sketchPlane" : qUnion([Q0])});
            skText(sketch, "E1168", { "text": "2002                      2017", "fontName": "OpenSans-Bold.ttf"});
            const initialGuessF20  = {"E1168": [-0.03288, -0.0023, 1, 0, 0.00459]};
            skSetInitialGuess(sketch, initialGuessF20);
            skSolve(sketch);
        }
        {
            var Q0;
            Q0 = qSketchRegion(id + "F20", true);
            extrude(context, id + "F21", {"entities" : qUnion([Q0]), "operationType" : NewBodyOperationType.ADD, "depth" : 0.5 * mm, "offsetDistance" : 25 * mm});
        }
    });
